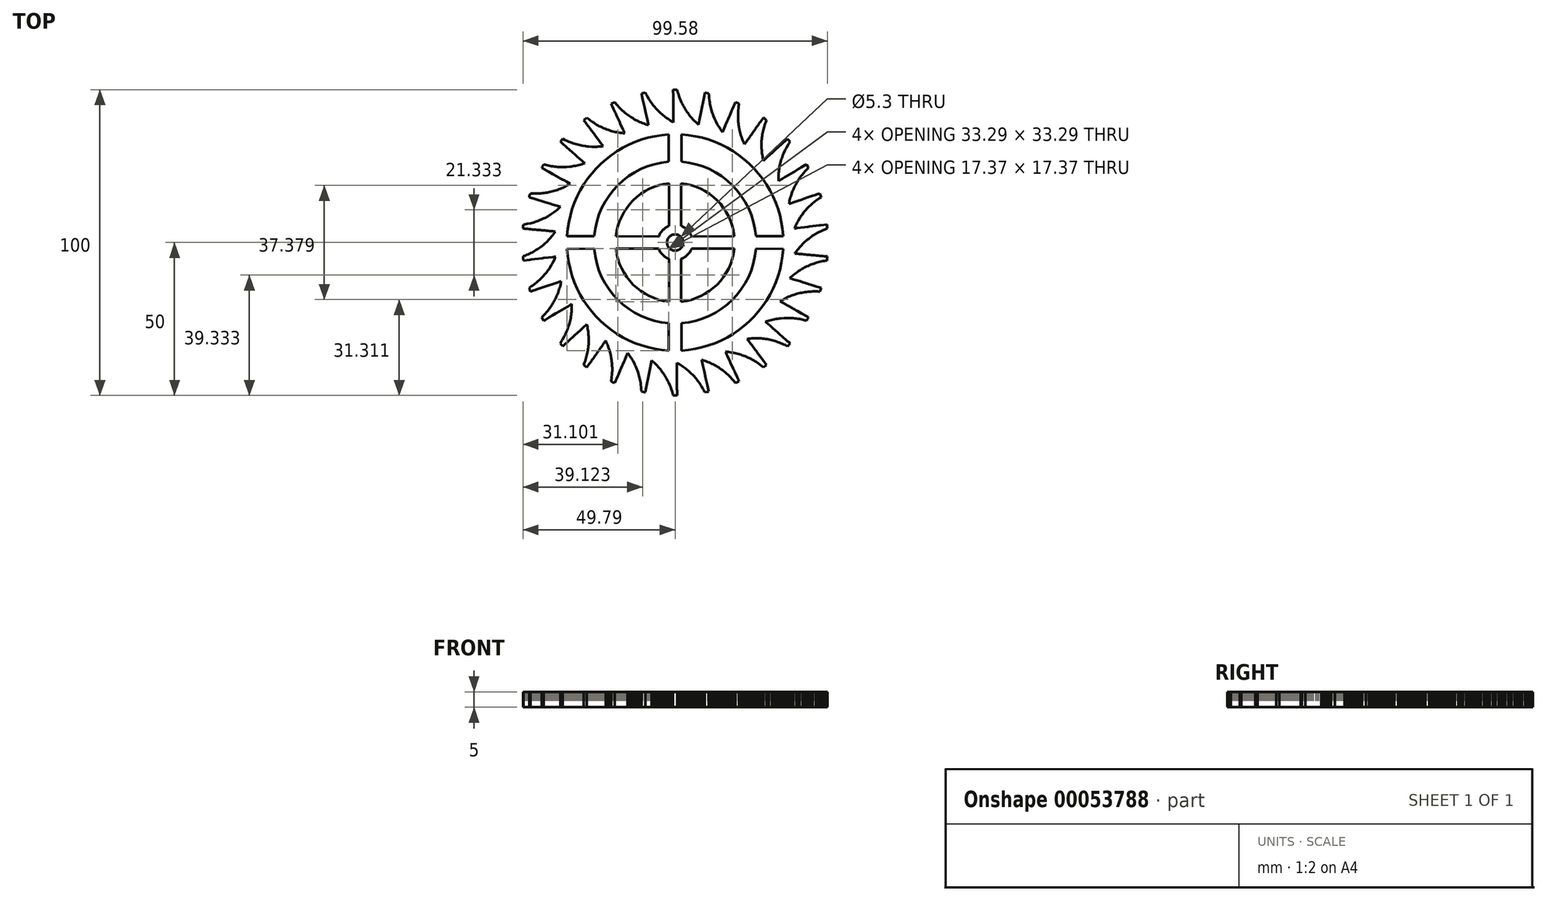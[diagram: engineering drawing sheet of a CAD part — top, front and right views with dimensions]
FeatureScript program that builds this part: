
annotation { "Feature Type Name" : "Feature", "Feature Type Description" : "" }
export const myFeature = defineFeature(function(context is Context, id is Id, definition is map)
    precondition{}
    {
        {
            var Q0;
            Q0=qCreatedBy(makeId("Top.planeOp"),FACE);
            var sketch = newSketch(context, id + "F0", { "sketchPlane" : qUnion([Q0])});
            skLineSegment(sketch, "E0", {"start": v(-36.72, 33.94) * mm, "end": v(-37.06, 33.56) * mm});
            skLineSegment(sketch, "E1", {"start": v(-37.06, 33.56) * mm, "end": v(-37.4, 33.18) * mm});
            skLineSegment(sketch, "E2", {"start": v(-37.4, 33.18) * mm, "end": v(-37.6, 32.97) * mm});
            skLineSegment(sketch, "E3", {"start": v(-37.6, 32.97) * mm, "end": v(-37.2, 32.63) * mm});
            skLineSegment(sketch, "E4", {"start": v(-37.2, 32.63) * mm, "end": v(-36.82, 32.3) * mm});
            skLineSegment(sketch, "E5", {"start": v(-36.82, 32.3) * mm, "end": v(-36.44, 31.95) * mm});
            skLineSegment(sketch, "E6", {"start": v(-36.44, 31.95) * mm, "end": v(-36.05, 31.62) * mm});
            skLineSegment(sketch, "E7", {"start": v(-36.05, 31.62) * mm, "end": v(-35.67, 31.28) * mm});
            skLineSegment(sketch, "E8", {"start": v(-35.67, 31.28) * mm, "end": v(-35.28, 30.94) * mm});
            skLineSegment(sketch, "E9", {"start": v(-35.28, 30.94) * mm, "end": v(-34.9, 30.6) * mm});
            skLineSegment(sketch, "E10", {"start": v(-34.9, 30.6) * mm, "end": v(-34.51, 30.27) * mm});
            skLineSegment(sketch, "E11", {"start": v(-34.51, 30.27) * mm, "end": v(-34.13, 29.93) * mm});
            skLineSegment(sketch, "E12", {"start": v(-34.13, 29.93) * mm, "end": v(-33.74, 29.6) * mm});
            skLineSegment(sketch, "E13", {"start": v(-33.74, 29.6) * mm, "end": v(-33.36, 29.25) * mm});
            skLineSegment(sketch, "E14", {"start": v(-33.36, 29.25) * mm, "end": v(-32.97, 28.92) * mm});
            skLineSegment(sketch, "E15", {"start": v(-32.97, 28.92) * mm, "end": v(-32.59, 28.58) * mm});
            skLineSegment(sketch, "E16", {"start": v(-32.59, 28.58) * mm, "end": v(-32.2, 28.24) * mm});
            skLineSegment(sketch, "E17", {"start": v(-32.2, 28.24) * mm, "end": v(-31.82, 27.9) * mm});
            skLineSegment(sketch, "E18", {"start": v(-31.82, 27.9) * mm, "end": v(-31.43, 27.57) * mm});
            skLineSegment(sketch, "E19", {"start": v(-31.43, 27.57) * mm, "end": v(-31.05, 27.23) * mm});
            skLineSegment(sketch, "E20", {"start": v(-31.05, 27.23) * mm, "end": v(-30.66, 26.9) * mm});
            skLineSegment(sketch, "E21", {"start": v(-30.66, 26.9) * mm, "end": v(-30.28, 26.55) * mm});
            skLineSegment(sketch, "E22", {"start": v(-30.28, 26.55) * mm, "end": v(-29.9, 26.22) * mm});
            skLineSegment(sketch, "E23", {"start": v(-29.9, 26.22) * mm, "end": v(-29.58, 25.94) * mm});
            skLineSegment(sketch, "E24", {"start": v(-29.58, 25.94) * mm, "end": v(-30.06, 25.77) * mm});
            skLineSegment(sketch, "E25", {"start": v(-30.06, 25.77) * mm, "end": v(-30.55, 25.62) * mm});
            skLineSegment(sketch, "E26", {"start": v(-30.55, 25.62) * mm, "end": v(-31.04, 25.47) * mm});
            skLineSegment(sketch, "E27", {"start": v(-31.04, 25.47) * mm, "end": v(-31.53, 25.33) * mm});
            skLineSegment(sketch, "E28", {"start": v(-31.53, 25.33) * mm, "end": v(-32.03, 25.21) * mm});
            skLineSegment(sketch, "E29", {"start": v(-32.03, 25.21) * mm, "end": v(-32.53, 25.1) * mm});
            skLineSegment(sketch, "E30", {"start": v(-32.53, 25.1) * mm, "end": v(-33.03, 25.01) * mm});
            skLineSegment(sketch, "E31", {"start": v(-33.03, 25.01) * mm, "end": v(-33.53, 24.92) * mm});
            skLineSegment(sketch, "E32", {"start": v(-33.53, 24.92) * mm, "end": v(-34.04, 24.85) * mm});
            skLineSegment(sketch, "E33", {"start": v(-34.04, 24.85) * mm, "end": v(-34.55, 24.8) * mm});
            skLineSegment(sketch, "E34", {"start": v(-34.55, 24.8) * mm, "end": v(-35.06, 24.75) * mm});
            skLineSegment(sketch, "E35", {"start": v(-35.06, 24.75) * mm, "end": v(-35.56, 24.7) * mm});
            skLineSegment(sketch, "E36", {"start": v(-35.56, 24.7) * mm, "end": v(-36.07, 24.68) * mm});
            skLineSegment(sketch, "E37", {"start": v(-36.07, 24.68) * mm, "end": v(-36.59, 24.67) * mm});
            skLineSegment(sketch, "E38", {"start": v(-36.59, 24.67) * mm, "end": v(-36.92, 24.66) * mm});
            skLineSegment(sketch, "E39", {"start": v(-36.92, 24.66) * mm, "end": v(-37.44, 24.67) * mm});
            skLineSegment(sketch, "E40", {"start": v(-37.44, 24.67) * mm, "end": v(-37.95, 24.7) * mm});
            skLineSegment(sketch, "E41", {"start": v(-37.95, 24.7) * mm, "end": v(-38.46, 24.73) * mm});
            skLineSegment(sketch, "E42", {"start": v(-38.46, 24.73) * mm, "end": v(-38.97, 24.77) * mm});
            skLineSegment(sketch, "E43", {"start": v(-38.97, 24.77) * mm, "end": v(-39.47, 24.83) * mm});
            skLineSegment(sketch, "E44", {"start": v(-39.47, 24.83) * mm, "end": v(-39.98, 24.9) * mm});
            skLineSegment(sketch, "E45", {"start": v(-39.98, 24.9) * mm, "end": v(-40.49, 24.99) * mm});
            skLineSegment(sketch, "E46", {"start": v(-40.49, 24.99) * mm, "end": v(-40.99, 25.07) * mm});
            skLineSegment(sketch, "E47", {"start": v(-40.99, 25.07) * mm, "end": v(-41.49, 25.18) * mm});
            skLineSegment(sketch, "E48", {"start": v(-41.49, 25.18) * mm, "end": v(-41.99, 25.3) * mm});
            skLineSegment(sketch, "E49", {"start": v(-41.99, 25.3) * mm, "end": v(-42.48, 25.43) * mm});
            skLineSegment(sketch, "E50", {"start": v(-42.48, 25.43) * mm, "end": v(-42.97, 25.56) * mm});
            skLineSegment(sketch, "E51", {"start": v(-42.97, 25.56) * mm, "end": v(-43.23, 25.12) * mm});
            skLineSegment(sketch, "E52", {"start": v(-43.23, 25.12) * mm, "end": v(-43.48, 24.68) * mm});
            skLineSegment(sketch, "E53", {"start": v(-43.48, 24.68) * mm, "end": v(-43.62, 24.43) * mm});
            skLineSegment(sketch, "E54", {"start": v(-43.62, 24.43) * mm, "end": v(-43.18, 24.18) * mm});
            skLineSegment(sketch, "E55", {"start": v(-43.18, 24.18) * mm, "end": v(-42.73, 23.93) * mm});
            skLineSegment(sketch, "E56", {"start": v(-42.73, 23.93) * mm, "end": v(-42.28, 23.68) * mm});
            skLineSegment(sketch, "E57", {"start": v(-42.28, 23.68) * mm, "end": v(-41.84, 23.43) * mm});
            skLineSegment(sketch, "E58", {"start": v(-41.84, 23.43) * mm, "end": v(-41.4, 23.18) * mm});
            skLineSegment(sketch, "E59", {"start": v(-41.4, 23.18) * mm, "end": v(-40.94, 22.93) * mm});
            skLineSegment(sketch, "E60", {"start": v(-40.94, 22.93) * mm, "end": v(-40.5, 22.68) * mm});
            skLineSegment(sketch, "E61", {"start": v(-40.5, 22.68) * mm, "end": v(-40.05, 22.43) * mm});
            skLineSegment(sketch, "E62", {"start": v(-40.05, 22.43) * mm, "end": v(-39.6, 22.18) * mm});
            skLineSegment(sketch, "E63", {"start": v(-39.6, 22.18) * mm, "end": v(-39.16, 21.93) * mm});
            skLineSegment(sketch, "E64", {"start": v(-39.16, 21.93) * mm, "end": v(-38.71, 21.68) * mm});
            skLineSegment(sketch, "E65", {"start": v(-38.71, 21.68) * mm, "end": v(-38.26, 21.43) * mm});
            skLineSegment(sketch, "E66", {"start": v(-38.26, 21.43) * mm, "end": v(-37.82, 21.18) * mm});
            skLineSegment(sketch, "E67", {"start": v(-37.82, 21.18) * mm, "end": v(-37.37, 20.93) * mm});
            skLineSegment(sketch, "E68", {"start": v(-37.37, 20.93) * mm, "end": v(-36.92, 20.68) * mm});
            skLineSegment(sketch, "E69", {"start": v(-36.92, 20.68) * mm, "end": v(-36.48, 20.43) * mm});
            skLineSegment(sketch, "E70", {"start": v(-36.48, 20.43) * mm, "end": v(-36.03, 20.18) * mm});
            skLineSegment(sketch, "E71", {"start": v(-36.03, 20.18) * mm, "end": v(-35.58, 19.93) * mm});
            skLineSegment(sketch, "E72", {"start": v(-35.58, 19.93) * mm, "end": v(-35.14, 19.68) * mm});
            skLineSegment(sketch, "E73", {"start": v(-35.14, 19.68) * mm, "end": v(-34.69, 19.43) * mm});
            skLineSegment(sketch, "E74", {"start": v(-34.69, 19.43) * mm, "end": v(-34.32, 19.22) * mm});
            skLineSegment(sketch, "E75", {"start": v(-34.32, 19.22) * mm, "end": v(-34.76, 18.96) * mm});
            skLineSegment(sketch, "E76", {"start": v(-34.76, 18.96) * mm, "end": v(-35.2, 18.7) * mm});
            skLineSegment(sketch, "E77", {"start": v(-35.2, 18.7) * mm, "end": v(-35.66, 18.46) * mm});
            skLineSegment(sketch, "E78", {"start": v(-35.66, 18.46) * mm, "end": v(-36.1, 18.23) * mm});
            skLineSegment(sketch, "E79", {"start": v(-36.1, 18.23) * mm, "end": v(-36.57, 18) * mm});
            skLineSegment(sketch, "E80", {"start": v(-36.57, 18) * mm, "end": v(-37.04, 17.8) * mm});
            skLineSegment(sketch, "E81", {"start": v(-37.04, 17.8) * mm, "end": v(-37.5, 17.6) * mm});
            skLineSegment(sketch, "E82", {"start": v(-37.5, 17.6) * mm, "end": v(-37.98, 17.4) * mm});
            skLineSegment(sketch, "E83", {"start": v(-37.98, 17.4) * mm, "end": v(-38.46, 17.23) * mm});
            skLineSegment(sketch, "E84", {"start": v(-38.46, 17.23) * mm, "end": v(-38.95, 17.07) * mm});
            skLineSegment(sketch, "E85", {"start": v(-38.95, 17.07) * mm, "end": v(-39.43, 16.92) * mm});
            skLineSegment(sketch, "E86", {"start": v(-39.43, 16.92) * mm, "end": v(-39.92, 16.77) * mm});
            skLineSegment(sketch, "E87", {"start": v(-39.92, 16.77) * mm, "end": v(-40.42, 16.64) * mm});
            skLineSegment(sketch, "E88", {"start": v(-40.42, 16.64) * mm, "end": v(-40.92, 16.52) * mm});
            skLineSegment(sketch, "E89", {"start": v(-40.92, 16.52) * mm, "end": v(-41.42, 16.42) * mm});
            skLineSegment(sketch, "E90", {"start": v(-41.42, 16.42) * mm, "end": v(-41.91, 16.32) * mm});
            skLineSegment(sketch, "E91", {"start": v(-41.91, 16.32) * mm, "end": v(-42.42, 16.24) * mm});
            skLineSegment(sketch, "E92", {"start": v(-42.42, 16.24) * mm, "end": v(-42.93, 16.17) * mm});
            skLineSegment(sketch, "E93", {"start": v(-42.93, 16.17) * mm, "end": v(-43.44, 16.12) * mm});
            skLineSegment(sketch, "E94", {"start": v(-43.44, 16.12) * mm, "end": v(-43.94, 16.06) * mm});
            skLineSegment(sketch, "E95", {"start": v(-43.94, 16.06) * mm, "end": v(-44.45, 16.03) * mm});
            skLineSegment(sketch, "E96", {"start": v(-44.45, 16.03) * mm, "end": v(-44.97, 16.01) * mm});
            skLineSegment(sketch, "E97", {"start": v(-44.97, 16.01) * mm, "end": v(-45.3, 16) * mm});
            skLineSegment(sketch, "E98", {"start": v(-45.3, 16) * mm, "end": v(-45.82, 16) * mm});
            skLineSegment(sketch, "E99", {"start": v(-45.82, 16) * mm, "end": v(-46.33, 16.02) * mm});
            skLineSegment(sketch, "E100", {"start": v(-46.33, 16.02) * mm, "end": v(-46.84, 16.04) * mm});
            skLineSegment(sketch, "E101", {"start": v(-46.84, 16.04) * mm, "end": v(-47.35, 16.07) * mm});
            skLineSegment(sketch, "E102", {"start": v(-47.35, 16.07) * mm, "end": v(-47.5, 15.58) * mm});
            skLineSegment(sketch, "E103", {"start": v(-47.5, 15.58) * mm, "end": v(-47.66, 15.1) * mm});
            skLineSegment(sketch, "E104", {"start": v(-47.66, 15.1) * mm, "end": v(-47.75, 14.83) * mm});
            skLineSegment(sketch, "E105", {"start": v(-47.75, 14.83) * mm, "end": v(-47.26, 14.68) * mm});
            skLineSegment(sketch, "E106", {"start": v(-47.26, 14.68) * mm, "end": v(-46.77, 14.52) * mm});
            skLineSegment(sketch, "E107", {"start": v(-46.77, 14.52) * mm, "end": v(-46.28, 14.37) * mm});
            skLineSegment(sketch, "E108", {"start": v(-46.28, 14.37) * mm, "end": v(-45.8, 14.22) * mm});
            skLineSegment(sketch, "E109", {"start": v(-45.8, 14.22) * mm, "end": v(-45.3, 14.07) * mm});
            skLineSegment(sketch, "E110", {"start": v(-45.3, 14.07) * mm, "end": v(-44.82, 13.92) * mm});
            skLineSegment(sketch, "E111", {"start": v(-44.82, 13.92) * mm, "end": v(-44.33, 13.76) * mm});
            skLineSegment(sketch, "E112", {"start": v(-44.33, 13.76) * mm, "end": v(-43.84, 13.61) * mm});
            skLineSegment(sketch, "E113", {"start": v(-43.84, 13.61) * mm, "end": v(-43.35, 13.46) * mm});
            skLineSegment(sketch, "E114", {"start": v(-43.35, 13.46) * mm, "end": v(-42.86, 13.3) * mm});
            skLineSegment(sketch, "E115", {"start": v(-42.86, 13.3) * mm, "end": v(-42.37, 13.16) * mm});
            skLineSegment(sketch, "E116", {"start": v(-42.37, 13.16) * mm, "end": v(-41.88, 13) * mm});
            skLineSegment(sketch, "E117", {"start": v(-41.88, 13) * mm, "end": v(-41.4, 12.85) * mm});
            skLineSegment(sketch, "E118", {"start": v(-41.4, 12.85) * mm, "end": v(-40.9, 12.7) * mm});
            skLineSegment(sketch, "E119", {"start": v(-40.9, 12.7) * mm, "end": v(-40.42, 12.55) * mm});
            skLineSegment(sketch, "E120", {"start": v(-40.42, 12.55) * mm, "end": v(-39.93, 12.4) * mm});
            skLineSegment(sketch, "E121", {"start": v(-39.93, 12.4) * mm, "end": v(-39.44, 12.25) * mm});
            skLineSegment(sketch, "E122", {"start": v(-39.44, 12.25) * mm, "end": v(-38.95, 12.1) * mm});
            skLineSegment(sketch, "E123", {"start": v(-38.95, 12.1) * mm, "end": v(-38.46, 11.94) * mm});
            skLineSegment(sketch, "E124", {"start": v(-38.46, 11.94) * mm, "end": v(-37.97, 11.8) * mm});
            skLineSegment(sketch, "E125", {"start": v(-37.97, 11.8) * mm, "end": v(-37.57, 11.67) * mm});
            skLineSegment(sketch, "E126", {"start": v(-37.57, 11.67) * mm, "end": v(-37.94, 11.32) * mm});
            skLineSegment(sketch, "E127", {"start": v(-37.94, 11.32) * mm, "end": v(-38.33, 10.98) * mm});
            skLineSegment(sketch, "E128", {"start": v(-38.33, 10.98) * mm, "end": v(-38.72, 10.65) * mm});
            skLineSegment(sketch, "E129", {"start": v(-38.72, 10.65) * mm, "end": v(-39.1, 10.32) * mm});
            skLineSegment(sketch, "E130", {"start": v(-39.1, 10.32) * mm, "end": v(-39.51, 10) * mm});
            skLineSegment(sketch, "E131", {"start": v(-39.51, 10) * mm, "end": v(-39.93, 9.7) * mm});
            skLineSegment(sketch, "E132", {"start": v(-39.93, 9.7) * mm, "end": v(-40.35, 9.42) * mm});
            skLineSegment(sketch, "E133", {"start": v(-40.35, 9.42) * mm, "end": v(-40.77, 9.13) * mm});
            skLineSegment(sketch, "E134", {"start": v(-40.77, 9.13) * mm, "end": v(-41.2, 8.86) * mm});
            skLineSegment(sketch, "E135", {"start": v(-41.2, 8.86) * mm, "end": v(-41.64, 8.6) * mm});
            skLineSegment(sketch, "E136", {"start": v(-41.64, 8.6) * mm, "end": v(-42.1, 8.35) * mm});
            skLineSegment(sketch, "E137", {"start": v(-42.1, 8.35) * mm, "end": v(-42.53, 8.1) * mm});
            skLineSegment(sketch, "E138", {"start": v(-42.53, 8.1) * mm, "end": v(-43, 7.87) * mm});
            skLineSegment(sketch, "E139", {"start": v(-43, 7.87) * mm, "end": v(-43.46, 7.66) * mm});
            skLineSegment(sketch, "E140", {"start": v(-43.46, 7.66) * mm, "end": v(-43.93, 7.45) * mm});
            skLineSegment(sketch, "E141", {"start": v(-43.93, 7.45) * mm, "end": v(-44.4, 7.25) * mm});
            skLineSegment(sketch, "E142", {"start": v(-44.4, 7.25) * mm, "end": v(-44.87, 7.06) * mm});
            skLineSegment(sketch, "E143", {"start": v(-44.87, 7.06) * mm, "end": v(-45.35, 6.9) * mm});
            skLineSegment(sketch, "E144", {"start": v(-45.35, 6.9) * mm, "end": v(-45.84, 6.73) * mm});
            skLineSegment(sketch, "E145", {"start": v(-45.84, 6.73) * mm, "end": v(-46.32, 6.58) * mm});
            skLineSegment(sketch, "E146", {"start": v(-46.32, 6.58) * mm, "end": v(-46.82, 6.44) * mm});
            skLineSegment(sketch, "E147", {"start": v(-46.82, 6.44) * mm, "end": v(-47.31, 6.32) * mm});
            skLineSegment(sketch, "E148", {"start": v(-47.31, 6.32) * mm, "end": v(-47.81, 6.2) * mm});
            skLineSegment(sketch, "E149", {"start": v(-47.81, 6.2) * mm, "end": v(-48.3, 6.1) * mm});
            skLineSegment(sketch, "E150", {"start": v(-48.3, 6.1) * mm, "end": v(-48.81, 6) * mm});
            skLineSegment(sketch, "E151", {"start": v(-48.81, 6) * mm, "end": v(-49.32, 5.93) * mm});
            skLineSegment(sketch, "E152", {"start": v(-49.32, 5.93) * mm, "end": v(-49.65, 5.88) * mm});
            skLineSegment(sketch, "E153", {"start": v(-49.65, 5.88) * mm, "end": v(-49.7, 5.37) * mm});
            skLineSegment(sketch, "E154", {"start": v(-49.7, 5.37) * mm, "end": v(-49.76, 4.86) * mm});
            skLineSegment(sketch, "E155", {"start": v(-49.76, 4.86) * mm, "end": v(-49.8, 4.58) * mm});
            skLineSegment(sketch, "E156", {"start": v(-49.8, 4.58) * mm, "end": v(-49.28, 4.53) * mm});
            skLineSegment(sketch, "E157", {"start": v(-49.28, 4.53) * mm, "end": v(-48.77, 4.48) * mm});
            skLineSegment(sketch, "E158", {"start": v(-48.77, 4.48) * mm, "end": v(-48.26, 4.43) * mm});
            skLineSegment(sketch, "E159", {"start": v(-48.26, 4.43) * mm, "end": v(-47.75, 4.39) * mm});
            skLineSegment(sketch, "E160", {"start": v(-47.75, 4.39) * mm, "end": v(-47.24, 4.34) * mm});
            skLineSegment(sketch, "E161", {"start": v(-47.24, 4.34) * mm, "end": v(-46.73, 4.3) * mm});
            skLineSegment(sketch, "E162", {"start": v(-46.73, 4.3) * mm, "end": v(-46.22, 4.25) * mm});
            skLineSegment(sketch, "E163", {"start": v(-46.22, 4.25) * mm, "end": v(-45.71, 4.2) * mm});
            skLineSegment(sketch, "E164", {"start": v(-45.71, 4.2) * mm, "end": v(-45.2, 4.15) * mm});
            skLineSegment(sketch, "E165", {"start": v(-45.2, 4.15) * mm, "end": v(-44.7, 4.1) * mm});
            skLineSegment(sketch, "E166", {"start": v(-44.7, 4.1) * mm, "end": v(-44.18, 4.06) * mm});
            skLineSegment(sketch, "E167", {"start": v(-44.18, 4.06) * mm, "end": v(-43.67, 4.01) * mm});
            skLineSegment(sketch, "E168", {"start": v(-43.67, 4.01) * mm, "end": v(-43.16, 3.97) * mm});
            skLineSegment(sketch, "E169", {"start": v(-43.16, 3.97) * mm, "end": v(-42.65, 3.92) * mm});
            skLineSegment(sketch, "E170", {"start": v(-42.65, 3.92) * mm, "end": v(-42.14, 3.87) * mm});
            skLineSegment(sketch, "E171", {"start": v(-42.14, 3.87) * mm, "end": v(-41.63, 3.83) * mm});
            skLineSegment(sketch, "E172", {"start": v(-41.63, 3.83) * mm, "end": v(-41.12, 3.78) * mm});
            skLineSegment(sketch, "E173", {"start": v(-41.12, 3.78) * mm, "end": v(-40.61, 3.73) * mm});
            skLineSegment(sketch, "E174", {"start": v(-40.61, 3.73) * mm, "end": v(-40.1, 3.68) * mm});
            skLineSegment(sketch, "E175", {"start": v(-40.1, 3.68) * mm, "end": v(-39.6, 3.64) * mm});
            skLineSegment(sketch, "E176", {"start": v(-39.6, 3.64) * mm, "end": v(-39.17, 3.6) * mm});
            skLineSegment(sketch, "E177", {"start": v(-39.17, 3.6) * mm, "end": v(-39.47, 3.18) * mm});
            skLineSegment(sketch, "E178", {"start": v(-39.47, 3.18) * mm, "end": v(-39.77, 2.77) * mm});
            skLineSegment(sketch, "E179", {"start": v(-39.77, 2.77) * mm, "end": v(-40.09, 2.36) * mm});
            skLineSegment(sketch, "E180", {"start": v(-40.09, 2.36) * mm, "end": v(-40.4, 1.96) * mm});
            skLineSegment(sketch, "E181", {"start": v(-40.4, 1.96) * mm, "end": v(-40.73, 1.57) * mm});
            skLineSegment(sketch, "E182", {"start": v(-40.73, 1.57) * mm, "end": v(-41.07, 1.2) * mm});
            skLineSegment(sketch, "E183", {"start": v(-41.07, 1.2) * mm, "end": v(-41.42, 0.82) * mm});
            skLineSegment(sketch, "E184", {"start": v(-41.42, 0.82) * mm, "end": v(-41.77, 0.45) * mm});
            skLineSegment(sketch, "E185", {"start": v(-41.77, 0.45) * mm, "end": v(-42.14, 0.1) * mm});
            skLineSegment(sketch, "E186", {"start": v(-42.14, 0.1) * mm, "end": v(-42.52, -0.25) * mm});
            skLineSegment(sketch, "E187", {"start": v(-42.52, -0.25) * mm, "end": v(-42.9, -0.59) * mm});
            skLineSegment(sketch, "E188", {"start": v(-42.9, -0.59) * mm, "end": v(-43.29, -0.92) * mm});
            skLineSegment(sketch, "E189", {"start": v(-43.29, -0.92) * mm, "end": v(-43.69, -1.24) * mm});
            skLineSegment(sketch, "E190", {"start": v(-43.69, -1.24) * mm, "end": v(-44.1, -1.55) * mm});
            skLineSegment(sketch, "E191", {"start": v(-44.1, -1.55) * mm, "end": v(-44.52, -1.84) * mm});
            skLineSegment(sketch, "E192", {"start": v(-44.52, -1.84) * mm, "end": v(-44.93, -2.14) * mm});
            skLineSegment(sketch, "E193", {"start": v(-44.93, -2.14) * mm, "end": v(-45.36, -2.42) * mm});
            skLineSegment(sketch, "E194", {"start": v(-45.36, -2.42) * mm, "end": v(-45.8, -2.69) * mm});
            skLineSegment(sketch, "E195", {"start": v(-45.8, -2.69) * mm, "end": v(-46.24, -2.94) * mm});
            skLineSegment(sketch, "E196", {"start": v(-46.24, -2.94) * mm, "end": v(-46.68, -3.2) * mm});
            skLineSegment(sketch, "E197", {"start": v(-46.68, -3.2) * mm, "end": v(-47.13, -3.43) * mm});
            skLineSegment(sketch, "E198", {"start": v(-47.13, -3.43) * mm, "end": v(-47.6, -3.66) * mm});
            skLineSegment(sketch, "E199", {"start": v(-47.6, -3.66) * mm, "end": v(-48.06, -3.87) * mm});
            skLineSegment(sketch, "E200", {"start": v(-48.06, -3.87) * mm, "end": v(-48.52, -4.08) * mm});
            skLineSegment(sketch, "E201", {"start": v(-48.52, -4.08) * mm, "end": v(-49, -4.28) * mm});
            skLineSegment(sketch, "E202", {"start": v(-49, -4.28) * mm, "end": v(-49.47, -4.46) * mm});
            skLineSegment(sketch, "E203", {"start": v(-49.47, -4.46) * mm, "end": v(-49.8, -4.58) * mm});
            skLineSegment(sketch, "E204", {"start": v(-49.8, -4.58) * mm, "end": v(-49.74, -5.08) * mm});
            skLineSegment(sketch, "E205", {"start": v(-49.74, -5.08) * mm, "end": v(-49.68, -5.6) * mm});
            skLineSegment(sketch, "E206", {"start": v(-49.68, -5.6) * mm, "end": v(-49.65, -5.88) * mm});
            skLineSegment(sketch, "E207", {"start": v(-49.65, -5.88) * mm, "end": v(-49.14, -5.82) * mm});
            skLineSegment(sketch, "E208", {"start": v(-49.14, -5.82) * mm, "end": v(-48.64, -5.76) * mm});
            skLineSegment(sketch, "E209", {"start": v(-48.64, -5.76) * mm, "end": v(-48.13, -5.7) * mm});
            skLineSegment(sketch, "E210", {"start": v(-48.13, -5.7) * mm, "end": v(-47.62, -5.64) * mm});
            skLineSegment(sketch, "E211", {"start": v(-47.62, -5.64) * mm, "end": v(-47.11, -5.58) * mm});
            skLineSegment(sketch, "E212", {"start": v(-47.11, -5.58) * mm, "end": v(-46.6, -5.52) * mm});
            skLineSegment(sketch, "E213", {"start": v(-46.6, -5.52) * mm, "end": v(-46.1, -5.46) * mm});
            skLineSegment(sketch, "E214", {"start": v(-46.1, -5.46) * mm, "end": v(-45.59, -5.4) * mm});
            skLineSegment(sketch, "E215", {"start": v(-45.59, -5.4) * mm, "end": v(-45.08, -5.34) * mm});
            skLineSegment(sketch, "E216", {"start": v(-45.08, -5.34) * mm, "end": v(-44.57, -5.28) * mm});
            skLineSegment(sketch, "E217", {"start": v(-44.57, -5.28) * mm, "end": v(-44.06, -5.21) * mm});
            skLineSegment(sketch, "E218", {"start": v(-44.06, -5.21) * mm, "end": v(-43.55, -5.15) * mm});
            skLineSegment(sketch, "E219", {"start": v(-43.55, -5.15) * mm, "end": v(-43.04, -5.1) * mm});
            skLineSegment(sketch, "E220", {"start": v(-43.04, -5.1) * mm, "end": v(-42.53, -5.03) * mm});
            skLineSegment(sketch, "E221", {"start": v(-42.53, -5.03) * mm, "end": v(-42.03, -4.97) * mm});
            skLineSegment(sketch, "E222", {"start": v(-42.03, -4.97) * mm, "end": v(-41.52, -4.91) * mm});
            skLineSegment(sketch, "E223", {"start": v(-41.52, -4.91) * mm, "end": v(-41, -4.85) * mm});
            skLineSegment(sketch, "E224", {"start": v(-41, -4.85) * mm, "end": v(-40.5, -4.8) * mm});
            skLineSegment(sketch, "E225", {"start": v(-40.5, -4.8) * mm, "end": v(-40, -4.73) * mm});
            skLineSegment(sketch, "E226", {"start": v(-40, -4.73) * mm, "end": v(-39.48, -4.67) * mm});
            skLineSegment(sketch, "E227", {"start": v(-39.48, -4.67) * mm, "end": v(-39.06, -4.62) * mm});
            skLineSegment(sketch, "E228", {"start": v(-39.06, -4.62) * mm, "end": v(-39.26, -5.1) * mm});
            skLineSegment(sketch, "E229", {"start": v(-39.26, -5.1) * mm, "end": v(-39.48, -5.56) * mm});
            skLineSegment(sketch, "E230", {"start": v(-39.48, -5.56) * mm, "end": v(-39.7, -6.02) * mm});
            skLineSegment(sketch, "E231", {"start": v(-39.7, -6.02) * mm, "end": v(-39.92, -6.48) * mm});
            skLineSegment(sketch, "E232", {"start": v(-39.92, -6.48) * mm, "end": v(-40.17, -6.93) * mm});
            skLineSegment(sketch, "E233", {"start": v(-40.17, -6.93) * mm, "end": v(-40.42, -7.37) * mm});
            skLineSegment(sketch, "E234", {"start": v(-40.42, -7.37) * mm, "end": v(-40.7, -7.8) * mm});
            skLineSegment(sketch, "E235", {"start": v(-40.7, -7.8) * mm, "end": v(-40.96, -8.24) * mm});
            skLineSegment(sketch, "E236", {"start": v(-40.96, -8.24) * mm, "end": v(-41.24, -8.67) * mm});
            skLineSegment(sketch, "E237", {"start": v(-41.24, -8.67) * mm, "end": v(-41.54, -9.08) * mm});
            skLineSegment(sketch, "E238", {"start": v(-41.54, -9.08) * mm, "end": v(-41.85, -9.5) * mm});
            skLineSegment(sketch, "E239", {"start": v(-41.85, -9.5) * mm, "end": v(-42.15, -9.9) * mm});
            skLineSegment(sketch, "E240", {"start": v(-42.15, -9.9) * mm, "end": v(-42.48, -10.3) * mm});
            skLineSegment(sketch, "E241", {"start": v(-42.48, -10.3) * mm, "end": v(-42.81, -10.68) * mm});
            skLineSegment(sketch, "E242", {"start": v(-42.81, -10.68) * mm, "end": v(-43.16, -11.06) * mm});
            skLineSegment(sketch, "E243", {"start": v(-43.16, -11.06) * mm, "end": v(-43.5, -11.43) * mm});
            skLineSegment(sketch, "E244", {"start": v(-43.5, -11.43) * mm, "end": v(-43.86, -11.8) * mm});
            skLineSegment(sketch, "E245", {"start": v(-43.86, -11.8) * mm, "end": v(-44.23, -12.15) * mm});
            skLineSegment(sketch, "E246", {"start": v(-44.23, -12.15) * mm, "end": v(-44.61, -12.5) * mm});
            skLineSegment(sketch, "E247", {"start": v(-44.61, -12.5) * mm, "end": v(-45, -12.83) * mm});
            skLineSegment(sketch, "E248", {"start": v(-45, -12.83) * mm, "end": v(-45.39, -13.16) * mm});
            skLineSegment(sketch, "E249", {"start": v(-45.39, -13.16) * mm, "end": v(-45.8, -13.47) * mm});
            skLineSegment(sketch, "E250", {"start": v(-45.8, -13.47) * mm, "end": v(-46.2, -13.78) * mm});
            skLineSegment(sketch, "E251", {"start": v(-46.2, -13.78) * mm, "end": v(-46.6, -14.08) * mm});
            skLineSegment(sketch, "E252", {"start": v(-46.6, -14.08) * mm, "end": v(-47.03, -14.37) * mm});
            skLineSegment(sketch, "E253", {"start": v(-47.03, -14.37) * mm, "end": v(-47.47, -14.64) * mm});
            skLineSegment(sketch, "E254", {"start": v(-47.47, -14.64) * mm, "end": v(-47.75, -14.83) * mm});
            skLineSegment(sketch, "E255", {"start": v(-47.75, -14.83) * mm, "end": v(-47.6, -15.31) * mm});
            skLineSegment(sketch, "E256", {"start": v(-47.6, -15.31) * mm, "end": v(-47.43, -15.8) * mm});
            skLineSegment(sketch, "E257", {"start": v(-47.43, -15.8) * mm, "end": v(-47.35, -16.07) * mm});
            skLineSegment(sketch, "E258", {"start": v(-47.35, -16.07) * mm, "end": v(-46.86, -15.9) * mm});
            skLineSegment(sketch, "E259", {"start": v(-46.86, -15.9) * mm, "end": v(-46.38, -15.74) * mm});
            skLineSegment(sketch, "E260", {"start": v(-46.38, -15.74) * mm, "end": v(-45.9, -15.58) * mm});
            skLineSegment(sketch, "E261", {"start": v(-45.9, -15.58) * mm, "end": v(-45.4, -15.41) * mm});
            skLineSegment(sketch, "E262", {"start": v(-45.4, -15.41) * mm, "end": v(-44.92, -15.25) * mm});
            skLineSegment(sketch, "E263", {"start": v(-44.92, -15.25) * mm, "end": v(-44.44, -15.08) * mm});
            skLineSegment(sketch, "E264", {"start": v(-44.44, -15.08) * mm, "end": v(-43.95, -14.92) * mm});
            skLineSegment(sketch, "E265", {"start": v(-43.95, -14.92) * mm, "end": v(-43.47, -14.76) * mm});
            skLineSegment(sketch, "E266", {"start": v(-43.47, -14.76) * mm, "end": v(-42.98, -14.6) * mm});
            skLineSegment(sketch, "E267", {"start": v(-42.98, -14.6) * mm, "end": v(-42.5, -14.43) * mm});
            skLineSegment(sketch, "E268", {"start": v(-42.5, -14.43) * mm, "end": v(-42.01, -14.26) * mm});
            skLineSegment(sketch, "E269", {"start": v(-42.01, -14.26) * mm, "end": v(-41.53, -14.1) * mm});
            skLineSegment(sketch, "E270", {"start": v(-41.53, -14.1) * mm, "end": v(-41.04, -13.93) * mm});
            skLineSegment(sketch, "E271", {"start": v(-41.04, -13.93) * mm, "end": v(-40.56, -13.77) * mm});
            skLineSegment(sketch, "E272", {"start": v(-40.56, -13.77) * mm, "end": v(-40.07, -13.6) * mm});
            skLineSegment(sketch, "E273", {"start": v(-40.07, -13.6) * mm, "end": v(-39.59, -13.44) * mm});
            skLineSegment(sketch, "E274", {"start": v(-39.59, -13.44) * mm, "end": v(-39.1, -13.27) * mm});
            skLineSegment(sketch, "E275", {"start": v(-39.1, -13.27) * mm, "end": v(-38.62, -13.1) * mm});
            skLineSegment(sketch, "E276", {"start": v(-38.62, -13.1) * mm, "end": v(-38.13, -12.94) * mm});
            skLineSegment(sketch, "E277", {"start": v(-38.13, -12.94) * mm, "end": v(-37.65, -12.78) * mm});
            skLineSegment(sketch, "E278", {"start": v(-37.65, -12.78) * mm, "end": v(-37.25, -12.64) * mm});
            skLineSegment(sketch, "E279", {"start": v(-37.25, -12.64) * mm, "end": v(-37.35, -13.15) * mm});
            skLineSegment(sketch, "E280", {"start": v(-37.35, -13.15) * mm, "end": v(-37.46, -13.65) * mm});
            skLineSegment(sketch, "E281", {"start": v(-37.46, -13.65) * mm, "end": v(-37.58, -14.14) * mm});
            skLineSegment(sketch, "E282", {"start": v(-37.58, -14.14) * mm, "end": v(-37.7, -14.64) * mm});
            skLineSegment(sketch, "E283", {"start": v(-37.7, -14.64) * mm, "end": v(-37.85, -15.13) * mm});
            skLineSegment(sketch, "E284", {"start": v(-37.85, -15.13) * mm, "end": v(-38, -15.62) * mm});
            skLineSegment(sketch, "E285", {"start": v(-38, -15.62) * mm, "end": v(-38.18, -16.1) * mm});
            skLineSegment(sketch, "E286", {"start": v(-38.18, -16.1) * mm, "end": v(-38.35, -16.58) * mm});
            skLineSegment(sketch, "E287", {"start": v(-38.35, -16.58) * mm, "end": v(-38.54, -17.05) * mm});
            skLineSegment(sketch, "E288", {"start": v(-38.54, -17.05) * mm, "end": v(-38.74, -17.52) * mm});
            skLineSegment(sketch, "E289", {"start": v(-38.74, -17.52) * mm, "end": v(-38.96, -17.99) * mm});
            skLineSegment(sketch, "E290", {"start": v(-38.96, -17.99) * mm, "end": v(-39.17, -18.45) * mm});
            skLineSegment(sketch, "E291", {"start": v(-39.17, -18.45) * mm, "end": v(-39.4, -18.9) * mm});
            skLineSegment(sketch, "E292", {"start": v(-39.4, -18.9) * mm, "end": v(-39.66, -19.35) * mm});
            skLineSegment(sketch, "E293", {"start": v(-39.66, -19.35) * mm, "end": v(-39.92, -19.8) * mm});
            skLineSegment(sketch, "E294", {"start": v(-39.92, -19.8) * mm, "end": v(-40.17, -20.23) * mm});
            skLineSegment(sketch, "E295", {"start": v(-40.17, -20.23) * mm, "end": v(-40.45, -20.66) * mm});
            skLineSegment(sketch, "E296", {"start": v(-40.45, -20.66) * mm, "end": v(-40.74, -21.08) * mm});
            skLineSegment(sketch, "E297", {"start": v(-40.74, -21.08) * mm, "end": v(-41.04, -21.5) * mm});
            skLineSegment(sketch, "E298", {"start": v(-41.04, -21.5) * mm, "end": v(-41.34, -21.9) * mm});
            skLineSegment(sketch, "E299", {"start": v(-41.34, -21.9) * mm, "end": v(-41.66, -22.3) * mm});
            skLineSegment(sketch, "E300", {"start": v(-41.66, -22.3) * mm, "end": v(-41.99, -22.7) * mm});
            skLineSegment(sketch, "E301", {"start": v(-41.99, -22.7) * mm, "end": v(-42.33, -23.08) * mm});
            skLineSegment(sketch, "E302", {"start": v(-42.33, -23.08) * mm, "end": v(-42.66, -23.47) * mm});
            skLineSegment(sketch, "E303", {"start": v(-42.66, -23.47) * mm, "end": v(-43.02, -23.83) * mm});
            skLineSegment(sketch, "E304", {"start": v(-43.02, -23.83) * mm, "end": v(-43.38, -24.2) * mm});
            skLineSegment(sketch, "E305", {"start": v(-43.38, -24.2) * mm, "end": v(-43.62, -24.43) * mm});
            skLineSegment(sketch, "E306", {"start": v(-43.62, -24.43) * mm, "end": v(-43.37, -24.87) * mm});
            skLineSegment(sketch, "E307", {"start": v(-43.37, -24.87) * mm, "end": v(-43.11, -25.32) * mm});
            skLineSegment(sketch, "E308", {"start": v(-43.11, -25.32) * mm, "end": v(-42.97, -25.56) * mm});
            skLineSegment(sketch, "E309", {"start": v(-42.97, -25.56) * mm, "end": v(-42.53, -25.3) * mm});
            skLineSegment(sketch, "E310", {"start": v(-42.53, -25.3) * mm, "end": v(-42.1, -25.04) * mm});
            skLineSegment(sketch, "E311", {"start": v(-42.1, -25.04) * mm, "end": v(-41.65, -24.78) * mm});
            skLineSegment(sketch, "E312", {"start": v(-41.65, -24.78) * mm, "end": v(-41.21, -24.52) * mm});
            skLineSegment(sketch, "E313", {"start": v(-41.21, -24.52) * mm, "end": v(-40.77, -24.26) * mm});
            skLineSegment(sketch, "E314", {"start": v(-40.77, -24.26) * mm, "end": v(-40.33, -24) * mm});
            skLineSegment(sketch, "E315", {"start": v(-40.33, -24) * mm, "end": v(-39.89, -23.73) * mm});
            skLineSegment(sketch, "E316", {"start": v(-39.89, -23.73) * mm, "end": v(-39.45, -23.47) * mm});
            skLineSegment(sketch, "E317", {"start": v(-39.45, -23.47) * mm, "end": v(-39, -23.2) * mm});
            skLineSegment(sketch, "E318", {"start": v(-39, -23.2) * mm, "end": v(-38.57, -22.95) * mm});
            skLineSegment(sketch, "E319", {"start": v(-38.57, -22.95) * mm, "end": v(-38.13, -22.68) * mm});
            skLineSegment(sketch, "E320", {"start": v(-38.13, -22.68) * mm, "end": v(-37.69, -22.42) * mm});
            skLineSegment(sketch, "E321", {"start": v(-37.69, -22.42) * mm, "end": v(-37.25, -22.16) * mm});
            skLineSegment(sketch, "E322", {"start": v(-37.25, -22.16) * mm, "end": v(-36.8, -21.9) * mm});
            skLineSegment(sketch, "E323", {"start": v(-36.8, -21.9) * mm, "end": v(-36.37, -21.64) * mm});
            skLineSegment(sketch, "E324", {"start": v(-36.37, -21.64) * mm, "end": v(-35.93, -21.38) * mm});
            skLineSegment(sketch, "E325", {"start": v(-35.93, -21.38) * mm, "end": v(-35.49, -21.11) * mm});
            skLineSegment(sketch, "E326", {"start": v(-35.49, -21.11) * mm, "end": v(-35.05, -20.85) * mm});
            skLineSegment(sketch, "E327", {"start": v(-35.05, -20.85) * mm, "end": v(-34.6, -20.6) * mm});
            skLineSegment(sketch, "E328", {"start": v(-34.6, -20.6) * mm, "end": v(-34.17, -20.33) * mm});
            skLineSegment(sketch, "E329", {"start": v(-34.17, -20.33) * mm, "end": v(-33.8, -20.11) * mm});
            skLineSegment(sketch, "E330", {"start": v(-33.8, -20.11) * mm, "end": v(-33.8, -20.62) * mm});
            skLineSegment(sketch, "E331", {"start": v(-33.8, -20.62) * mm, "end": v(-33.8, -21.14) * mm});
            skLineSegment(sketch, "E332", {"start": v(-33.8, -21.14) * mm, "end": v(-33.82, -21.65) * mm});
            skLineSegment(sketch, "E333", {"start": v(-33.82, -21.65) * mm, "end": v(-33.84, -22.16) * mm});
            skLineSegment(sketch, "E334", {"start": v(-33.84, -22.16) * mm, "end": v(-33.88, -22.67) * mm});
            skLineSegment(sketch, "E335", {"start": v(-33.88, -22.67) * mm, "end": v(-33.93, -23.18) * mm});
            skLineSegment(sketch, "E336", {"start": v(-33.93, -23.18) * mm, "end": v(-34, -23.68) * mm});
            skLineSegment(sketch, "E337", {"start": v(-34, -23.68) * mm, "end": v(-34.06, -24.19) * mm});
            skLineSegment(sketch, "E338", {"start": v(-34.06, -24.19) * mm, "end": v(-34.15, -24.7) * mm});
            skLineSegment(sketch, "E339", {"start": v(-34.15, -24.7) * mm, "end": v(-34.25, -25.2) * mm});
            skLineSegment(sketch, "E340", {"start": v(-34.25, -25.2) * mm, "end": v(-34.37, -25.7) * mm});
            skLineSegment(sketch, "E341", {"start": v(-34.37, -25.7) * mm, "end": v(-34.48, -26.19) * mm});
            skLineSegment(sketch, "E342", {"start": v(-34.48, -26.19) * mm, "end": v(-34.62, -26.68) * mm});
            skLineSegment(sketch, "E343", {"start": v(-34.62, -26.68) * mm, "end": v(-34.77, -27.17) * mm});
            skLineSegment(sketch, "E344", {"start": v(-34.77, -27.17) * mm, "end": v(-34.93, -27.66) * mm});
            skLineSegment(sketch, "E345", {"start": v(-34.93, -27.66) * mm, "end": v(-35.1, -28.14) * mm});
            skLineSegment(sketch, "E346", {"start": v(-35.1, -28.14) * mm, "end": v(-35.27, -28.62) * mm});
            skLineSegment(sketch, "E347", {"start": v(-35.27, -28.62) * mm, "end": v(-35.47, -29.1) * mm});
            skLineSegment(sketch, "E348", {"start": v(-35.47, -29.1) * mm, "end": v(-35.68, -29.56) * mm});
            skLineSegment(sketch, "E349", {"start": v(-35.68, -29.56) * mm, "end": v(-35.88, -30.02) * mm});
            skLineSegment(sketch, "E350", {"start": v(-35.88, -30.02) * mm, "end": v(-36.11, -30.48) * mm});
            skLineSegment(sketch, "E351", {"start": v(-36.11, -30.48) * mm, "end": v(-36.35, -30.93) * mm});
            skLineSegment(sketch, "E352", {"start": v(-36.35, -30.93) * mm, "end": v(-36.6, -31.38) * mm});
            skLineSegment(sketch, "E353", {"start": v(-36.6, -31.38) * mm, "end": v(-36.85, -31.82) * mm});
            skLineSegment(sketch, "E354", {"start": v(-36.85, -31.82) * mm, "end": v(-37.12, -32.26) * mm});
            skLineSegment(sketch, "E355", {"start": v(-37.12, -32.26) * mm, "end": v(-37.4, -32.68) * mm});
            skLineSegment(sketch, "E356", {"start": v(-37.4, -32.68) * mm, "end": v(-37.6, -32.97) * mm});
            skLineSegment(sketch, "E357", {"start": v(-37.6, -32.97) * mm, "end": v(-37.25, -33.35) * mm});
            skLineSegment(sketch, "E358", {"start": v(-37.25, -33.35) * mm, "end": v(-36.9, -33.73) * mm});
            skLineSegment(sketch, "E359", {"start": v(-36.9, -33.73) * mm, "end": v(-36.72, -33.94) * mm});
            skLineSegment(sketch, "E360", {"start": v(-36.72, -33.94) * mm, "end": v(-36.34, -33.6) * mm});
            skLineSegment(sketch, "E361", {"start": v(-36.34, -33.6) * mm, "end": v(-35.96, -33.24) * mm});
            skLineSegment(sketch, "E362", {"start": v(-35.96, -33.24) * mm, "end": v(-35.59, -32.9) * mm});
            skLineSegment(sketch, "E363", {"start": v(-35.59, -32.9) * mm, "end": v(-35.21, -32.55) * mm});
            skLineSegment(sketch, "E364", {"start": v(-35.21, -32.55) * mm, "end": v(-34.84, -32.2) * mm});
            skLineSegment(sketch, "E365", {"start": v(-34.84, -32.2) * mm, "end": v(-34.46, -31.85) * mm});
            skLineSegment(sketch, "E366", {"start": v(-34.46, -31.85) * mm, "end": v(-34.08, -31.5) * mm});
            skLineSegment(sketch, "E367", {"start": v(-34.08, -31.5) * mm, "end": v(-33.7, -31.16) * mm});
            skLineSegment(sketch, "E368", {"start": v(-33.7, -31.16) * mm, "end": v(-33.33, -30.81) * mm});
            skLineSegment(sketch, "E369", {"start": v(-33.33, -30.81) * mm, "end": v(-32.96, -30.46) * mm});
            skLineSegment(sketch, "E370", {"start": v(-32.96, -30.46) * mm, "end": v(-32.58, -30.12) * mm});
            skLineSegment(sketch, "E371", {"start": v(-32.58, -30.12) * mm, "end": v(-32.2, -29.77) * mm});
            skLineSegment(sketch, "E372", {"start": v(-32.2, -29.77) * mm, "end": v(-31.83, -29.42) * mm});
            skLineSegment(sketch, "E373", {"start": v(-31.83, -29.42) * mm, "end": v(-31.45, -29.07) * mm});
            skLineSegment(sketch, "E374", {"start": v(-31.45, -29.07) * mm, "end": v(-31.08, -28.73) * mm});
            skLineSegment(sketch, "E375", {"start": v(-31.08, -28.73) * mm, "end": v(-30.7, -28.38) * mm});
            skLineSegment(sketch, "E376", {"start": v(-30.7, -28.38) * mm, "end": v(-30.32, -28.03) * mm});
            skLineSegment(sketch, "E377", {"start": v(-30.32, -28.03) * mm, "end": v(-29.95, -27.68) * mm});
            skLineSegment(sketch, "E378", {"start": v(-29.95, -27.68) * mm, "end": v(-29.57, -27.34) * mm});
            skLineSegment(sketch, "E379", {"start": v(-29.57, -27.34) * mm, "end": v(-29.2, -26.99) * mm});
            skLineSegment(sketch, "E380", {"start": v(-29.2, -26.99) * mm, "end": v(-28.89, -26.7) * mm});
            skLineSegment(sketch, "E381", {"start": v(-28.89, -26.7) * mm, "end": v(-28.77, -27.2) * mm});
            skLineSegment(sketch, "E382", {"start": v(-28.77, -27.2) * mm, "end": v(-28.67, -27.7) * mm});
            skLineSegment(sketch, "E383", {"start": v(-28.67, -27.7) * mm, "end": v(-28.58, -28.2) * mm});
            skLineSegment(sketch, "E384", {"start": v(-28.58, -28.2) * mm, "end": v(-28.5, -28.7) * mm});
            skLineSegment(sketch, "E385", {"start": v(-28.5, -28.7) * mm, "end": v(-28.42, -29.22) * mm});
            skLineSegment(sketch, "E386", {"start": v(-28.42, -29.22) * mm, "end": v(-28.37, -29.72) * mm});
            skLineSegment(sketch, "E387", {"start": v(-28.37, -29.72) * mm, "end": v(-28.33, -30.23) * mm});
            skLineSegment(sketch, "E388", {"start": v(-28.33, -30.23) * mm, "end": v(-28.29, -30.74) * mm});
            skLineSegment(sketch, "E389", {"start": v(-28.29, -30.74) * mm, "end": v(-28.27, -31.25) * mm});
            skLineSegment(sketch, "E390", {"start": v(-28.27, -31.25) * mm, "end": v(-28.27, -31.77) * mm});
            skLineSegment(sketch, "E391", {"start": v(-28.27, -31.77) * mm, "end": v(-28.27, -32.28) * mm});
            skLineSegment(sketch, "E392", {"start": v(-28.27, -32.28) * mm, "end": v(-28.28, -32.79) * mm});
            skLineSegment(sketch, "E393", {"start": v(-28.28, -32.79) * mm, "end": v(-28.31, -33.3) * mm});
            skLineSegment(sketch, "E394", {"start": v(-28.31, -33.3) * mm, "end": v(-28.36, -33.8) * mm});
            skLineSegment(sketch, "E395", {"start": v(-28.36, -33.8) * mm, "end": v(-28.42, -34.32) * mm});
            skLineSegment(sketch, "E396", {"start": v(-28.42, -34.32) * mm, "end": v(-28.47, -34.82) * mm});
            skLineSegment(sketch, "E397", {"start": v(-28.47, -34.82) * mm, "end": v(-28.55, -35.33) * mm});
            skLineSegment(sketch, "E398", {"start": v(-28.55, -35.33) * mm, "end": v(-28.65, -35.83) * mm});
            skLineSegment(sketch, "E399", {"start": v(-28.65, -35.83) * mm, "end": v(-28.75, -36.33) * mm});
            skLineSegment(sketch, "E400", {"start": v(-28.75, -36.33) * mm, "end": v(-28.86, -36.83) * mm});
            skLineSegment(sketch, "E401", {"start": v(-28.86, -36.83) * mm, "end": v(-28.98, -37.32) * mm});
            skLineSegment(sketch, "E402", {"start": v(-28.98, -37.32) * mm, "end": v(-29.12, -37.82) * mm});
            skLineSegment(sketch, "E403", {"start": v(-29.12, -37.82) * mm, "end": v(-29.28, -38.3) * mm});
            skLineSegment(sketch, "E404", {"start": v(-29.28, -38.3) * mm, "end": v(-29.43, -38.79) * mm});
            skLineSegment(sketch, "E405", {"start": v(-29.43, -38.79) * mm, "end": v(-29.6, -39.27) * mm});
            skLineSegment(sketch, "E406", {"start": v(-29.6, -39.27) * mm, "end": v(-29.8, -39.75) * mm});
            skLineSegment(sketch, "E407", {"start": v(-29.8, -39.75) * mm, "end": v(-29.92, -40.06) * mm});
            skLineSegment(sketch, "E408", {"start": v(-29.92, -40.06) * mm, "end": v(-29.5, -40.36) * mm});
            skLineSegment(sketch, "E409", {"start": v(-29.5, -40.36) * mm, "end": v(-29.09, -40.66) * mm});
            skLineSegment(sketch, "E410", {"start": v(-29.09, -40.66) * mm, "end": v(-28.86, -40.83) * mm});
            skLineSegment(sketch, "E411", {"start": v(-28.86, -40.83) * mm, "end": v(-28.56, -40.41) * mm});
            skLineSegment(sketch, "E412", {"start": v(-28.56, -40.41) * mm, "end": v(-28.27, -40) * mm});
            skLineSegment(sketch, "E413", {"start": v(-28.27, -40) * mm, "end": v(-27.97, -39.58) * mm});
            skLineSegment(sketch, "E414", {"start": v(-27.97, -39.58) * mm, "end": v(-27.68, -39.16) * mm});
            skLineSegment(sketch, "E415", {"start": v(-27.68, -39.16) * mm, "end": v(-27.38, -38.74) * mm});
            skLineSegment(sketch, "E416", {"start": v(-27.38, -38.74) * mm, "end": v(-27.08, -38.32) * mm});
            skLineSegment(sketch, "E417", {"start": v(-27.08, -38.32) * mm, "end": v(-26.79, -37.9) * mm});
            skLineSegment(sketch, "E418", {"start": v(-26.79, -37.9) * mm, "end": v(-26.5, -37.49) * mm});
            skLineSegment(sketch, "E419", {"start": v(-26.5, -37.49) * mm, "end": v(-26.2, -37.07) * mm});
            skLineSegment(sketch, "E420", {"start": v(-26.2, -37.07) * mm, "end": v(-25.9, -36.65) * mm});
            skLineSegment(sketch, "E421", {"start": v(-25.9, -36.65) * mm, "end": v(-25.6, -36.23) * mm});
            skLineSegment(sketch, "E422", {"start": v(-25.6, -36.23) * mm, "end": v(-25.31, -35.81) * mm});
            skLineSegment(sketch, "E423", {"start": v(-25.31, -35.81) * mm, "end": v(-25.02, -35.4) * mm});
            skLineSegment(sketch, "E424", {"start": v(-25.02, -35.4) * mm, "end": v(-24.72, -34.98) * mm});
            skLineSegment(sketch, "E425", {"start": v(-24.72, -34.98) * mm, "end": v(-24.42, -34.56) * mm});
            skLineSegment(sketch, "E426", {"start": v(-24.42, -34.56) * mm, "end": v(-24.13, -34.14) * mm});
            skLineSegment(sketch, "E427", {"start": v(-24.13, -34.14) * mm, "end": v(-23.83, -33.72) * mm});
            skLineSegment(sketch, "E428", {"start": v(-23.83, -33.72) * mm, "end": v(-23.54, -33.3) * mm});
            skLineSegment(sketch, "E429", {"start": v(-23.54, -33.3) * mm, "end": v(-23.24, -32.89) * mm});
            skLineSegment(sketch, "E430", {"start": v(-23.24, -32.89) * mm, "end": v(-22.95, -32.47) * mm});
            skLineSegment(sketch, "E431", {"start": v(-22.95, -32.47) * mm, "end": v(-22.7, -32.12) * mm});
            skLineSegment(sketch, "E432", {"start": v(-22.7, -32.12) * mm, "end": v(-22.49, -32.59) * mm});
            skLineSegment(sketch, "E433", {"start": v(-22.49, -32.59) * mm, "end": v(-22.28, -33.06) * mm});
            skLineSegment(sketch, "E434", {"start": v(-22.28, -33.06) * mm, "end": v(-22.1, -33.53) * mm});
            skLineSegment(sketch, "E435", {"start": v(-22.1, -33.53) * mm, "end": v(-21.9, -34) * mm});
            skLineSegment(sketch, "E436", {"start": v(-21.9, -34) * mm, "end": v(-21.73, -34.49) * mm});
            skLineSegment(sketch, "E437", {"start": v(-21.73, -34.49) * mm, "end": v(-21.57, -34.97) * mm});
            skLineSegment(sketch, "E438", {"start": v(-21.57, -34.97) * mm, "end": v(-21.42, -35.46) * mm});
            skLineSegment(sketch, "E439", {"start": v(-21.42, -35.46) * mm, "end": v(-21.28, -35.95) * mm});
            skLineSegment(sketch, "E440", {"start": v(-21.28, -35.95) * mm, "end": v(-21.16, -36.45) * mm});
            skLineSegment(sketch, "E441", {"start": v(-21.16, -36.45) * mm, "end": v(-21.04, -36.95) * mm});
            skLineSegment(sketch, "E442", {"start": v(-21.04, -36.95) * mm, "end": v(-20.95, -37.45) * mm});
            skLineSegment(sketch, "E443", {"start": v(-20.95, -37.45) * mm, "end": v(-20.85, -37.95) * mm});
            skLineSegment(sketch, "E444", {"start": v(-20.85, -37.95) * mm, "end": v(-20.77, -38.46) * mm});
            skLineSegment(sketch, "E445", {"start": v(-20.77, -38.46) * mm, "end": v(-20.71, -38.96) * mm});
            skLineSegment(sketch, "E446", {"start": v(-20.71, -38.96) * mm, "end": v(-20.66, -39.47) * mm});
            skLineSegment(sketch, "E447", {"start": v(-20.66, -39.47) * mm, "end": v(-20.61, -39.98) * mm});
            skLineSegment(sketch, "E448", {"start": v(-20.61, -39.98) * mm, "end": v(-20.58, -40.5) * mm});
            skLineSegment(sketch, "E449", {"start": v(-20.58, -40.5) * mm, "end": v(-20.57, -41) * mm});
            skLineSegment(sketch, "E450", {"start": v(-20.57, -41) * mm, "end": v(-20.57, -41.51) * mm});
            skLineSegment(sketch, "E451", {"start": v(-20.57, -41.51) * mm, "end": v(-20.57, -42.02) * mm});
            skLineSegment(sketch, "E452", {"start": v(-20.57, -42.02) * mm, "end": v(-20.6, -42.53) * mm});
            skLineSegment(sketch, "E453", {"start": v(-20.6, -42.53) * mm, "end": v(-20.63, -43.04) * mm});
            skLineSegment(sketch, "E454", {"start": v(-20.63, -43.04) * mm, "end": v(-20.67, -43.55) * mm});
            skLineSegment(sketch, "E455", {"start": v(-20.67, -43.55) * mm, "end": v(-20.72, -44.06) * mm});
            skLineSegment(sketch, "E456", {"start": v(-20.72, -44.06) * mm, "end": v(-20.8, -44.57) * mm});
            skLineSegment(sketch, "E457", {"start": v(-20.8, -44.57) * mm, "end": v(-20.88, -45.07) * mm});
            skLineSegment(sketch, "E458", {"start": v(-20.88, -45.07) * mm, "end": v(-20.93, -45.4) * mm});
            skLineSegment(sketch, "E459", {"start": v(-20.93, -45.4) * mm, "end": v(-20.47, -45.62) * mm});
            skLineSegment(sketch, "E460", {"start": v(-20.47, -45.62) * mm, "end": v(-20, -45.82) * mm});
            skLineSegment(sketch, "E461", {"start": v(-20, -45.82) * mm, "end": v(-19.74, -45.94) * mm});
            skLineSegment(sketch, "E462", {"start": v(-19.74, -45.94) * mm, "end": v(-19.54, -45.47) * mm});
            skLineSegment(sketch, "E463", {"start": v(-19.54, -45.47) * mm, "end": v(-19.33, -45) * mm});
            skLineSegment(sketch, "E464", {"start": v(-19.33, -45) * mm, "end": v(-19.13, -44.53) * mm});
            skLineSegment(sketch, "E465", {"start": v(-19.13, -44.53) * mm, "end": v(-18.93, -44.06) * mm});
            skLineSegment(sketch, "E466", {"start": v(-18.93, -44.06) * mm, "end": v(-18.73, -43.59) * mm});
            skLineSegment(sketch, "E467", {"start": v(-18.73, -43.59) * mm, "end": v(-18.52, -43.12) * mm});
            skLineSegment(sketch, "E468", {"start": v(-18.52, -43.12) * mm, "end": v(-18.32, -42.65) * mm});
            skLineSegment(sketch, "E469", {"start": v(-18.32, -42.65) * mm, "end": v(-18.12, -42.18) * mm});
            skLineSegment(sketch, "E470", {"start": v(-18.12, -42.18) * mm, "end": v(-17.92, -41.7) * mm});
            skLineSegment(sketch, "E471", {"start": v(-17.92, -41.7) * mm, "end": v(-17.72, -41.23) * mm});
            skLineSegment(sketch, "E472", {"start": v(-17.72, -41.23) * mm, "end": v(-17.51, -40.76) * mm});
            skLineSegment(sketch, "E473", {"start": v(-17.51, -40.76) * mm, "end": v(-17.31, -40.3) * mm});
            skLineSegment(sketch, "E474", {"start": v(-17.31, -40.3) * mm, "end": v(-17.1, -39.82) * mm});
            skLineSegment(sketch, "E475", {"start": v(-17.1, -39.82) * mm, "end": v(-16.9, -39.35) * mm});
            skLineSegment(sketch, "E476", {"start": v(-16.9, -39.35) * mm, "end": v(-16.7, -38.88) * mm});
            skLineSegment(sketch, "E477", {"start": v(-16.7, -38.88) * mm, "end": v(-16.5, -38.41) * mm});
            skLineSegment(sketch, "E478", {"start": v(-16.5, -38.41) * mm, "end": v(-16.3, -37.94) * mm});
            skLineSegment(sketch, "E479", {"start": v(-16.3, -37.94) * mm, "end": v(-16.1, -37.47) * mm});
            skLineSegment(sketch, "E480", {"start": v(-16.1, -37.47) * mm, "end": v(-15.9, -37) * mm});
            skLineSegment(sketch, "E481", {"start": v(-15.9, -37) * mm, "end": v(-15.7, -36.53) * mm});
            skLineSegment(sketch, "E482", {"start": v(-15.7, -36.53) * mm, "end": v(-15.53, -36.14) * mm});
            skLineSegment(sketch, "E483", {"start": v(-15.53, -36.14) * mm, "end": v(-15.22, -36.55) * mm});
            skLineSegment(sketch, "E484", {"start": v(-15.22, -36.55) * mm, "end": v(-14.92, -36.97) * mm});
            skLineSegment(sketch, "E485", {"start": v(-14.92, -36.97) * mm, "end": v(-14.64, -37.4) * mm});
            skLineSegment(sketch, "E486", {"start": v(-14.64, -37.4) * mm, "end": v(-14.35, -37.81) * mm});
            skLineSegment(sketch, "E487", {"start": v(-14.35, -37.81) * mm, "end": v(-14.08, -38.25) * mm});
            skLineSegment(sketch, "E488", {"start": v(-14.08, -38.25) * mm, "end": v(-13.83, -38.7) * mm});
            skLineSegment(sketch, "E489", {"start": v(-13.83, -38.7) * mm, "end": v(-13.58, -39.14) * mm});
            skLineSegment(sketch, "E490", {"start": v(-13.58, -39.14) * mm, "end": v(-13.34, -39.59) * mm});
            skLineSegment(sketch, "E491", {"start": v(-13.34, -39.59) * mm, "end": v(-13.12, -40.05) * mm});
            skLineSegment(sketch, "E492", {"start": v(-13.12, -40.05) * mm, "end": v(-12.9, -40.52) * mm});
            skLineSegment(sketch, "E493", {"start": v(-12.9, -40.52) * mm, "end": v(-12.7, -40.99) * mm});
            skLineSegment(sketch, "E494", {"start": v(-12.7, -40.99) * mm, "end": v(-12.5, -41.45) * mm});
            skLineSegment(sketch, "E495", {"start": v(-12.5, -41.45) * mm, "end": v(-12.32, -41.93) * mm});
            skLineSegment(sketch, "E496", {"start": v(-12.32, -41.93) * mm, "end": v(-12.16, -42.42) * mm});
            skLineSegment(sketch, "E497", {"start": v(-12.16, -42.42) * mm, "end": v(-12, -42.9) * mm});
            skLineSegment(sketch, "E498", {"start": v(-12, -42.9) * mm, "end": v(-11.85, -43.4) * mm});
            skLineSegment(sketch, "E499", {"start": v(-11.85, -43.4) * mm, "end": v(-11.72, -43.89) * mm});
            skLineSegment(sketch, "E500", {"start": v(-11.72, -43.89) * mm, "end": v(-11.6, -44.38) * mm});
            skLineSegment(sketch, "E501", {"start": v(-11.6, -44.38) * mm, "end": v(-11.49, -44.88) * mm});
            skLineSegment(sketch, "E502", {"start": v(-11.49, -44.88) * mm, "end": v(-11.38, -45.38) * mm});
            skLineSegment(sketch, "E503", {"start": v(-11.38, -45.38) * mm, "end": v(-11.3, -45.89) * mm});
            skLineSegment(sketch, "E504", {"start": v(-11.3, -45.89) * mm, "end": v(-11.23, -46.4) * mm});
            skLineSegment(sketch, "E505", {"start": v(-11.23, -46.4) * mm, "end": v(-11.17, -46.9) * mm});
            skLineSegment(sketch, "E506", {"start": v(-11.17, -46.9) * mm, "end": v(-11.1, -47.4) * mm});
            skLineSegment(sketch, "E507", {"start": v(-11.1, -47.4) * mm, "end": v(-11.07, -47.92) * mm});
            skLineSegment(sketch, "E508", {"start": v(-11.07, -47.92) * mm, "end": v(-11.05, -48.43) * mm});
            skLineSegment(sketch, "E509", {"start": v(-11.05, -48.43) * mm, "end": v(-11.03, -48.77) * mm});
            skLineSegment(sketch, "E510", {"start": v(-11.03, -48.77) * mm, "end": v(-10.53, -48.87) * mm});
            skLineSegment(sketch, "E511", {"start": v(-10.53, -48.87) * mm, "end": v(-10.03, -48.98) * mm});
            skLineSegment(sketch, "E512", {"start": v(-10.03, -48.98) * mm, "end": v(-9.75, -49.04) * mm});
            skLineSegment(sketch, "E513", {"start": v(-9.75, -49.04) * mm, "end": v(-9.65, -48.54) * mm});
            skLineSegment(sketch, "E514", {"start": v(-9.65, -48.54) * mm, "end": v(-9.55, -48.03) * mm});
            skLineSegment(sketch, "E515", {"start": v(-9.55, -48.03) * mm, "end": v(-9.45, -47.53) * mm});
            skLineSegment(sketch, "E516", {"start": v(-9.45, -47.53) * mm, "end": v(-9.35, -47.03) * mm});
            skLineSegment(sketch, "E517", {"start": v(-9.35, -47.03) * mm, "end": v(-9.26, -46.53) * mm});
            skLineSegment(sketch, "E518", {"start": v(-9.26, -46.53) * mm, "end": v(-9.16, -46.03) * mm});
            skLineSegment(sketch, "E519", {"start": v(-9.16, -46.03) * mm, "end": v(-9.06, -45.52) * mm});
            skLineSegment(sketch, "E520", {"start": v(-9.06, -45.52) * mm, "end": v(-8.96, -45.02) * mm});
            skLineSegment(sketch, "E521", {"start": v(-8.96, -45.02) * mm, "end": v(-8.86, -44.52) * mm});
            skLineSegment(sketch, "E522", {"start": v(-8.86, -44.52) * mm, "end": v(-8.76, -44.02) * mm});
            skLineSegment(sketch, "E523", {"start": v(-8.76, -44.02) * mm, "end": v(-8.66, -43.52) * mm});
            skLineSegment(sketch, "E524", {"start": v(-8.66, -43.52) * mm, "end": v(-8.56, -43.01) * mm});
            skLineSegment(sketch, "E525", {"start": v(-8.56, -43.01) * mm, "end": v(-8.46, -42.51) * mm});
            skLineSegment(sketch, "E526", {"start": v(-8.46, -42.51) * mm, "end": v(-8.36, -42) * mm});
            skLineSegment(sketch, "E527", {"start": v(-8.36, -42) * mm, "end": v(-8.26, -41.5) * mm});
            skLineSegment(sketch, "E528", {"start": v(-8.26, -41.5) * mm, "end": v(-8.16, -41) * mm});
            skLineSegment(sketch, "E529", {"start": v(-8.16, -41) * mm, "end": v(-8.06, -40.5) * mm});
            skLineSegment(sketch, "E530", {"start": v(-8.06, -40.5) * mm, "end": v(-7.96, -40) * mm});
            skLineSegment(sketch, "E531", {"start": v(-7.96, -40) * mm, "end": v(-7.86, -39.5) * mm});
            skLineSegment(sketch, "E532", {"start": v(-7.86, -39.5) * mm, "end": v(-7.76, -39) * mm});
            skLineSegment(sketch, "E533", {"start": v(-7.76, -39) * mm, "end": v(-7.67, -38.58) * mm});
            skLineSegment(sketch, "E534", {"start": v(-7.67, -38.58) * mm, "end": v(-7.29, -38.92) * mm});
            skLineSegment(sketch, "E535", {"start": v(-7.29, -38.92) * mm, "end": v(-6.91, -39.26) * mm});
            skLineSegment(sketch, "E536", {"start": v(-6.91, -39.26) * mm, "end": v(-6.54, -39.62) * mm});
            skLineSegment(sketch, "E537", {"start": v(-6.54, -39.62) * mm, "end": v(-6.18, -39.97) * mm});
            skLineSegment(sketch, "E538", {"start": v(-6.18, -39.97) * mm, "end": v(-5.82, -40.34) * mm});
            skLineSegment(sketch, "E539", {"start": v(-5.82, -40.34) * mm, "end": v(-5.48, -40.72) * mm});
            skLineSegment(sketch, "E540", {"start": v(-5.48, -40.72) * mm, "end": v(-5.15, -41.11) * mm});
            skLineSegment(sketch, "E541", {"start": v(-5.15, -41.11) * mm, "end": v(-4.82, -41.5) * mm});
            skLineSegment(sketch, "E542", {"start": v(-4.82, -41.5) * mm, "end": v(-4.5, -41.9) * mm});
            skLineSegment(sketch, "E543", {"start": v(-4.5, -41.9) * mm, "end": v(-4.2, -42.31) * mm});
            skLineSegment(sketch, "E544", {"start": v(-4.2, -42.31) * mm, "end": v(-3.9, -42.73) * mm});
            skLineSegment(sketch, "E545", {"start": v(-3.9, -42.73) * mm, "end": v(-3.61, -43.15) * mm});
            skLineSegment(sketch, "E546", {"start": v(-3.61, -43.15) * mm, "end": v(-3.34, -43.58) * mm});
            skLineSegment(sketch, "E547", {"start": v(-3.34, -43.58) * mm, "end": v(-3.07, -44.02) * mm});
            skLineSegment(sketch, "E548", {"start": v(-3.07, -44.02) * mm, "end": v(-2.82, -44.46) * mm});
            skLineSegment(sketch, "E549", {"start": v(-2.82, -44.46) * mm, "end": v(-2.57, -44.9) * mm});
            skLineSegment(sketch, "E550", {"start": v(-2.57, -44.9) * mm, "end": v(-2.34, -45.36) * mm});
            skLineSegment(sketch, "E551", {"start": v(-2.34, -45.36) * mm, "end": v(-2.11, -45.82) * mm});
            skLineSegment(sketch, "E552", {"start": v(-2.11, -45.82) * mm, "end": v(-1.9, -46.3) * mm});
            skLineSegment(sketch, "E553", {"start": v(-1.9, -46.3) * mm, "end": v(-1.7, -46.76) * mm});
            skLineSegment(sketch, "E554", {"start": v(-1.7, -46.76) * mm, "end": v(-1.51, -47.23) * mm});
            skLineSegment(sketch, "E555", {"start": v(-1.51, -47.23) * mm, "end": v(-1.33, -47.71) * mm});
            skLineSegment(sketch, "E556", {"start": v(-1.33, -47.71) * mm, "end": v(-1.17, -48.2) * mm});
            skLineSegment(sketch, "E557", {"start": v(-1.17, -48.2) * mm, "end": v(-1, -48.68) * mm});
            skLineSegment(sketch, "E558", {"start": v(-1, -48.68) * mm, "end": v(-0.87, -49.17) * mm});
            skLineSegment(sketch, "E559", {"start": v(-0.87, -49.17) * mm, "end": v(-0.74, -49.67) * mm});
            skLineSegment(sketch, "E560", {"start": v(-0.74, -49.67) * mm, "end": v(-0.65, -50) * mm});
            skLineSegment(sketch, "E561", {"start": v(-0.65, -50) * mm, "end": v(-0.14, -50) * mm});
            skLineSegment(sketch, "E562", {"start": v(-0.14, -50) * mm, "end": v(0.37, -50) * mm});
            skLineSegment(sketch, "E563", {"start": v(0.37, -50) * mm, "end": v(0.65, -50) * mm});
            skLineSegment(sketch, "E564", {"start": v(0.65, -50) * mm, "end": v(0.65, -49.48) * mm});
            skLineSegment(sketch, "E565", {"start": v(0.65, -49.48) * mm, "end": v(0.64, -48.97) * mm});
            skLineSegment(sketch, "E566", {"start": v(0.64, -48.97) * mm, "end": v(0.63, -48.46) * mm});
            skLineSegment(sketch, "E567", {"start": v(0.63, -48.46) * mm, "end": v(0.63, -47.95) * mm});
            skLineSegment(sketch, "E568", {"start": v(0.63, -47.95) * mm, "end": v(0.62, -47.44) * mm});
            skLineSegment(sketch, "E569", {"start": v(0.62, -47.44) * mm, "end": v(0.61, -46.92) * mm});
            skLineSegment(sketch, "E570", {"start": v(0.61, -46.92) * mm, "end": v(0.6, -46.41) * mm});
            skLineSegment(sketch, "E571", {"start": v(0.6, -46.41) * mm, "end": v(0.6, -45.9) * mm});
            skLineSegment(sketch, "E572", {"start": v(0.6, -45.9) * mm, "end": v(0.6, -45.39) * mm});
            skLineSegment(sketch, "E573", {"start": v(0.6, -45.39) * mm, "end": v(0.59, -44.88) * mm});
            skLineSegment(sketch, "E574", {"start": v(0.59, -44.88) * mm, "end": v(0.58, -44.36) * mm});
            skLineSegment(sketch, "E575", {"start": v(0.58, -44.36) * mm, "end": v(0.57, -43.85) * mm});
            skLineSegment(sketch, "E576", {"start": v(0.57, -43.85) * mm, "end": v(0.57, -43.34) * mm});
            skLineSegment(sketch, "E577", {"start": v(0.57, -43.34) * mm, "end": v(0.56, -42.83) * mm});
            skLineSegment(sketch, "E578", {"start": v(0.56, -42.83) * mm, "end": v(0.55, -42.32) * mm});
            skLineSegment(sketch, "E579", {"start": v(0.55, -42.32) * mm, "end": v(0.55, -41.8) * mm});
            skLineSegment(sketch, "E580", {"start": v(0.55, -41.8) * mm, "end": v(0.54, -41.3) * mm});
            skLineSegment(sketch, "E581", {"start": v(0.54, -41.3) * mm, "end": v(0.53, -40.78) * mm});
            skLineSegment(sketch, "E582", {"start": v(0.53, -40.78) * mm, "end": v(0.53, -40.27) * mm});
            skLineSegment(sketch, "E583", {"start": v(0.53, -40.27) * mm, "end": v(0.52, -39.76) * mm});
            skLineSegment(sketch, "E584", {"start": v(0.52, -39.76) * mm, "end": v(0.51, -39.33) * mm});
            skLineSegment(sketch, "E585", {"start": v(0.51, -39.33) * mm, "end": v(0.96, -39.58) * mm});
            skLineSegment(sketch, "E586", {"start": v(0.96, -39.58) * mm, "end": v(1.4, -39.84) * mm});
            skLineSegment(sketch, "E587", {"start": v(1.4, -39.84) * mm, "end": v(1.84, -40.11) * mm});
            skLineSegment(sketch, "E588", {"start": v(1.84, -40.11) * mm, "end": v(2.27, -40.38) * mm});
            skLineSegment(sketch, "E589", {"start": v(2.27, -40.38) * mm, "end": v(2.7, -40.67) * mm});
            skLineSegment(sketch, "E590", {"start": v(2.7, -40.67) * mm, "end": v(3.1, -40.97) * mm});
            skLineSegment(sketch, "E591", {"start": v(3.1, -40.97) * mm, "end": v(3.51, -41.28) * mm});
            skLineSegment(sketch, "E592", {"start": v(3.51, -41.28) * mm, "end": v(3.92, -41.6) * mm});
            skLineSegment(sketch, "E593", {"start": v(3.92, -41.6) * mm, "end": v(4.3, -41.92) * mm});
            skLineSegment(sketch, "E594", {"start": v(4.3, -41.92) * mm, "end": v(4.7, -42.26) * mm});
            skLineSegment(sketch, "E595", {"start": v(4.7, -42.26) * mm, "end": v(5.07, -42.6) * mm});
            skLineSegment(sketch, "E596", {"start": v(5.07, -42.6) * mm, "end": v(5.44, -42.96) * mm});
            skLineSegment(sketch, "E597", {"start": v(5.44, -42.96) * mm, "end": v(5.8, -43.32) * mm});
            skLineSegment(sketch, "E598", {"start": v(5.8, -43.32) * mm, "end": v(6.15, -43.7) * mm});
            skLineSegment(sketch, "E599", {"start": v(6.15, -43.7) * mm, "end": v(6.49, -44.08) * mm});
            skLineSegment(sketch, "E600", {"start": v(6.49, -44.08) * mm, "end": v(6.82, -44.46) * mm});
            skLineSegment(sketch, "E601", {"start": v(6.82, -44.46) * mm, "end": v(7.15, -44.86) * mm});
            skLineSegment(sketch, "E602", {"start": v(7.15, -44.86) * mm, "end": v(7.46, -45.26) * mm});
            skLineSegment(sketch, "E603", {"start": v(7.46, -45.26) * mm, "end": v(7.76, -45.68) * mm});
            skLineSegment(sketch, "E604", {"start": v(7.76, -45.68) * mm, "end": v(8.06, -46.09) * mm});
            skLineSegment(sketch, "E605", {"start": v(8.06, -46.09) * mm, "end": v(8.34, -46.51) * mm});
            skLineSegment(sketch, "E606", {"start": v(8.34, -46.51) * mm, "end": v(8.61, -46.95) * mm});
            skLineSegment(sketch, "E607", {"start": v(8.61, -46.95) * mm, "end": v(8.87, -47.39) * mm});
            skLineSegment(sketch, "E608", {"start": v(8.87, -47.39) * mm, "end": v(9.13, -47.83) * mm});
            skLineSegment(sketch, "E609", {"start": v(9.13, -47.83) * mm, "end": v(9.37, -48.28) * mm});
            skLineSegment(sketch, "E610", {"start": v(9.37, -48.28) * mm, "end": v(9.6, -48.74) * mm});
            skLineSegment(sketch, "E611", {"start": v(9.6, -48.74) * mm, "end": v(9.75, -49.04) * mm});
            skLineSegment(sketch, "E612", {"start": v(9.75, -49.04) * mm, "end": v(10.26, -48.93) * mm});
            skLineSegment(sketch, "E613", {"start": v(10.26, -48.93) * mm, "end": v(10.76, -48.83) * mm});
            skLineSegment(sketch, "E614", {"start": v(10.76, -48.83) * mm, "end": v(11.03, -48.77) * mm});
            skLineSegment(sketch, "E615", {"start": v(11.03, -48.77) * mm, "end": v(10.92, -48.27) * mm});
            skLineSegment(sketch, "E616", {"start": v(10.92, -48.27) * mm, "end": v(10.8, -47.77) * mm});
            skLineSegment(sketch, "E617", {"start": v(10.8, -47.77) * mm, "end": v(10.7, -47.27) * mm});
            skLineSegment(sketch, "E618", {"start": v(10.7, -47.27) * mm, "end": v(10.58, -46.77) * mm});
            skLineSegment(sketch, "E619", {"start": v(10.58, -46.77) * mm, "end": v(10.47, -46.27) * mm});
            skLineSegment(sketch, "E620", {"start": v(10.47, -46.27) * mm, "end": v(10.36, -45.77) * mm});
            skLineSegment(sketch, "E621", {"start": v(10.36, -45.77) * mm, "end": v(10.24, -45.27) * mm});
            skLineSegment(sketch, "E622", {"start": v(10.24, -45.27) * mm, "end": v(10.13, -44.77) * mm});
            skLineSegment(sketch, "E623", {"start": v(10.13, -44.77) * mm, "end": v(10.02, -44.27) * mm});
            skLineSegment(sketch, "E624", {"start": v(10.02, -44.27) * mm, "end": v(9.9, -43.77) * mm});
            skLineSegment(sketch, "E625", {"start": v(9.9, -43.77) * mm, "end": v(9.8, -43.27) * mm});
            skLineSegment(sketch, "E626", {"start": v(9.8, -43.27) * mm, "end": v(9.68, -42.77) * mm});
            skLineSegment(sketch, "E627", {"start": v(9.68, -42.77) * mm, "end": v(9.57, -42.27) * mm});
            skLineSegment(sketch, "E628", {"start": v(9.57, -42.27) * mm, "end": v(9.45, -41.78) * mm});
            skLineSegment(sketch, "E629", {"start": v(9.45, -41.78) * mm, "end": v(9.34, -41.28) * mm});
            skLineSegment(sketch, "E630", {"start": v(9.34, -41.28) * mm, "end": v(9.23, -40.78) * mm});
            skLineSegment(sketch, "E631", {"start": v(9.23, -40.78) * mm, "end": v(9.11, -40.28) * mm});
            skLineSegment(sketch, "E632", {"start": v(9.11, -40.28) * mm, "end": v(9, -39.78) * mm});
            skLineSegment(sketch, "E633", {"start": v(9, -39.78) * mm, "end": v(8.89, -39.28) * mm});
            skLineSegment(sketch, "E634", {"start": v(8.89, -39.28) * mm, "end": v(8.77, -38.78) * mm});
            skLineSegment(sketch, "E635", {"start": v(8.77, -38.78) * mm, "end": v(8.68, -38.37) * mm});
            skLineSegment(sketch, "E636", {"start": v(8.68, -38.37) * mm, "end": v(9.17, -38.52) * mm});
            skLineSegment(sketch, "E637", {"start": v(9.17, -38.52) * mm, "end": v(9.66, -38.68) * mm});
            skLineSegment(sketch, "E638", {"start": v(9.66, -38.68) * mm, "end": v(10.14, -38.85) * mm});
            skLineSegment(sketch, "E639", {"start": v(10.14, -38.85) * mm, "end": v(10.62, -39.03) * mm});
            skLineSegment(sketch, "E640", {"start": v(10.62, -39.03) * mm, "end": v(11.09, -39.22) * mm});
            skLineSegment(sketch, "E641", {"start": v(11.09, -39.22) * mm, "end": v(11.56, -39.43) * mm});
            skLineSegment(sketch, "E642", {"start": v(11.56, -39.43) * mm, "end": v(12.02, -39.65) * mm});
            skLineSegment(sketch, "E643", {"start": v(12.02, -39.65) * mm, "end": v(12.48, -39.87) * mm});
            skLineSegment(sketch, "E644", {"start": v(12.48, -39.87) * mm, "end": v(12.93, -40.11) * mm});
            skLineSegment(sketch, "E645", {"start": v(12.93, -40.11) * mm, "end": v(13.38, -40.36) * mm});
            skLineSegment(sketch, "E646", {"start": v(13.38, -40.36) * mm, "end": v(13.82, -40.63) * mm});
            skLineSegment(sketch, "E647", {"start": v(13.82, -40.63) * mm, "end": v(14.25, -40.89) * mm});
            skLineSegment(sketch, "E648", {"start": v(14.25, -40.89) * mm, "end": v(14.68, -41.17) * mm});
            skLineSegment(sketch, "E649", {"start": v(14.68, -41.17) * mm, "end": v(15.1, -41.46) * mm});
            skLineSegment(sketch, "E650", {"start": v(15.1, -41.46) * mm, "end": v(15.5, -41.77) * mm});
            skLineSegment(sketch, "E651", {"start": v(15.5, -41.77) * mm, "end": v(15.92, -42.07) * mm});
            skLineSegment(sketch, "E652", {"start": v(15.92, -42.07) * mm, "end": v(16.32, -42.4) * mm});
            skLineSegment(sketch, "E653", {"start": v(16.32, -42.4) * mm, "end": v(16.7, -42.72) * mm});
            skLineSegment(sketch, "E654", {"start": v(16.7, -42.72) * mm, "end": v(17.09, -43.06) * mm});
            skLineSegment(sketch, "E655", {"start": v(17.09, -43.06) * mm, "end": v(17.47, -43.4) * mm});
            skLineSegment(sketch, "E656", {"start": v(17.47, -43.4) * mm, "end": v(17.83, -43.76) * mm});
            skLineSegment(sketch, "E657", {"start": v(17.83, -43.76) * mm, "end": v(18.19, -44.13) * mm});
            skLineSegment(sketch, "E658", {"start": v(18.19, -44.13) * mm, "end": v(18.53, -44.5) * mm});
            skLineSegment(sketch, "E659", {"start": v(18.53, -44.5) * mm, "end": v(18.88, -44.88) * mm});
            skLineSegment(sketch, "E660", {"start": v(18.88, -44.88) * mm, "end": v(19.2, -45.27) * mm});
            skLineSegment(sketch, "E661", {"start": v(19.2, -45.27) * mm, "end": v(19.53, -45.67) * mm});
            skLineSegment(sketch, "E662", {"start": v(19.53, -45.67) * mm, "end": v(19.74, -45.94) * mm});
            skLineSegment(sketch, "E663", {"start": v(19.74, -45.94) * mm, "end": v(20.2, -45.73) * mm});
            skLineSegment(sketch, "E664", {"start": v(20.2, -45.73) * mm, "end": v(20.67, -45.52) * mm});
            skLineSegment(sketch, "E665", {"start": v(20.67, -45.52) * mm, "end": v(20.93, -45.4) * mm});
            skLineSegment(sketch, "E666", {"start": v(20.93, -45.4) * mm, "end": v(20.72, -44.94) * mm});
            skLineSegment(sketch, "E667", {"start": v(20.72, -44.94) * mm, "end": v(20.5, -44.48) * mm});
            skLineSegment(sketch, "E668", {"start": v(20.5, -44.48) * mm, "end": v(20.29, -44.01) * mm});
            skLineSegment(sketch, "E669", {"start": v(20.29, -44.01) * mm, "end": v(20.08, -43.55) * mm});
            skLineSegment(sketch, "E670", {"start": v(20.08, -43.55) * mm, "end": v(19.86, -43.08) * mm});
            skLineSegment(sketch, "E671", {"start": v(19.86, -43.08) * mm, "end": v(19.65, -42.62) * mm});
            skLineSegment(sketch, "E672", {"start": v(19.65, -42.62) * mm, "end": v(19.43, -42.15) * mm});
            skLineSegment(sketch, "E673", {"start": v(19.43, -42.15) * mm, "end": v(19.22, -41.69) * mm});
            skLineSegment(sketch, "E674", {"start": v(19.22, -41.69) * mm, "end": v(19, -41.22) * mm});
            skLineSegment(sketch, "E675", {"start": v(19, -41.22) * mm, "end": v(18.79, -40.76) * mm});
            skLineSegment(sketch, "E676", {"start": v(18.79, -40.76) * mm, "end": v(18.57, -40.3) * mm});
            skLineSegment(sketch, "E677", {"start": v(18.57, -40.3) * mm, "end": v(18.36, -39.83) * mm});
            skLineSegment(sketch, "E678", {"start": v(18.36, -39.83) * mm, "end": v(18.15, -39.36) * mm});
            skLineSegment(sketch, "E679", {"start": v(18.15, -39.36) * mm, "end": v(17.93, -38.9) * mm});
            skLineSegment(sketch, "E680", {"start": v(17.93, -38.9) * mm, "end": v(17.72, -38.43) * mm});
            skLineSegment(sketch, "E681", {"start": v(17.72, -38.43) * mm, "end": v(17.5, -37.97) * mm});
            skLineSegment(sketch, "E682", {"start": v(17.5, -37.97) * mm, "end": v(17.29, -37.5) * mm});
            skLineSegment(sketch, "E683", {"start": v(17.29, -37.5) * mm, "end": v(17.07, -37.04) * mm});
            skLineSegment(sketch, "E684", {"start": v(17.07, -37.04) * mm, "end": v(16.86, -36.57) * mm});
            skLineSegment(sketch, "E685", {"start": v(16.86, -36.57) * mm, "end": v(16.65, -36.1) * mm});
            skLineSegment(sketch, "E686", {"start": v(16.65, -36.1) * mm, "end": v(16.47, -35.72) * mm});
            skLineSegment(sketch, "E687", {"start": v(16.47, -35.72) * mm, "end": v(16.98, -35.77) * mm});
            skLineSegment(sketch, "E688", {"start": v(16.98, -35.77) * mm, "end": v(17.49, -35.83) * mm});
            skLineSegment(sketch, "E689", {"start": v(17.49, -35.83) * mm, "end": v(18, -35.9) * mm});
            skLineSegment(sketch, "E690", {"start": v(18, -35.9) * mm, "end": v(18.5, -35.97) * mm});
            skLineSegment(sketch, "E691", {"start": v(18.5, -35.97) * mm, "end": v(19, -36.06) * mm});
            skLineSegment(sketch, "E692", {"start": v(19, -36.06) * mm, "end": v(19.5, -36.17) * mm});
            skLineSegment(sketch, "E693", {"start": v(19.5, -36.17) * mm, "end": v(20, -36.29) * mm});
            skLineSegment(sketch, "E694", {"start": v(20, -36.29) * mm, "end": v(20.5, -36.4) * mm});
            skLineSegment(sketch, "E695", {"start": v(20.5, -36.4) * mm, "end": v(20.99, -36.55) * mm});
            skLineSegment(sketch, "E696", {"start": v(20.99, -36.55) * mm, "end": v(21.48, -36.7) * mm});
            skLineSegment(sketch, "E697", {"start": v(21.48, -36.7) * mm, "end": v(21.96, -36.87) * mm});
            skLineSegment(sketch, "E698", {"start": v(21.96, -36.87) * mm, "end": v(22.44, -37.03) * mm});
            skLineSegment(sketch, "E699", {"start": v(22.44, -37.03) * mm, "end": v(22.92, -37.22) * mm});
            skLineSegment(sketch, "E700", {"start": v(22.92, -37.22) * mm, "end": v(23.39, -37.42) * mm});
            skLineSegment(sketch, "E701", {"start": v(23.39, -37.42) * mm, "end": v(23.85, -37.63) * mm});
            skLineSegment(sketch, "E702", {"start": v(23.85, -37.63) * mm, "end": v(24.32, -37.84) * mm});
            skLineSegment(sketch, "E703", {"start": v(24.32, -37.84) * mm, "end": v(24.77, -38.07) * mm});
            skLineSegment(sketch, "E704", {"start": v(24.77, -38.07) * mm, "end": v(25.22, -38.32) * mm});
            skLineSegment(sketch, "E705", {"start": v(25.22, -38.32) * mm, "end": v(25.67, -38.57) * mm});
            skLineSegment(sketch, "E706", {"start": v(25.67, -38.57) * mm, "end": v(26.1, -38.82) * mm});
            skLineSegment(sketch, "E707", {"start": v(26.1, -38.82) * mm, "end": v(26.54, -39.1) * mm});
            skLineSegment(sketch, "E708", {"start": v(26.54, -39.1) * mm, "end": v(26.96, -39.39) * mm});
            skLineSegment(sketch, "E709", {"start": v(26.96, -39.39) * mm, "end": v(27.38, -39.68) * mm});
            skLineSegment(sketch, "E710", {"start": v(27.38, -39.68) * mm, "end": v(27.8, -39.98) * mm});
            skLineSegment(sketch, "E711", {"start": v(27.8, -39.98) * mm, "end": v(28.2, -40.3) * mm});
            skLineSegment(sketch, "E712", {"start": v(28.2, -40.3) * mm, "end": v(28.6, -40.62) * mm});
            skLineSegment(sketch, "E713", {"start": v(28.6, -40.62) * mm, "end": v(28.86, -40.83) * mm});
            skLineSegment(sketch, "E714", {"start": v(28.86, -40.83) * mm, "end": v(29.27, -40.53) * mm});
            skLineSegment(sketch, "E715", {"start": v(29.27, -40.53) * mm, "end": v(29.69, -40.23) * mm});
            skLineSegment(sketch, "E716", {"start": v(29.69, -40.23) * mm, "end": v(29.92, -40.06) * mm});
            skLineSegment(sketch, "E717", {"start": v(29.92, -40.06) * mm, "end": v(29.6, -39.65) * mm});
            skLineSegment(sketch, "E718", {"start": v(29.6, -39.65) * mm, "end": v(29.3, -39.24) * mm});
            skLineSegment(sketch, "E719", {"start": v(29.3, -39.24) * mm, "end": v(29, -38.83) * mm});
            skLineSegment(sketch, "E720", {"start": v(29, -38.83) * mm, "end": v(28.7, -38.42) * mm});
            skLineSegment(sketch, "E721", {"start": v(28.7, -38.42) * mm, "end": v(28.38, -38.01) * mm});
            skLineSegment(sketch, "E722", {"start": v(28.38, -38.01) * mm, "end": v(28.08, -37.6) * mm});
            skLineSegment(sketch, "E723", {"start": v(28.08, -37.6) * mm, "end": v(27.77, -37.2) * mm});
            skLineSegment(sketch, "E724", {"start": v(27.77, -37.2) * mm, "end": v(27.47, -36.78) * mm});
            skLineSegment(sketch, "E725", {"start": v(27.47, -36.78) * mm, "end": v(27.16, -36.37) * mm});
            skLineSegment(sketch, "E726", {"start": v(27.16, -36.37) * mm, "end": v(26.85, -35.96) * mm});
            skLineSegment(sketch, "E727", {"start": v(26.85, -35.96) * mm, "end": v(26.55, -35.55) * mm});
            skLineSegment(sketch, "E728", {"start": v(26.55, -35.55) * mm, "end": v(26.24, -35.14) * mm});
            skLineSegment(sketch, "E729", {"start": v(26.24, -35.14) * mm, "end": v(25.93, -34.73) * mm});
            skLineSegment(sketch, "E730", {"start": v(25.93, -34.73) * mm, "end": v(25.63, -34.32) * mm});
            skLineSegment(sketch, "E731", {"start": v(25.63, -34.32) * mm, "end": v(25.32, -33.9) * mm});
            skLineSegment(sketch, "E732", {"start": v(25.32, -33.9) * mm, "end": v(25.01, -33.5) * mm});
            skLineSegment(sketch, "E733", {"start": v(25.01, -33.5) * mm, "end": v(24.7, -33.09) * mm});
            skLineSegment(sketch, "E734", {"start": v(24.7, -33.09) * mm, "end": v(24.4, -32.68) * mm});
            skLineSegment(sketch, "E735", {"start": v(24.4, -32.68) * mm, "end": v(24.1, -32.27) * mm});
            skLineSegment(sketch, "E736", {"start": v(24.1, -32.27) * mm, "end": v(23.79, -31.86) * mm});
            skLineSegment(sketch, "E737", {"start": v(23.79, -31.86) * mm, "end": v(23.54, -31.52) * mm});
            skLineSegment(sketch, "E738", {"start": v(23.54, -31.52) * mm, "end": v(24.04, -31.46) * mm});
            skLineSegment(sketch, "E739", {"start": v(24.04, -31.46) * mm, "end": v(24.55, -31.4) * mm});
            skLineSegment(sketch, "E740", {"start": v(24.55, -31.4) * mm, "end": v(25.07, -31.37) * mm});
            skLineSegment(sketch, "E741", {"start": v(25.07, -31.37) * mm, "end": v(25.57, -31.34) * mm});
            skLineSegment(sketch, "E742", {"start": v(25.57, -31.34) * mm, "end": v(26.08, -31.32) * mm});
            skLineSegment(sketch, "E743", {"start": v(26.08, -31.32) * mm, "end": v(26.6, -31.32) * mm});
            skLineSegment(sketch, "E744", {"start": v(26.6, -31.32) * mm, "end": v(27.1, -31.33) * mm});
            skLineSegment(sketch, "E745", {"start": v(27.1, -31.33) * mm, "end": v(27.62, -31.35) * mm});
            skLineSegment(sketch, "E746", {"start": v(27.62, -31.35) * mm, "end": v(28.13, -31.38) * mm});
            skLineSegment(sketch, "E747", {"start": v(28.13, -31.38) * mm, "end": v(28.64, -31.43) * mm});
            skLineSegment(sketch, "E748", {"start": v(28.64, -31.43) * mm, "end": v(29.14, -31.5) * mm});
            skLineSegment(sketch, "E749", {"start": v(29.14, -31.5) * mm, "end": v(29.65, -31.56) * mm});
            skLineSegment(sketch, "E750", {"start": v(29.65, -31.56) * mm, "end": v(30.15, -31.64) * mm});
            skLineSegment(sketch, "E751", {"start": v(30.15, -31.64) * mm, "end": v(30.66, -31.74) * mm});
            skLineSegment(sketch, "E752", {"start": v(30.66, -31.74) * mm, "end": v(31.16, -31.85) * mm});
            skLineSegment(sketch, "E753", {"start": v(31.16, -31.85) * mm, "end": v(31.65, -31.96) * mm});
            skLineSegment(sketch, "E754", {"start": v(31.65, -31.96) * mm, "end": v(32.15, -32.09) * mm});
            skLineSegment(sketch, "E755", {"start": v(32.15, -32.09) * mm, "end": v(32.64, -32.23) * mm});
            skLineSegment(sketch, "E756", {"start": v(32.64, -32.23) * mm, "end": v(33.13, -32.4) * mm});
            skLineSegment(sketch, "E757", {"start": v(33.13, -32.4) * mm, "end": v(33.6, -32.55) * mm});
            skLineSegment(sketch, "E758", {"start": v(33.6, -32.55) * mm, "end": v(34.09, -32.73) * mm});
            skLineSegment(sketch, "E759", {"start": v(34.09, -32.73) * mm, "end": v(34.56, -32.92) * mm});
            skLineSegment(sketch, "E760", {"start": v(34.56, -32.92) * mm, "end": v(35.03, -33.12) * mm});
            skLineSegment(sketch, "E761", {"start": v(35.03, -33.12) * mm, "end": v(35.5, -33.32) * mm});
            skLineSegment(sketch, "E762", {"start": v(35.5, -33.32) * mm, "end": v(35.96, -33.55) * mm});
            skLineSegment(sketch, "E763", {"start": v(35.96, -33.55) * mm, "end": v(36.42, -33.78) * mm});
            skLineSegment(sketch, "E764", {"start": v(36.42, -33.78) * mm, "end": v(36.72, -33.94) * mm});
            skLineSegment(sketch, "E765", {"start": v(36.72, -33.94) * mm, "end": v(37.06, -33.56) * mm});
            skLineSegment(sketch, "E766", {"start": v(37.06, -33.56) * mm, "end": v(37.4, -33.18) * mm});
            skLineSegment(sketch, "E767", {"start": v(37.4, -33.18) * mm, "end": v(37.6, -32.97) * mm});
            skLineSegment(sketch, "E768", {"start": v(37.6, -32.97) * mm, "end": v(37.2, -32.63) * mm});
            skLineSegment(sketch, "E769", {"start": v(37.2, -32.63) * mm, "end": v(36.82, -32.3) * mm});
            skLineSegment(sketch, "E770", {"start": v(36.82, -32.3) * mm, "end": v(36.44, -31.95) * mm});
            skLineSegment(sketch, "E771", {"start": v(36.44, -31.95) * mm, "end": v(36.05, -31.62) * mm});
            skLineSegment(sketch, "E772", {"start": v(36.05, -31.62) * mm, "end": v(35.67, -31.28) * mm});
            skLineSegment(sketch, "E773", {"start": v(35.67, -31.28) * mm, "end": v(35.28, -30.94) * mm});
            skLineSegment(sketch, "E774", {"start": v(35.28, -30.94) * mm, "end": v(34.9, -30.6) * mm});
            skLineSegment(sketch, "E775", {"start": v(34.9, -30.6) * mm, "end": v(34.51, -30.27) * mm});
            skLineSegment(sketch, "E776", {"start": v(34.51, -30.27) * mm, "end": v(34.13, -29.93) * mm});
            skLineSegment(sketch, "E777", {"start": v(34.13, -29.93) * mm, "end": v(33.74, -29.6) * mm});
            skLineSegment(sketch, "E778", {"start": v(33.74, -29.6) * mm, "end": v(33.36, -29.25) * mm});
            skLineSegment(sketch, "E779", {"start": v(33.36, -29.25) * mm, "end": v(32.97, -28.92) * mm});
            skLineSegment(sketch, "E780", {"start": v(32.97, -28.92) * mm, "end": v(32.59, -28.58) * mm});
            skLineSegment(sketch, "E781", {"start": v(32.59, -28.58) * mm, "end": v(32.2, -28.24) * mm});
            skLineSegment(sketch, "E782", {"start": v(32.2, -28.24) * mm, "end": v(31.82, -27.9) * mm});
            skLineSegment(sketch, "E783", {"start": v(31.82, -27.9) * mm, "end": v(31.43, -27.57) * mm});
            skLineSegment(sketch, "E784", {"start": v(31.43, -27.57) * mm, "end": v(31.05, -27.23) * mm});
            skLineSegment(sketch, "E785", {"start": v(31.05, -27.23) * mm, "end": v(30.66, -26.9) * mm});
            skLineSegment(sketch, "E786", {"start": v(30.66, -26.9) * mm, "end": v(30.28, -26.55) * mm});
            skLineSegment(sketch, "E787", {"start": v(30.28, -26.55) * mm, "end": v(29.9, -26.22) * mm});
            skLineSegment(sketch, "E788", {"start": v(29.9, -26.22) * mm, "end": v(29.58, -25.94) * mm});
            skLineSegment(sketch, "E789", {"start": v(29.58, -25.94) * mm, "end": v(30.06, -25.77) * mm});
            skLineSegment(sketch, "E790", {"start": v(30.06, -25.77) * mm, "end": v(30.55, -25.62) * mm});
            skLineSegment(sketch, "E791", {"start": v(30.55, -25.62) * mm, "end": v(31.04, -25.47) * mm});
            skLineSegment(sketch, "E792", {"start": v(31.04, -25.47) * mm, "end": v(31.53, -25.33) * mm});
            skLineSegment(sketch, "E793", {"start": v(31.53, -25.33) * mm, "end": v(32.03, -25.21) * mm});
            skLineSegment(sketch, "E794", {"start": v(32.03, -25.21) * mm, "end": v(32.53, -25.1) * mm});
            skLineSegment(sketch, "E795", {"start": v(32.53, -25.1) * mm, "end": v(33.03, -25.01) * mm});
            skLineSegment(sketch, "E796", {"start": v(33.03, -25.01) * mm, "end": v(33.53, -24.92) * mm});
            skLineSegment(sketch, "E797", {"start": v(33.53, -24.92) * mm, "end": v(34.04, -24.85) * mm});
            skLineSegment(sketch, "E798", {"start": v(34.04, -24.85) * mm, "end": v(34.55, -24.8) * mm});
            skLineSegment(sketch, "E799", {"start": v(34.55, -24.8) * mm, "end": v(35.06, -24.75) * mm});
            skLineSegment(sketch, "E800", {"start": v(35.06, -24.75) * mm, "end": v(35.56, -24.7) * mm});
            skLineSegment(sketch, "E801", {"start": v(35.56, -24.7) * mm, "end": v(36.07, -24.68) * mm});
            skLineSegment(sketch, "E802", {"start": v(36.07, -24.68) * mm, "end": v(36.59, -24.67) * mm});
            skLineSegment(sketch, "E803", {"start": v(36.59, -24.67) * mm, "end": v(37.1, -24.67) * mm});
            skLineSegment(sketch, "E804", {"start": v(37.1, -24.67) * mm, "end": v(37.6, -24.68) * mm});
            skLineSegment(sketch, "E805", {"start": v(37.6, -24.68) * mm, "end": v(38.12, -24.7) * mm});
            skLineSegment(sketch, "E806", {"start": v(38.12, -24.7) * mm, "end": v(38.63, -24.74) * mm});
            skLineSegment(sketch, "E807", {"start": v(38.63, -24.74) * mm, "end": v(39.14, -24.8) * mm});
            skLineSegment(sketch, "E808", {"start": v(39.14, -24.8) * mm, "end": v(39.64, -24.85) * mm});
            skLineSegment(sketch, "E809", {"start": v(39.64, -24.85) * mm, "end": v(40.15, -24.92) * mm});
            skLineSegment(sketch, "E810", {"start": v(40.15, -24.92) * mm, "end": v(40.65, -25.01) * mm});
            skLineSegment(sketch, "E811", {"start": v(40.65, -25.01) * mm, "end": v(41.16, -25.11) * mm});
            skLineSegment(sketch, "E812", {"start": v(41.16, -25.11) * mm, "end": v(41.65, -25.21) * mm});
            skLineSegment(sketch, "E813", {"start": v(41.65, -25.21) * mm, "end": v(42.15, -25.34) * mm});
            skLineSegment(sketch, "E814", {"start": v(42.15, -25.34) * mm, "end": v(42.64, -25.47) * mm});
            skLineSegment(sketch, "E815", {"start": v(42.64, -25.47) * mm, "end": v(42.97, -25.56) * mm});
            skLineSegment(sketch, "E816", {"start": v(42.97, -25.56) * mm, "end": v(43.23, -25.12) * mm});
            skLineSegment(sketch, "E817", {"start": v(43.23, -25.12) * mm, "end": v(43.48, -24.68) * mm});
            skLineSegment(sketch, "E818", {"start": v(43.48, -24.68) * mm, "end": v(43.62, -24.43) * mm});
            skLineSegment(sketch, "E819", {"start": v(43.62, -24.43) * mm, "end": v(43.18, -24.18) * mm});
            skLineSegment(sketch, "E820", {"start": v(43.18, -24.18) * mm, "end": v(42.73, -23.93) * mm});
            skLineSegment(sketch, "E821", {"start": v(42.73, -23.93) * mm, "end": v(42.28, -23.68) * mm});
            skLineSegment(sketch, "E822", {"start": v(42.28, -23.68) * mm, "end": v(41.84, -23.43) * mm});
            skLineSegment(sketch, "E823", {"start": v(41.84, -23.43) * mm, "end": v(41.4, -23.18) * mm});
            skLineSegment(sketch, "E824", {"start": v(41.4, -23.18) * mm, "end": v(40.94, -22.93) * mm});
            skLineSegment(sketch, "E825", {"start": v(40.94, -22.93) * mm, "end": v(40.5, -22.68) * mm});
            skLineSegment(sketch, "E826", {"start": v(40.5, -22.68) * mm, "end": v(40.05, -22.43) * mm});
            skLineSegment(sketch, "E827", {"start": v(40.05, -22.43) * mm, "end": v(39.6, -22.18) * mm});
            skLineSegment(sketch, "E828", {"start": v(39.6, -22.18) * mm, "end": v(39.16, -21.93) * mm});
            skLineSegment(sketch, "E829", {"start": v(39.16, -21.93) * mm, "end": v(38.71, -21.68) * mm});
            skLineSegment(sketch, "E830", {"start": v(38.71, -21.68) * mm, "end": v(38.26, -21.43) * mm});
            skLineSegment(sketch, "E831", {"start": v(38.26, -21.43) * mm, "end": v(37.82, -21.18) * mm});
            skLineSegment(sketch, "E832", {"start": v(37.82, -21.18) * mm, "end": v(37.37, -20.93) * mm});
            skLineSegment(sketch, "E833", {"start": v(37.37, -20.93) * mm, "end": v(36.92, -20.68) * mm});
            skLineSegment(sketch, "E834", {"start": v(36.92, -20.68) * mm, "end": v(36.48, -20.43) * mm});
            skLineSegment(sketch, "E835", {"start": v(36.48, -20.43) * mm, "end": v(36.03, -20.18) * mm});
            skLineSegment(sketch, "E836", {"start": v(36.03, -20.18) * mm, "end": v(35.58, -19.93) * mm});
            skLineSegment(sketch, "E837", {"start": v(35.58, -19.93) * mm, "end": v(35.14, -19.68) * mm});
            skLineSegment(sketch, "E838", {"start": v(35.14, -19.68) * mm, "end": v(34.69, -19.43) * mm});
            skLineSegment(sketch, "E839", {"start": v(34.69, -19.43) * mm, "end": v(34.32, -19.22) * mm});
            skLineSegment(sketch, "E840", {"start": v(34.32, -19.22) * mm, "end": v(34.76, -18.96) * mm});
            skLineSegment(sketch, "E841", {"start": v(34.76, -18.96) * mm, "end": v(35.2, -18.7) * mm});
            skLineSegment(sketch, "E842", {"start": v(35.2, -18.7) * mm, "end": v(35.66, -18.46) * mm});
            skLineSegment(sketch, "E843", {"start": v(35.66, -18.46) * mm, "end": v(36.1, -18.23) * mm});
            skLineSegment(sketch, "E844", {"start": v(36.1, -18.23) * mm, "end": v(36.57, -18) * mm});
            skLineSegment(sketch, "E845", {"start": v(36.57, -18) * mm, "end": v(37.04, -17.8) * mm});
            skLineSegment(sketch, "E846", {"start": v(37.04, -17.8) * mm, "end": v(37.5, -17.6) * mm});
            skLineSegment(sketch, "E847", {"start": v(37.5, -17.6) * mm, "end": v(37.98, -17.4) * mm});
            skLineSegment(sketch, "E848", {"start": v(37.98, -17.4) * mm, "end": v(38.46, -17.23) * mm});
            skLineSegment(sketch, "E849", {"start": v(38.46, -17.23) * mm, "end": v(38.95, -17.07) * mm});
            skLineSegment(sketch, "E850", {"start": v(38.95, -17.07) * mm, "end": v(39.43, -16.92) * mm});
            skLineSegment(sketch, "E851", {"start": v(39.43, -16.92) * mm, "end": v(39.92, -16.77) * mm});
            skLineSegment(sketch, "E852", {"start": v(39.92, -16.77) * mm, "end": v(40.42, -16.64) * mm});
            skLineSegment(sketch, "E853", {"start": v(40.42, -16.64) * mm, "end": v(40.92, -16.52) * mm});
            skLineSegment(sketch, "E854", {"start": v(40.92, -16.52) * mm, "end": v(41.42, -16.42) * mm});
            skLineSegment(sketch, "E855", {"start": v(41.42, -16.42) * mm, "end": v(41.91, -16.32) * mm});
            skLineSegment(sketch, "E856", {"start": v(41.91, -16.32) * mm, "end": v(42.42, -16.24) * mm});
            skLineSegment(sketch, "E857", {"start": v(42.42, -16.24) * mm, "end": v(42.93, -16.17) * mm});
            skLineSegment(sketch, "E858", {"start": v(42.93, -16.17) * mm, "end": v(43.44, -16.12) * mm});
            skLineSegment(sketch, "E859", {"start": v(43.44, -16.12) * mm, "end": v(43.94, -16.06) * mm});
            skLineSegment(sketch, "E860", {"start": v(43.94, -16.06) * mm, "end": v(44.45, -16.03) * mm});
            skLineSegment(sketch, "E861", {"start": v(44.45, -16.03) * mm, "end": v(44.97, -16.01) * mm});
            skLineSegment(sketch, "E862", {"start": v(44.97, -16.01) * mm, "end": v(45.48, -16) * mm});
            skLineSegment(sketch, "E863", {"start": v(45.48, -16) * mm, "end": v(45.99, -16) * mm});
            skLineSegment(sketch, "E864", {"start": v(45.99, -16) * mm, "end": v(46.5, -16.02) * mm});
            skLineSegment(sketch, "E865", {"start": v(46.5, -16.02) * mm, "end": v(47, -16.05) * mm});
            skLineSegment(sketch, "E866", {"start": v(47, -16.05) * mm, "end": v(47.35, -16.07) * mm});
            skLineSegment(sketch, "E867", {"start": v(47.35, -16.07) * mm, "end": v(47.5, -15.58) * mm});
            skLineSegment(sketch, "E868", {"start": v(47.5, -15.58) * mm, "end": v(47.66, -15.1) * mm});
            skLineSegment(sketch, "E869", {"start": v(47.66, -15.1) * mm, "end": v(47.75, -14.83) * mm});
            skLineSegment(sketch, "E870", {"start": v(47.75, -14.83) * mm, "end": v(47.26, -14.68) * mm});
            skLineSegment(sketch, "E871", {"start": v(47.26, -14.68) * mm, "end": v(46.77, -14.52) * mm});
            skLineSegment(sketch, "E872", {"start": v(46.77, -14.52) * mm, "end": v(46.28, -14.37) * mm});
            skLineSegment(sketch, "E873", {"start": v(46.28, -14.37) * mm, "end": v(45.8, -14.22) * mm});
            skLineSegment(sketch, "E874", {"start": v(45.8, -14.22) * mm, "end": v(45.3, -14.07) * mm});
            skLineSegment(sketch, "E875", {"start": v(45.3, -14.07) * mm, "end": v(44.82, -13.92) * mm});
            skLineSegment(sketch, "E876", {"start": v(44.82, -13.92) * mm, "end": v(44.33, -13.76) * mm});
            skLineSegment(sketch, "E877", {"start": v(44.33, -13.76) * mm, "end": v(43.84, -13.61) * mm});
            skLineSegment(sketch, "E878", {"start": v(43.84, -13.61) * mm, "end": v(43.35, -13.46) * mm});
            skLineSegment(sketch, "E879", {"start": v(43.35, -13.46) * mm, "end": v(42.86, -13.3) * mm});
            skLineSegment(sketch, "E880", {"start": v(42.86, -13.3) * mm, "end": v(42.37, -13.16) * mm});
            skLineSegment(sketch, "E881", {"start": v(42.37, -13.16) * mm, "end": v(41.88, -13) * mm});
            skLineSegment(sketch, "E882", {"start": v(41.88, -13) * mm, "end": v(41.4, -12.85) * mm});
            skLineSegment(sketch, "E883", {"start": v(41.4, -12.85) * mm, "end": v(40.9, -12.7) * mm});
            skLineSegment(sketch, "E884", {"start": v(40.9, -12.7) * mm, "end": v(40.42, -12.55) * mm});
            skLineSegment(sketch, "E885", {"start": v(40.42, -12.55) * mm, "end": v(39.93, -12.4) * mm});
            skLineSegment(sketch, "E886", {"start": v(39.93, -12.4) * mm, "end": v(39.44, -12.25) * mm});
            skLineSegment(sketch, "E887", {"start": v(39.44, -12.25) * mm, "end": v(38.95, -12.1) * mm});
            skLineSegment(sketch, "E888", {"start": v(38.95, -12.1) * mm, "end": v(38.46, -11.94) * mm});
            skLineSegment(sketch, "E889", {"start": v(38.46, -11.94) * mm, "end": v(37.97, -11.8) * mm});
            skLineSegment(sketch, "E890", {"start": v(37.97, -11.8) * mm, "end": v(37.57, -11.67) * mm});
            skLineSegment(sketch, "E891", {"start": v(37.57, -11.67) * mm, "end": v(37.94, -11.32) * mm});
            skLineSegment(sketch, "E892", {"start": v(37.94, -11.32) * mm, "end": v(38.33, -10.98) * mm});
            skLineSegment(sketch, "E893", {"start": v(38.33, -10.98) * mm, "end": v(38.72, -10.65) * mm});
            skLineSegment(sketch, "E894", {"start": v(38.72, -10.65) * mm, "end": v(39.1, -10.32) * mm});
            skLineSegment(sketch, "E895", {"start": v(39.1, -10.32) * mm, "end": v(39.51, -10) * mm});
            skLineSegment(sketch, "E896", {"start": v(39.51, -10) * mm, "end": v(39.93, -9.7) * mm});
            skLineSegment(sketch, "E897", {"start": v(39.93, -9.7) * mm, "end": v(40.35, -9.42) * mm});
            skLineSegment(sketch, "E898", {"start": v(40.35, -9.42) * mm, "end": v(40.77, -9.13) * mm});
            skLineSegment(sketch, "E899", {"start": v(40.77, -9.13) * mm, "end": v(41.2, -8.86) * mm});
            skLineSegment(sketch, "E900", {"start": v(41.2, -8.86) * mm, "end": v(41.64, -8.6) * mm});
            skLineSegment(sketch, "E901", {"start": v(41.64, -8.6) * mm, "end": v(42.1, -8.35) * mm});
            skLineSegment(sketch, "E902", {"start": v(42.1, -8.35) * mm, "end": v(42.53, -8.1) * mm});
            skLineSegment(sketch, "E903", {"start": v(42.53, -8.1) * mm, "end": v(43, -7.87) * mm});
            skLineSegment(sketch, "E904", {"start": v(43, -7.87) * mm, "end": v(43.46, -7.66) * mm});
            skLineSegment(sketch, "E905", {"start": v(43.46, -7.66) * mm, "end": v(43.93, -7.45) * mm});
            skLineSegment(sketch, "E906", {"start": v(43.93, -7.45) * mm, "end": v(44.4, -7.25) * mm});
            skLineSegment(sketch, "E907", {"start": v(44.4, -7.25) * mm, "end": v(44.87, -7.06) * mm});
            skLineSegment(sketch, "E908", {"start": v(44.87, -7.06) * mm, "end": v(45.35, -6.9) * mm});
            skLineSegment(sketch, "E909", {"start": v(45.35, -6.9) * mm, "end": v(45.84, -6.73) * mm});
            skLineSegment(sketch, "E910", {"start": v(45.84, -6.73) * mm, "end": v(46.32, -6.58) * mm});
            skLineSegment(sketch, "E911", {"start": v(46.32, -6.58) * mm, "end": v(46.82, -6.44) * mm});
            skLineSegment(sketch, "E912", {"start": v(46.82, -6.44) * mm, "end": v(47.31, -6.32) * mm});
            skLineSegment(sketch, "E913", {"start": v(47.31, -6.32) * mm, "end": v(47.81, -6.2) * mm});
            skLineSegment(sketch, "E914", {"start": v(47.81, -6.2) * mm, "end": v(48.3, -6.1) * mm});
            skLineSegment(sketch, "E915", {"start": v(48.3, -6.1) * mm, "end": v(48.81, -6) * mm});
            skLineSegment(sketch, "E916", {"start": v(48.81, -6) * mm, "end": v(49.32, -5.93) * mm});
            skLineSegment(sketch, "E917", {"start": v(49.32, -5.93) * mm, "end": v(49.65, -5.88) * mm});
            skLineSegment(sketch, "E918", {"start": v(49.65, -5.88) * mm, "end": v(49.7, -5.37) * mm});
            skLineSegment(sketch, "E919", {"start": v(49.7, -5.37) * mm, "end": v(49.76, -4.86) * mm});
            skLineSegment(sketch, "E920", {"start": v(49.76, -4.86) * mm, "end": v(49.8, -4.58) * mm});
            skLineSegment(sketch, "E921", {"start": v(49.8, -4.58) * mm, "end": v(49.28, -4.53) * mm});
            skLineSegment(sketch, "E922", {"start": v(49.28, -4.53) * mm, "end": v(48.77, -4.48) * mm});
            skLineSegment(sketch, "E923", {"start": v(48.77, -4.48) * mm, "end": v(48.26, -4.43) * mm});
            skLineSegment(sketch, "E924", {"start": v(48.26, -4.43) * mm, "end": v(47.75, -4.39) * mm});
            skLineSegment(sketch, "E925", {"start": v(47.75, -4.39) * mm, "end": v(47.24, -4.34) * mm});
            skLineSegment(sketch, "E926", {"start": v(47.24, -4.34) * mm, "end": v(46.73, -4.3) * mm});
            skLineSegment(sketch, "E927", {"start": v(46.73, -4.3) * mm, "end": v(46.22, -4.25) * mm});
            skLineSegment(sketch, "E928", {"start": v(46.22, -4.25) * mm, "end": v(45.71, -4.2) * mm});
            skLineSegment(sketch, "E929", {"start": v(45.71, -4.2) * mm, "end": v(45.2, -4.15) * mm});
            skLineSegment(sketch, "E930", {"start": v(45.2, -4.15) * mm, "end": v(44.7, -4.1) * mm});
            skLineSegment(sketch, "E931", {"start": v(44.7, -4.1) * mm, "end": v(44.18, -4.06) * mm});
            skLineSegment(sketch, "E932", {"start": v(44.18, -4.06) * mm, "end": v(43.67, -4.01) * mm});
            skLineSegment(sketch, "E933", {"start": v(43.67, -4.01) * mm, "end": v(43.16, -3.97) * mm});
            skLineSegment(sketch, "E934", {"start": v(43.16, -3.97) * mm, "end": v(42.65, -3.92) * mm});
            skLineSegment(sketch, "E935", {"start": v(42.65, -3.92) * mm, "end": v(42.14, -3.87) * mm});
            skLineSegment(sketch, "E936", {"start": v(42.14, -3.87) * mm, "end": v(41.63, -3.83) * mm});
            skLineSegment(sketch, "E937", {"start": v(41.63, -3.83) * mm, "end": v(41.12, -3.78) * mm});
            skLineSegment(sketch, "E938", {"start": v(41.12, -3.78) * mm, "end": v(40.61, -3.73) * mm});
            skLineSegment(sketch, "E939", {"start": v(40.61, -3.73) * mm, "end": v(40.1, -3.68) * mm});
            skLineSegment(sketch, "E940", {"start": v(40.1, -3.68) * mm, "end": v(39.6, -3.64) * mm});
            skLineSegment(sketch, "E941", {"start": v(39.6, -3.64) * mm, "end": v(39.17, -3.6) * mm});
            skLineSegment(sketch, "E942", {"start": v(39.17, -3.6) * mm, "end": v(39.47, -3.18) * mm});
            skLineSegment(sketch, "E943", {"start": v(39.47, -3.18) * mm, "end": v(39.77, -2.77) * mm});
            skLineSegment(sketch, "E944", {"start": v(39.77, -2.77) * mm, "end": v(40.09, -2.36) * mm});
            skLineSegment(sketch, "E945", {"start": v(40.09, -2.36) * mm, "end": v(40.4, -1.96) * mm});
            skLineSegment(sketch, "E946", {"start": v(40.4, -1.96) * mm, "end": v(40.73, -1.57) * mm});
            skLineSegment(sketch, "E947", {"start": v(40.73, -1.57) * mm, "end": v(41.07, -1.2) * mm});
            skLineSegment(sketch, "E948", {"start": v(41.07, -1.2) * mm, "end": v(41.42, -0.82) * mm});
            skLineSegment(sketch, "E949", {"start": v(41.42, -0.82) * mm, "end": v(41.77, -0.45) * mm});
            skLineSegment(sketch, "E950", {"start": v(41.77, -0.45) * mm, "end": v(42.14, -0.1) * mm});
            skLineSegment(sketch, "E951", {"start": v(42.14, -0.1) * mm, "end": v(42.52, 0.25) * mm});
            skLineSegment(sketch, "E952", {"start": v(42.52, 0.25) * mm, "end": v(42.9, 0.59) * mm});
            skLineSegment(sketch, "E953", {"start": v(42.9, 0.59) * mm, "end": v(43.29, 0.92) * mm});
            skLineSegment(sketch, "E954", {"start": v(43.29, 0.92) * mm, "end": v(43.69, 1.24) * mm});
            skLineSegment(sketch, "E955", {"start": v(43.69, 1.24) * mm, "end": v(44.1, 1.55) * mm});
            skLineSegment(sketch, "E956", {"start": v(44.1, 1.55) * mm, "end": v(44.52, 1.84) * mm});
            skLineSegment(sketch, "E957", {"start": v(44.52, 1.84) * mm, "end": v(44.93, 2.14) * mm});
            skLineSegment(sketch, "E958", {"start": v(44.93, 2.14) * mm, "end": v(45.36, 2.42) * mm});
            skLineSegment(sketch, "E959", {"start": v(45.36, 2.42) * mm, "end": v(45.8, 2.69) * mm});
            skLineSegment(sketch, "E960", {"start": v(45.8, 2.69) * mm, "end": v(46.24, 2.94) * mm});
            skLineSegment(sketch, "E961", {"start": v(46.24, 2.94) * mm, "end": v(46.68, 3.2) * mm});
            skLineSegment(sketch, "E962", {"start": v(46.68, 3.2) * mm, "end": v(47.13, 3.43) * mm});
            skLineSegment(sketch, "E963", {"start": v(47.13, 3.43) * mm, "end": v(47.6, 3.66) * mm});
            skLineSegment(sketch, "E964", {"start": v(47.6, 3.66) * mm, "end": v(48.06, 3.87) * mm});
            skLineSegment(sketch, "E965", {"start": v(48.06, 3.87) * mm, "end": v(48.52, 4.08) * mm});
            skLineSegment(sketch, "E966", {"start": v(48.52, 4.08) * mm, "end": v(49, 4.28) * mm});
            skLineSegment(sketch, "E967", {"start": v(49, 4.28) * mm, "end": v(49.47, 4.46) * mm});
            skLineSegment(sketch, "E968", {"start": v(49.47, 4.46) * mm, "end": v(49.8, 4.58) * mm});
            skLineSegment(sketch, "E969", {"start": v(49.8, 4.58) * mm, "end": v(49.74, 5.08) * mm});
            skLineSegment(sketch, "E970", {"start": v(49.74, 5.08) * mm, "end": v(49.68, 5.6) * mm});
            skLineSegment(sketch, "E971", {"start": v(49.68, 5.6) * mm, "end": v(49.65, 5.88) * mm});
            skLineSegment(sketch, "E972", {"start": v(49.65, 5.88) * mm, "end": v(49.14, 5.82) * mm});
            skLineSegment(sketch, "E973", {"start": v(49.14, 5.82) * mm, "end": v(48.64, 5.76) * mm});
            skLineSegment(sketch, "E974", {"start": v(48.64, 5.76) * mm, "end": v(48.13, 5.7) * mm});
            skLineSegment(sketch, "E975", {"start": v(48.13, 5.7) * mm, "end": v(47.62, 5.64) * mm});
            skLineSegment(sketch, "E976", {"start": v(47.62, 5.64) * mm, "end": v(47.11, 5.58) * mm});
            skLineSegment(sketch, "E977", {"start": v(47.11, 5.58) * mm, "end": v(46.6, 5.52) * mm});
            skLineSegment(sketch, "E978", {"start": v(46.6, 5.52) * mm, "end": v(46.1, 5.46) * mm});
            skLineSegment(sketch, "E979", {"start": v(46.1, 5.46) * mm, "end": v(45.59, 5.4) * mm});
            skLineSegment(sketch, "E980", {"start": v(45.59, 5.4) * mm, "end": v(45.08, 5.34) * mm});
            skLineSegment(sketch, "E981", {"start": v(45.08, 5.34) * mm, "end": v(44.57, 5.28) * mm});
            skLineSegment(sketch, "E982", {"start": v(44.57, 5.28) * mm, "end": v(44.06, 5.21) * mm});
            skLineSegment(sketch, "E983", {"start": v(44.06, 5.21) * mm, "end": v(43.55, 5.15) * mm});
            skLineSegment(sketch, "E984", {"start": v(43.55, 5.15) * mm, "end": v(43.04, 5.1) * mm});
            skLineSegment(sketch, "E985", {"start": v(43.04, 5.1) * mm, "end": v(42.53, 5.03) * mm});
            skLineSegment(sketch, "E986", {"start": v(42.53, 5.03) * mm, "end": v(42.03, 4.97) * mm});
            skLineSegment(sketch, "E987", {"start": v(42.03, 4.97) * mm, "end": v(41.52, 4.91) * mm});
            skLineSegment(sketch, "E988", {"start": v(41.52, 4.91) * mm, "end": v(41, 4.85) * mm});
            skLineSegment(sketch, "E989", {"start": v(41, 4.85) * mm, "end": v(40.5, 4.8) * mm});
            skLineSegment(sketch, "E990", {"start": v(40.5, 4.8) * mm, "end": v(40, 4.73) * mm});
            skLineSegment(sketch, "E991", {"start": v(40, 4.73) * mm, "end": v(39.48, 4.67) * mm});
            skLineSegment(sketch, "E992", {"start": v(39.48, 4.67) * mm, "end": v(39.06, 4.62) * mm});
            skLineSegment(sketch, "E993", {"start": v(39.06, 4.62) * mm, "end": v(39.26, 5.1) * mm});
            skLineSegment(sketch, "E994", {"start": v(39.26, 5.1) * mm, "end": v(39.48, 5.56) * mm});
            skLineSegment(sketch, "E995", {"start": v(39.48, 5.56) * mm, "end": v(39.7, 6.02) * mm});
            skLineSegment(sketch, "E996", {"start": v(39.7, 6.02) * mm, "end": v(39.92, 6.48) * mm});
            skLineSegment(sketch, "E997", {"start": v(39.92, 6.48) * mm, "end": v(40.17, 6.93) * mm});
            skLineSegment(sketch, "E998", {"start": v(40.17, 6.93) * mm, "end": v(40.42, 7.37) * mm});
            skLineSegment(sketch, "E999", {"start": v(40.42, 7.37) * mm, "end": v(40.7, 7.8) * mm});
            skLineSegment(sketch, "E1000", {"start": v(40.7, 7.8) * mm, "end": v(40.96, 8.24) * mm});
            skLineSegment(sketch, "E1001", {"start": v(40.96, 8.24) * mm, "end": v(41.24, 8.67) * mm});
            skLineSegment(sketch, "E1002", {"start": v(41.24, 8.67) * mm, "end": v(41.54, 9.08) * mm});
            skLineSegment(sketch, "E1003", {"start": v(41.54, 9.08) * mm, "end": v(41.85, 9.5) * mm});
            skLineSegment(sketch, "E1004", {"start": v(41.85, 9.5) * mm, "end": v(42.15, 9.9) * mm});
            skLineSegment(sketch, "E1005", {"start": v(42.15, 9.9) * mm, "end": v(42.48, 10.3) * mm});
            skLineSegment(sketch, "E1006", {"start": v(42.48, 10.3) * mm, "end": v(42.81, 10.68) * mm});
            skLineSegment(sketch, "E1007", {"start": v(42.81, 10.68) * mm, "end": v(43.16, 11.06) * mm});
            skLineSegment(sketch, "E1008", {"start": v(43.16, 11.06) * mm, "end": v(43.5, 11.43) * mm});
            skLineSegment(sketch, "E1009", {"start": v(43.5, 11.43) * mm, "end": v(43.86, 11.8) * mm});
            skLineSegment(sketch, "E1010", {"start": v(43.86, 11.8) * mm, "end": v(44.23, 12.15) * mm});
            skLineSegment(sketch, "E1011", {"start": v(44.23, 12.15) * mm, "end": v(44.61, 12.5) * mm});
            skLineSegment(sketch, "E1012", {"start": v(44.61, 12.5) * mm, "end": v(45, 12.83) * mm});
            skLineSegment(sketch, "E1013", {"start": v(45, 12.83) * mm, "end": v(45.39, 13.16) * mm});
            skLineSegment(sketch, "E1014", {"start": v(45.39, 13.16) * mm, "end": v(45.8, 13.47) * mm});
            skLineSegment(sketch, "E1015", {"start": v(45.8, 13.47) * mm, "end": v(46.2, 13.78) * mm});
            skLineSegment(sketch, "E1016", {"start": v(46.2, 13.78) * mm, "end": v(46.6, 14.08) * mm});
            skLineSegment(sketch, "E1017", {"start": v(46.6, 14.08) * mm, "end": v(47.03, 14.37) * mm});
            skLineSegment(sketch, "E1018", {"start": v(47.03, 14.37) * mm, "end": v(47.47, 14.64) * mm});
            skLineSegment(sketch, "E1019", {"start": v(47.47, 14.64) * mm, "end": v(47.75, 14.83) * mm});
            skLineSegment(sketch, "E1020", {"start": v(47.75, 14.83) * mm, "end": v(47.6, 15.31) * mm});
            skLineSegment(sketch, "E1021", {"start": v(47.6, 15.31) * mm, "end": v(47.43, 15.8) * mm});
            skLineSegment(sketch, "E1022", {"start": v(47.43, 15.8) * mm, "end": v(47.35, 16.07) * mm});
            skLineSegment(sketch, "E1023", {"start": v(47.35, 16.07) * mm, "end": v(46.86, 15.9) * mm});
            skLineSegment(sketch, "E1024", {"start": v(46.86, 15.9) * mm, "end": v(46.38, 15.74) * mm});
            skLineSegment(sketch, "E1025", {"start": v(46.38, 15.74) * mm, "end": v(45.9, 15.58) * mm});
            skLineSegment(sketch, "E1026", {"start": v(45.9, 15.58) * mm, "end": v(45.4, 15.41) * mm});
            skLineSegment(sketch, "E1027", {"start": v(45.4, 15.41) * mm, "end": v(44.92, 15.25) * mm});
            skLineSegment(sketch, "E1028", {"start": v(44.92, 15.25) * mm, "end": v(44.44, 15.08) * mm});
            skLineSegment(sketch, "E1029", {"start": v(44.44, 15.08) * mm, "end": v(43.95, 14.92) * mm});
            skLineSegment(sketch, "E1030", {"start": v(43.95, 14.92) * mm, "end": v(43.47, 14.76) * mm});
            skLineSegment(sketch, "E1031", {"start": v(43.47, 14.76) * mm, "end": v(42.98, 14.6) * mm});
            skLineSegment(sketch, "E1032", {"start": v(42.98, 14.6) * mm, "end": v(42.5, 14.43) * mm});
            skLineSegment(sketch, "E1033", {"start": v(42.5, 14.43) * mm, "end": v(42.01, 14.26) * mm});
            skLineSegment(sketch, "E1034", {"start": v(42.01, 14.26) * mm, "end": v(41.53, 14.1) * mm});
            skLineSegment(sketch, "E1035", {"start": v(41.53, 14.1) * mm, "end": v(41.04, 13.93) * mm});
            skLineSegment(sketch, "E1036", {"start": v(41.04, 13.93) * mm, "end": v(40.56, 13.77) * mm});
            skLineSegment(sketch, "E1037", {"start": v(40.56, 13.77) * mm, "end": v(40.07, 13.6) * mm});
            skLineSegment(sketch, "E1038", {"start": v(40.07, 13.6) * mm, "end": v(39.59, 13.44) * mm});
            skLineSegment(sketch, "E1039", {"start": v(39.59, 13.44) * mm, "end": v(39.1, 13.27) * mm});
            skLineSegment(sketch, "E1040", {"start": v(39.1, 13.27) * mm, "end": v(38.62, 13.1) * mm});
            skLineSegment(sketch, "E1041", {"start": v(38.62, 13.1) * mm, "end": v(38.13, 12.94) * mm});
            skLineSegment(sketch, "E1042", {"start": v(38.13, 12.94) * mm, "end": v(37.65, 12.78) * mm});
            skLineSegment(sketch, "E1043", {"start": v(37.65, 12.78) * mm, "end": v(37.25, 12.64) * mm});
            skLineSegment(sketch, "E1044", {"start": v(37.25, 12.64) * mm, "end": v(37.35, 13.15) * mm});
            skLineSegment(sketch, "E1045", {"start": v(37.35, 13.15) * mm, "end": v(37.46, 13.65) * mm});
            skLineSegment(sketch, "E1046", {"start": v(37.46, 13.65) * mm, "end": v(37.58, 14.14) * mm});
            skLineSegment(sketch, "E1047", {"start": v(37.58, 14.14) * mm, "end": v(37.7, 14.64) * mm});
            skLineSegment(sketch, "E1048", {"start": v(37.7, 14.64) * mm, "end": v(37.85, 15.13) * mm});
            skLineSegment(sketch, "E1049", {"start": v(37.85, 15.13) * mm, "end": v(38, 15.62) * mm});
            skLineSegment(sketch, "E1050", {"start": v(38, 15.62) * mm, "end": v(38.18, 16.1) * mm});
            skLineSegment(sketch, "E1051", {"start": v(38.18, 16.1) * mm, "end": v(38.35, 16.58) * mm});
            skLineSegment(sketch, "E1052", {"start": v(38.35, 16.58) * mm, "end": v(38.54, 17.05) * mm});
            skLineSegment(sketch, "E1053", {"start": v(38.54, 17.05) * mm, "end": v(38.74, 17.52) * mm});
            skLineSegment(sketch, "E1054", {"start": v(38.74, 17.52) * mm, "end": v(38.96, 17.99) * mm});
            skLineSegment(sketch, "E1055", {"start": v(38.96, 17.99) * mm, "end": v(39.17, 18.45) * mm});
            skLineSegment(sketch, "E1056", {"start": v(39.17, 18.45) * mm, "end": v(39.4, 18.9) * mm});
            skLineSegment(sketch, "E1057", {"start": v(39.4, 18.9) * mm, "end": v(39.66, 19.35) * mm});
            skLineSegment(sketch, "E1058", {"start": v(39.66, 19.35) * mm, "end": v(39.92, 19.8) * mm});
            skLineSegment(sketch, "E1059", {"start": v(39.92, 19.8) * mm, "end": v(40.17, 20.23) * mm});
            skLineSegment(sketch, "E1060", {"start": v(40.17, 20.23) * mm, "end": v(40.45, 20.66) * mm});
            skLineSegment(sketch, "E1061", {"start": v(40.45, 20.66) * mm, "end": v(40.74, 21.08) * mm});
            skLineSegment(sketch, "E1062", {"start": v(40.74, 21.08) * mm, "end": v(41.04, 21.5) * mm});
            skLineSegment(sketch, "E1063", {"start": v(41.04, 21.5) * mm, "end": v(41.34, 21.9) * mm});
            skLineSegment(sketch, "E1064", {"start": v(41.34, 21.9) * mm, "end": v(41.66, 22.3) * mm});
            skLineSegment(sketch, "E1065", {"start": v(41.66, 22.3) * mm, "end": v(41.99, 22.7) * mm});
            skLineSegment(sketch, "E1066", {"start": v(41.99, 22.7) * mm, "end": v(42.33, 23.08) * mm});
            skLineSegment(sketch, "E1067", {"start": v(42.33, 23.08) * mm, "end": v(42.66, 23.47) * mm});
            skLineSegment(sketch, "E1068", {"start": v(42.66, 23.47) * mm, "end": v(43.02, 23.83) * mm});
            skLineSegment(sketch, "E1069", {"start": v(43.02, 23.83) * mm, "end": v(43.38, 24.2) * mm});
            skLineSegment(sketch, "E1070", {"start": v(43.38, 24.2) * mm, "end": v(43.62, 24.43) * mm});
            skLineSegment(sketch, "E1071", {"start": v(43.62, 24.43) * mm, "end": v(43.37, 24.87) * mm});
            skLineSegment(sketch, "E1072", {"start": v(43.37, 24.87) * mm, "end": v(43.11, 25.32) * mm});
            skLineSegment(sketch, "E1073", {"start": v(43.11, 25.32) * mm, "end": v(42.97, 25.56) * mm});
            skLineSegment(sketch, "E1074", {"start": v(42.97, 25.56) * mm, "end": v(42.53, 25.3) * mm});
            skLineSegment(sketch, "E1075", {"start": v(42.53, 25.3) * mm, "end": v(42.1, 25.04) * mm});
            skLineSegment(sketch, "E1076", {"start": v(42.1, 25.04) * mm, "end": v(41.65, 24.78) * mm});
            skLineSegment(sketch, "E1077", {"start": v(41.65, 24.78) * mm, "end": v(41.21, 24.52) * mm});
            skLineSegment(sketch, "E1078", {"start": v(41.21, 24.52) * mm, "end": v(40.77, 24.26) * mm});
            skLineSegment(sketch, "E1079", {"start": v(40.77, 24.26) * mm, "end": v(40.33, 24) * mm});
            skLineSegment(sketch, "E1080", {"start": v(40.33, 24) * mm, "end": v(39.89, 23.73) * mm});
            skLineSegment(sketch, "E1081", {"start": v(39.89, 23.73) * mm, "end": v(39.45, 23.47) * mm});
            skLineSegment(sketch, "E1082", {"start": v(39.45, 23.47) * mm, "end": v(39, 23.2) * mm});
            skLineSegment(sketch, "E1083", {"start": v(39, 23.2) * mm, "end": v(38.57, 22.95) * mm});
            skLineSegment(sketch, "E1084", {"start": v(38.57, 22.95) * mm, "end": v(38.13, 22.68) * mm});
            skLineSegment(sketch, "E1085", {"start": v(38.13, 22.68) * mm, "end": v(37.69, 22.42) * mm});
            skLineSegment(sketch, "E1086", {"start": v(37.69, 22.42) * mm, "end": v(37.25, 22.16) * mm});
            skLineSegment(sketch, "E1087", {"start": v(37.25, 22.16) * mm, "end": v(36.8, 21.9) * mm});
            skLineSegment(sketch, "E1088", {"start": v(36.8, 21.9) * mm, "end": v(36.37, 21.64) * mm});
            skLineSegment(sketch, "E1089", {"start": v(36.37, 21.64) * mm, "end": v(35.93, 21.38) * mm});
            skLineSegment(sketch, "E1090", {"start": v(35.93, 21.38) * mm, "end": v(35.49, 21.11) * mm});
            skLineSegment(sketch, "E1091", {"start": v(35.49, 21.11) * mm, "end": v(35.05, 20.85) * mm});
            skLineSegment(sketch, "E1092", {"start": v(35.05, 20.85) * mm, "end": v(34.6, 20.6) * mm});
            skLineSegment(sketch, "E1093", {"start": v(34.6, 20.6) * mm, "end": v(34.17, 20.33) * mm});
            skLineSegment(sketch, "E1094", {"start": v(34.17, 20.33) * mm, "end": v(33.8, 20.11) * mm});
            skLineSegment(sketch, "E1095", {"start": v(33.8, 20.11) * mm, "end": v(33.8, 20.62) * mm});
            skLineSegment(sketch, "E1096", {"start": v(33.8, 20.62) * mm, "end": v(33.8, 21.14) * mm});
            skLineSegment(sketch, "E1097", {"start": v(33.8, 21.14) * mm, "end": v(33.82, 21.65) * mm});
            skLineSegment(sketch, "E1098", {"start": v(33.82, 21.65) * mm, "end": v(33.84, 22.16) * mm});
            skLineSegment(sketch, "E1099", {"start": v(33.84, 22.16) * mm, "end": v(33.88, 22.67) * mm});
            skLineSegment(sketch, "E1100", {"start": v(33.88, 22.67) * mm, "end": v(33.93, 23.18) * mm});
            skLineSegment(sketch, "E1101", {"start": v(33.93, 23.18) * mm, "end": v(34, 23.68) * mm});
            skLineSegment(sketch, "E1102", {"start": v(34, 23.68) * mm, "end": v(34.06, 24.19) * mm});
            skLineSegment(sketch, "E1103", {"start": v(34.06, 24.19) * mm, "end": v(34.15, 24.7) * mm});
            skLineSegment(sketch, "E1104", {"start": v(34.15, 24.7) * mm, "end": v(34.25, 25.2) * mm});
            skLineSegment(sketch, "E1105", {"start": v(34.25, 25.2) * mm, "end": v(34.37, 25.7) * mm});
            skLineSegment(sketch, "E1106", {"start": v(34.37, 25.7) * mm, "end": v(34.48, 26.19) * mm});
            skLineSegment(sketch, "E1107", {"start": v(34.48, 26.19) * mm, "end": v(34.62, 26.68) * mm});
            skLineSegment(sketch, "E1108", {"start": v(34.62, 26.68) * mm, "end": v(34.77, 27.17) * mm});
            skLineSegment(sketch, "E1109", {"start": v(34.77, 27.17) * mm, "end": v(34.93, 27.66) * mm});
            skLineSegment(sketch, "E1110", {"start": v(34.93, 27.66) * mm, "end": v(35.1, 28.14) * mm});
            skLineSegment(sketch, "E1111", {"start": v(35.1, 28.14) * mm, "end": v(35.27, 28.62) * mm});
            skLineSegment(sketch, "E1112", {"start": v(35.27, 28.62) * mm, "end": v(35.47, 29.1) * mm});
            skLineSegment(sketch, "E1113", {"start": v(35.47, 29.1) * mm, "end": v(35.68, 29.56) * mm});
            skLineSegment(sketch, "E1114", {"start": v(35.68, 29.56) * mm, "end": v(35.88, 30.02) * mm});
            skLineSegment(sketch, "E1115", {"start": v(35.88, 30.02) * mm, "end": v(36.11, 30.48) * mm});
            skLineSegment(sketch, "E1116", {"start": v(36.11, 30.48) * mm, "end": v(36.35, 30.93) * mm});
            skLineSegment(sketch, "E1117", {"start": v(36.35, 30.93) * mm, "end": v(36.6, 31.38) * mm});
            skLineSegment(sketch, "E1118", {"start": v(36.6, 31.38) * mm, "end": v(36.85, 31.82) * mm});
            skLineSegment(sketch, "E1119", {"start": v(36.85, 31.82) * mm, "end": v(37.12, 32.26) * mm});
            skLineSegment(sketch, "E1120", {"start": v(37.12, 32.26) * mm, "end": v(37.4, 32.68) * mm});
            skLineSegment(sketch, "E1121", {"start": v(37.4, 32.68) * mm, "end": v(37.6, 32.97) * mm});
            skLineSegment(sketch, "E1122", {"start": v(37.6, 32.97) * mm, "end": v(37.25, 33.35) * mm});
            skLineSegment(sketch, "E1123", {"start": v(37.25, 33.35) * mm, "end": v(36.9, 33.73) * mm});
            skLineSegment(sketch, "E1124", {"start": v(36.9, 33.73) * mm, "end": v(36.72, 33.94) * mm});
            skLineSegment(sketch, "E1125", {"start": v(36.72, 33.94) * mm, "end": v(36.34, 33.6) * mm});
            skLineSegment(sketch, "E1126", {"start": v(36.34, 33.6) * mm, "end": v(35.96, 33.24) * mm});
            skLineSegment(sketch, "E1127", {"start": v(35.96, 33.24) * mm, "end": v(35.59, 32.9) * mm});
            skLineSegment(sketch, "E1128", {"start": v(35.59, 32.9) * mm, "end": v(35.21, 32.55) * mm});
            skLineSegment(sketch, "E1129", {"start": v(35.21, 32.55) * mm, "end": v(34.84, 32.2) * mm});
            skLineSegment(sketch, "E1130", {"start": v(34.84, 32.2) * mm, "end": v(34.46, 31.85) * mm});
            skLineSegment(sketch, "E1131", {"start": v(34.46, 31.85) * mm, "end": v(34.08, 31.5) * mm});
            skLineSegment(sketch, "E1132", {"start": v(34.08, 31.5) * mm, "end": v(33.7, 31.16) * mm});
            skLineSegment(sketch, "E1133", {"start": v(33.7, 31.16) * mm, "end": v(33.33, 30.81) * mm});
            skLineSegment(sketch, "E1134", {"start": v(33.33, 30.81) * mm, "end": v(32.96, 30.46) * mm});
            skLineSegment(sketch, "E1135", {"start": v(32.96, 30.46) * mm, "end": v(32.58, 30.12) * mm});
            skLineSegment(sketch, "E1136", {"start": v(32.58, 30.12) * mm, "end": v(32.2, 29.77) * mm});
            skLineSegment(sketch, "E1137", {"start": v(32.2, 29.77) * mm, "end": v(31.83, 29.42) * mm});
            skLineSegment(sketch, "E1138", {"start": v(31.83, 29.42) * mm, "end": v(31.45, 29.07) * mm});
            skLineSegment(sketch, "E1139", {"start": v(31.45, 29.07) * mm, "end": v(31.08, 28.73) * mm});
            skLineSegment(sketch, "E1140", {"start": v(31.08, 28.73) * mm, "end": v(30.7, 28.38) * mm});
            skLineSegment(sketch, "E1141", {"start": v(30.7, 28.38) * mm, "end": v(30.32, 28.03) * mm});
            skLineSegment(sketch, "E1142", {"start": v(30.32, 28.03) * mm, "end": v(29.95, 27.68) * mm});
            skLineSegment(sketch, "E1143", {"start": v(29.95, 27.68) * mm, "end": v(29.57, 27.34) * mm});
            skLineSegment(sketch, "E1144", {"start": v(29.57, 27.34) * mm, "end": v(29.2, 26.99) * mm});
            skLineSegment(sketch, "E1145", {"start": v(29.2, 26.99) * mm, "end": v(28.89, 26.7) * mm});
            skLineSegment(sketch, "E1146", {"start": v(28.89, 26.7) * mm, "end": v(28.77, 27.2) * mm});
            skLineSegment(sketch, "E1147", {"start": v(28.77, 27.2) * mm, "end": v(28.67, 27.7) * mm});
            skLineSegment(sketch, "E1148", {"start": v(28.67, 27.7) * mm, "end": v(28.58, 28.2) * mm});
            skLineSegment(sketch, "E1149", {"start": v(28.58, 28.2) * mm, "end": v(28.5, 28.7) * mm});
            skLineSegment(sketch, "E1150", {"start": v(28.5, 28.7) * mm, "end": v(28.42, 29.22) * mm});
            skLineSegment(sketch, "E1151", {"start": v(28.42, 29.22) * mm, "end": v(28.37, 29.72) * mm});
            skLineSegment(sketch, "E1152", {"start": v(28.37, 29.72) * mm, "end": v(28.33, 30.23) * mm});
            skLineSegment(sketch, "E1153", {"start": v(28.33, 30.23) * mm, "end": v(28.29, 30.74) * mm});
            skLineSegment(sketch, "E1154", {"start": v(28.29, 30.74) * mm, "end": v(28.27, 31.25) * mm});
            skLineSegment(sketch, "E1155", {"start": v(28.27, 31.25) * mm, "end": v(28.27, 31.77) * mm});
            skLineSegment(sketch, "E1156", {"start": v(28.27, 31.77) * mm, "end": v(28.27, 32.28) * mm});
            skLineSegment(sketch, "E1157", {"start": v(28.27, 32.28) * mm, "end": v(28.28, 32.79) * mm});
            skLineSegment(sketch, "E1158", {"start": v(28.28, 32.79) * mm, "end": v(28.31, 33.3) * mm});
            skLineSegment(sketch, "E1159", {"start": v(28.31, 33.3) * mm, "end": v(28.36, 33.8) * mm});
            skLineSegment(sketch, "E1160", {"start": v(28.36, 33.8) * mm, "end": v(28.42, 34.32) * mm});
            skLineSegment(sketch, "E1161", {"start": v(28.42, 34.32) * mm, "end": v(28.47, 34.82) * mm});
            skLineSegment(sketch, "E1162", {"start": v(28.47, 34.82) * mm, "end": v(28.55, 35.33) * mm});
            skLineSegment(sketch, "E1163", {"start": v(28.55, 35.33) * mm, "end": v(28.65, 35.83) * mm});
            skLineSegment(sketch, "E1164", {"start": v(28.65, 35.83) * mm, "end": v(28.75, 36.33) * mm});
            skLineSegment(sketch, "E1165", {"start": v(28.75, 36.33) * mm, "end": v(28.86, 36.83) * mm});
            skLineSegment(sketch, "E1166", {"start": v(28.86, 36.83) * mm, "end": v(28.98, 37.32) * mm});
            skLineSegment(sketch, "E1167", {"start": v(28.98, 37.32) * mm, "end": v(29.12, 37.82) * mm});
            skLineSegment(sketch, "E1168", {"start": v(29.12, 37.82) * mm, "end": v(29.28, 38.3) * mm});
            skLineSegment(sketch, "E1169", {"start": v(29.28, 38.3) * mm, "end": v(29.43, 38.79) * mm});
            skLineSegment(sketch, "E1170", {"start": v(29.43, 38.79) * mm, "end": v(29.6, 39.27) * mm});
            skLineSegment(sketch, "E1171", {"start": v(29.6, 39.27) * mm, "end": v(29.8, 39.75) * mm});
            skLineSegment(sketch, "E1172", {"start": v(29.8, 39.75) * mm, "end": v(29.92, 40.06) * mm});
            skLineSegment(sketch, "E1173", {"start": v(29.92, 40.06) * mm, "end": v(29.5, 40.36) * mm});
            skLineSegment(sketch, "E1174", {"start": v(29.5, 40.36) * mm, "end": v(29.09, 40.66) * mm});
            skLineSegment(sketch, "E1175", {"start": v(29.09, 40.66) * mm, "end": v(28.86, 40.83) * mm});
            skLineSegment(sketch, "E1176", {"start": v(28.86, 40.83) * mm, "end": v(28.56, 40.41) * mm});
            skLineSegment(sketch, "E1177", {"start": v(28.56, 40.41) * mm, "end": v(28.27, 40) * mm});
            skLineSegment(sketch, "E1178", {"start": v(28.27, 40) * mm, "end": v(27.97, 39.58) * mm});
            skLineSegment(sketch, "E1179", {"start": v(27.97, 39.58) * mm, "end": v(27.68, 39.16) * mm});
            skLineSegment(sketch, "E1180", {"start": v(27.68, 39.16) * mm, "end": v(27.38, 38.74) * mm});
            skLineSegment(sketch, "E1181", {"start": v(27.38, 38.74) * mm, "end": v(27.08, 38.32) * mm});
            skLineSegment(sketch, "E1182", {"start": v(27.08, 38.32) * mm, "end": v(26.79, 37.9) * mm});
            skLineSegment(sketch, "E1183", {"start": v(26.79, 37.9) * mm, "end": v(26.5, 37.49) * mm});
            skLineSegment(sketch, "E1184", {"start": v(26.5, 37.49) * mm, "end": v(26.2, 37.07) * mm});
            skLineSegment(sketch, "E1185", {"start": v(26.2, 37.07) * mm, "end": v(25.9, 36.65) * mm});
            skLineSegment(sketch, "E1186", {"start": v(25.9, 36.65) * mm, "end": v(25.6, 36.23) * mm});
            skLineSegment(sketch, "E1187", {"start": v(25.6, 36.23) * mm, "end": v(25.31, 35.81) * mm});
            skLineSegment(sketch, "E1188", {"start": v(25.31, 35.81) * mm, "end": v(25.02, 35.4) * mm});
            skLineSegment(sketch, "E1189", {"start": v(25.02, 35.4) * mm, "end": v(24.72, 34.98) * mm});
            skLineSegment(sketch, "E1190", {"start": v(24.72, 34.98) * mm, "end": v(24.42, 34.56) * mm});
            skLineSegment(sketch, "E1191", {"start": v(24.42, 34.56) * mm, "end": v(24.13, 34.14) * mm});
            skLineSegment(sketch, "E1192", {"start": v(24.13, 34.14) * mm, "end": v(23.83, 33.72) * mm});
            skLineSegment(sketch, "E1193", {"start": v(23.83, 33.72) * mm, "end": v(23.54, 33.3) * mm});
            skLineSegment(sketch, "E1194", {"start": v(23.54, 33.3) * mm, "end": v(23.24, 32.89) * mm});
            skLineSegment(sketch, "E1195", {"start": v(23.24, 32.89) * mm, "end": v(22.95, 32.47) * mm});
            skLineSegment(sketch, "E1196", {"start": v(22.95, 32.47) * mm, "end": v(22.7, 32.12) * mm});
            skLineSegment(sketch, "E1197", {"start": v(22.7, 32.12) * mm, "end": v(22.49, 32.59) * mm});
            skLineSegment(sketch, "E1198", {"start": v(22.49, 32.59) * mm, "end": v(22.28, 33.06) * mm});
            skLineSegment(sketch, "E1199", {"start": v(22.28, 33.06) * mm, "end": v(22.1, 33.53) * mm});
            skLineSegment(sketch, "E1200", {"start": v(22.1, 33.53) * mm, "end": v(21.9, 34) * mm});
            skLineSegment(sketch, "E1201", {"start": v(21.9, 34) * mm, "end": v(21.73, 34.49) * mm});
            skLineSegment(sketch, "E1202", {"start": v(21.73, 34.49) * mm, "end": v(21.57, 34.97) * mm});
            skLineSegment(sketch, "E1203", {"start": v(21.57, 34.97) * mm, "end": v(21.42, 35.46) * mm});
            skLineSegment(sketch, "E1204", {"start": v(21.42, 35.46) * mm, "end": v(21.28, 35.95) * mm});
            skLineSegment(sketch, "E1205", {"start": v(21.28, 35.95) * mm, "end": v(21.16, 36.45) * mm});
            skLineSegment(sketch, "E1206", {"start": v(21.16, 36.45) * mm, "end": v(21.04, 36.95) * mm});
            skLineSegment(sketch, "E1207", {"start": v(21.04, 36.95) * mm, "end": v(20.95, 37.45) * mm});
            skLineSegment(sketch, "E1208", {"start": v(20.95, 37.45) * mm, "end": v(20.85, 37.95) * mm});
            skLineSegment(sketch, "E1209", {"start": v(20.85, 37.95) * mm, "end": v(20.77, 38.46) * mm});
            skLineSegment(sketch, "E1210", {"start": v(20.77, 38.46) * mm, "end": v(20.71, 38.96) * mm});
            skLineSegment(sketch, "E1211", {"start": v(20.71, 38.96) * mm, "end": v(20.66, 39.47) * mm});
            skLineSegment(sketch, "E1212", {"start": v(20.66, 39.47) * mm, "end": v(20.61, 39.98) * mm});
            skLineSegment(sketch, "E1213", {"start": v(20.61, 39.98) * mm, "end": v(20.58, 40.5) * mm});
            skLineSegment(sketch, "E1214", {"start": v(20.58, 40.5) * mm, "end": v(20.57, 41) * mm});
            skLineSegment(sketch, "E1215", {"start": v(20.57, 41) * mm, "end": v(20.57, 41.51) * mm});
            skLineSegment(sketch, "E1216", {"start": v(20.57, 41.51) * mm, "end": v(20.57, 42.02) * mm});
            skLineSegment(sketch, "E1217", {"start": v(20.57, 42.02) * mm, "end": v(20.6, 42.53) * mm});
            skLineSegment(sketch, "E1218", {"start": v(20.6, 42.53) * mm, "end": v(20.63, 43.04) * mm});
            skLineSegment(sketch, "E1219", {"start": v(20.63, 43.04) * mm, "end": v(20.67, 43.55) * mm});
            skLineSegment(sketch, "E1220", {"start": v(20.67, 43.55) * mm, "end": v(20.72, 44.06) * mm});
            skLineSegment(sketch, "E1221", {"start": v(20.72, 44.06) * mm, "end": v(20.8, 44.57) * mm});
            skLineSegment(sketch, "E1222", {"start": v(20.8, 44.57) * mm, "end": v(20.88, 45.07) * mm});
            skLineSegment(sketch, "E1223", {"start": v(20.88, 45.07) * mm, "end": v(20.93, 45.4) * mm});
            skLineSegment(sketch, "E1224", {"start": v(20.93, 45.4) * mm, "end": v(20.47, 45.62) * mm});
            skLineSegment(sketch, "E1225", {"start": v(20.47, 45.62) * mm, "end": v(20, 45.82) * mm});
            skLineSegment(sketch, "E1226", {"start": v(20, 45.82) * mm, "end": v(19.74, 45.94) * mm});
            skLineSegment(sketch, "E1227", {"start": v(19.74, 45.94) * mm, "end": v(19.54, 45.47) * mm});
            skLineSegment(sketch, "E1228", {"start": v(19.54, 45.47) * mm, "end": v(19.33, 45) * mm});
            skLineSegment(sketch, "E1229", {"start": v(19.33, 45) * mm, "end": v(19.13, 44.53) * mm});
            skLineSegment(sketch, "E1230", {"start": v(19.13, 44.53) * mm, "end": v(18.93, 44.06) * mm});
            skLineSegment(sketch, "E1231", {"start": v(18.93, 44.06) * mm, "end": v(18.73, 43.59) * mm});
            skLineSegment(sketch, "E1232", {"start": v(18.73, 43.59) * mm, "end": v(18.52, 43.12) * mm});
            skLineSegment(sketch, "E1233", {"start": v(18.52, 43.12) * mm, "end": v(18.32, 42.65) * mm});
            skLineSegment(sketch, "E1234", {"start": v(18.32, 42.65) * mm, "end": v(18.12, 42.18) * mm});
            skLineSegment(sketch, "E1235", {"start": v(18.12, 42.18) * mm, "end": v(17.92, 41.7) * mm});
            skLineSegment(sketch, "E1236", {"start": v(17.92, 41.7) * mm, "end": v(17.72, 41.23) * mm});
            skLineSegment(sketch, "E1237", {"start": v(17.72, 41.23) * mm, "end": v(17.51, 40.76) * mm});
            skLineSegment(sketch, "E1238", {"start": v(17.51, 40.76) * mm, "end": v(17.31, 40.3) * mm});
            skLineSegment(sketch, "E1239", {"start": v(17.31, 40.3) * mm, "end": v(17.1, 39.82) * mm});
            skLineSegment(sketch, "E1240", {"start": v(17.1, 39.82) * mm, "end": v(16.9, 39.35) * mm});
            skLineSegment(sketch, "E1241", {"start": v(16.9, 39.35) * mm, "end": v(16.7, 38.88) * mm});
            skLineSegment(sketch, "E1242", {"start": v(16.7, 38.88) * mm, "end": v(16.5, 38.41) * mm});
            skLineSegment(sketch, "E1243", {"start": v(16.5, 38.41) * mm, "end": v(16.3, 37.94) * mm});
            skLineSegment(sketch, "E1244", {"start": v(16.3, 37.94) * mm, "end": v(16.1, 37.47) * mm});
            skLineSegment(sketch, "E1245", {"start": v(16.1, 37.47) * mm, "end": v(15.9, 37) * mm});
            skLineSegment(sketch, "E1246", {"start": v(15.9, 37) * mm, "end": v(15.7, 36.53) * mm});
            skLineSegment(sketch, "E1247", {"start": v(15.7, 36.53) * mm, "end": v(15.53, 36.14) * mm});
            skLineSegment(sketch, "E1248", {"start": v(15.53, 36.14) * mm, "end": v(15.22, 36.55) * mm});
            skLineSegment(sketch, "E1249", {"start": v(15.22, 36.55) * mm, "end": v(14.92, 36.97) * mm});
            skLineSegment(sketch, "E1250", {"start": v(14.92, 36.97) * mm, "end": v(14.64, 37.4) * mm});
            skLineSegment(sketch, "E1251", {"start": v(14.64, 37.4) * mm, "end": v(14.35, 37.81) * mm});
            skLineSegment(sketch, "E1252", {"start": v(14.35, 37.81) * mm, "end": v(14.08, 38.25) * mm});
            skLineSegment(sketch, "E1253", {"start": v(14.08, 38.25) * mm, "end": v(13.83, 38.7) * mm});
            skLineSegment(sketch, "E1254", {"start": v(13.83, 38.7) * mm, "end": v(13.58, 39.14) * mm});
            skLineSegment(sketch, "E1255", {"start": v(13.58, 39.14) * mm, "end": v(13.34, 39.59) * mm});
            skLineSegment(sketch, "E1256", {"start": v(13.34, 39.59) * mm, "end": v(13.12, 40.05) * mm});
            skLineSegment(sketch, "E1257", {"start": v(13.12, 40.05) * mm, "end": v(12.9, 40.52) * mm});
            skLineSegment(sketch, "E1258", {"start": v(12.9, 40.52) * mm, "end": v(12.7, 40.99) * mm});
            skLineSegment(sketch, "E1259", {"start": v(12.7, 40.99) * mm, "end": v(12.5, 41.45) * mm});
            skLineSegment(sketch, "E1260", {"start": v(12.5, 41.45) * mm, "end": v(12.32, 41.93) * mm});
            skLineSegment(sketch, "E1261", {"start": v(12.32, 41.93) * mm, "end": v(12.16, 42.42) * mm});
            skLineSegment(sketch, "E1262", {"start": v(12.16, 42.42) * mm, "end": v(12, 42.9) * mm});
            skLineSegment(sketch, "E1263", {"start": v(12, 42.9) * mm, "end": v(11.85, 43.4) * mm});
            skLineSegment(sketch, "E1264", {"start": v(11.85, 43.4) * mm, "end": v(11.72, 43.89) * mm});
            skLineSegment(sketch, "E1265", {"start": v(11.72, 43.89) * mm, "end": v(11.6, 44.38) * mm});
            skLineSegment(sketch, "E1266", {"start": v(11.6, 44.38) * mm, "end": v(11.49, 44.88) * mm});
            skLineSegment(sketch, "E1267", {"start": v(11.49, 44.88) * mm, "end": v(11.38, 45.38) * mm});
            skLineSegment(sketch, "E1268", {"start": v(11.38, 45.38) * mm, "end": v(11.3, 45.89) * mm});
            skLineSegment(sketch, "E1269", {"start": v(11.3, 45.89) * mm, "end": v(11.23, 46.4) * mm});
            skLineSegment(sketch, "E1270", {"start": v(11.23, 46.4) * mm, "end": v(11.17, 46.9) * mm});
            skLineSegment(sketch, "E1271", {"start": v(11.17, 46.9) * mm, "end": v(11.1, 47.4) * mm});
            skLineSegment(sketch, "E1272", {"start": v(11.1, 47.4) * mm, "end": v(11.07, 47.92) * mm});
            skLineSegment(sketch, "E1273", {"start": v(11.07, 47.92) * mm, "end": v(11.05, 48.43) * mm});
            skLineSegment(sketch, "E1274", {"start": v(11.05, 48.43) * mm, "end": v(11.03, 48.77) * mm});
            skLineSegment(sketch, "E1275", {"start": v(11.03, 48.77) * mm, "end": v(10.53, 48.87) * mm});
            skLineSegment(sketch, "E1276", {"start": v(10.53, 48.87) * mm, "end": v(10.03, 48.98) * mm});
            skLineSegment(sketch, "E1277", {"start": v(10.03, 48.98) * mm, "end": v(9.75, 49.04) * mm});
            skLineSegment(sketch, "E1278", {"start": v(9.75, 49.04) * mm, "end": v(9.65, 48.54) * mm});
            skLineSegment(sketch, "E1279", {"start": v(9.65, 48.54) * mm, "end": v(9.55, 48.03) * mm});
            skLineSegment(sketch, "E1280", {"start": v(9.55, 48.03) * mm, "end": v(9.45, 47.53) * mm});
            skLineSegment(sketch, "E1281", {"start": v(9.45, 47.53) * mm, "end": v(9.35, 47.03) * mm});
            skLineSegment(sketch, "E1282", {"start": v(9.35, 47.03) * mm, "end": v(9.26, 46.53) * mm});
            skLineSegment(sketch, "E1283", {"start": v(9.26, 46.53) * mm, "end": v(9.16, 46.03) * mm});
            skLineSegment(sketch, "E1284", {"start": v(9.16, 46.03) * mm, "end": v(9.06, 45.52) * mm});
            skLineSegment(sketch, "E1285", {"start": v(9.06, 45.52) * mm, "end": v(8.96, 45.02) * mm});
            skLineSegment(sketch, "E1286", {"start": v(8.96, 45.02) * mm, "end": v(8.86, 44.52) * mm});
            skLineSegment(sketch, "E1287", {"start": v(8.86, 44.52) * mm, "end": v(8.76, 44.02) * mm});
            skLineSegment(sketch, "E1288", {"start": v(8.76, 44.02) * mm, "end": v(8.66, 43.52) * mm});
            skLineSegment(sketch, "E1289", {"start": v(8.66, 43.52) * mm, "end": v(8.56, 43.01) * mm});
            skLineSegment(sketch, "E1290", {"start": v(8.56, 43.01) * mm, "end": v(8.46, 42.51) * mm});
            skLineSegment(sketch, "E1291", {"start": v(8.46, 42.51) * mm, "end": v(8.36, 42) * mm});
            skLineSegment(sketch, "E1292", {"start": v(8.36, 42) * mm, "end": v(8.26, 41.5) * mm});
            skLineSegment(sketch, "E1293", {"start": v(8.26, 41.5) * mm, "end": v(8.16, 41) * mm});
            skLineSegment(sketch, "E1294", {"start": v(8.16, 41) * mm, "end": v(8.06, 40.5) * mm});
            skLineSegment(sketch, "E1295", {"start": v(8.06, 40.5) * mm, "end": v(7.96, 40) * mm});
            skLineSegment(sketch, "E1296", {"start": v(7.96, 40) * mm, "end": v(7.86, 39.5) * mm});
            skLineSegment(sketch, "E1297", {"start": v(7.86, 39.5) * mm, "end": v(7.76, 39) * mm});
            skLineSegment(sketch, "E1298", {"start": v(7.76, 39) * mm, "end": v(7.67, 38.58) * mm});
            skLineSegment(sketch, "E1299", {"start": v(7.67, 38.58) * mm, "end": v(7.29, 38.92) * mm});
            skLineSegment(sketch, "E1300", {"start": v(7.29, 38.92) * mm, "end": v(6.91, 39.26) * mm});
            skLineSegment(sketch, "E1301", {"start": v(6.91, 39.26) * mm, "end": v(6.54, 39.62) * mm});
            skLineSegment(sketch, "E1302", {"start": v(6.54, 39.62) * mm, "end": v(6.18, 39.97) * mm});
            skLineSegment(sketch, "E1303", {"start": v(6.18, 39.97) * mm, "end": v(5.82, 40.34) * mm});
            skLineSegment(sketch, "E1304", {"start": v(5.82, 40.34) * mm, "end": v(5.48, 40.72) * mm});
            skLineSegment(sketch, "E1305", {"start": v(5.48, 40.72) * mm, "end": v(5.15, 41.11) * mm});
            skLineSegment(sketch, "E1306", {"start": v(5.15, 41.11) * mm, "end": v(4.82, 41.5) * mm});
            skLineSegment(sketch, "E1307", {"start": v(4.82, 41.5) * mm, "end": v(4.5, 41.9) * mm});
            skLineSegment(sketch, "E1308", {"start": v(4.5, 41.9) * mm, "end": v(4.2, 42.31) * mm});
            skLineSegment(sketch, "E1309", {"start": v(4.2, 42.31) * mm, "end": v(3.9, 42.73) * mm});
            skLineSegment(sketch, "E1310", {"start": v(3.9, 42.73) * mm, "end": v(3.61, 43.15) * mm});
            skLineSegment(sketch, "E1311", {"start": v(3.61, 43.15) * mm, "end": v(3.34, 43.58) * mm});
            skLineSegment(sketch, "E1312", {"start": v(3.34, 43.58) * mm, "end": v(3.07, 44.02) * mm});
            skLineSegment(sketch, "E1313", {"start": v(3.07, 44.02) * mm, "end": v(2.82, 44.46) * mm});
            skLineSegment(sketch, "E1314", {"start": v(2.82, 44.46) * mm, "end": v(2.57, 44.9) * mm});
            skLineSegment(sketch, "E1315", {"start": v(2.57, 44.9) * mm, "end": v(2.34, 45.36) * mm});
            skLineSegment(sketch, "E1316", {"start": v(2.34, 45.36) * mm, "end": v(2.11, 45.82) * mm});
            skLineSegment(sketch, "E1317", {"start": v(2.11, 45.82) * mm, "end": v(1.9, 46.3) * mm});
            skLineSegment(sketch, "E1318", {"start": v(1.9, 46.3) * mm, "end": v(1.7, 46.76) * mm});
            skLineSegment(sketch, "E1319", {"start": v(1.7, 46.76) * mm, "end": v(1.51, 47.23) * mm});
            skLineSegment(sketch, "E1320", {"start": v(1.51, 47.23) * mm, "end": v(1.33, 47.71) * mm});
            skLineSegment(sketch, "E1321", {"start": v(1.33, 47.71) * mm, "end": v(1.17, 48.2) * mm});
            skLineSegment(sketch, "E1322", {"start": v(1.17, 48.2) * mm, "end": v(1, 48.68) * mm});
            skLineSegment(sketch, "E1323", {"start": v(1, 48.68) * mm, "end": v(0.87, 49.17) * mm});
            skLineSegment(sketch, "E1324", {"start": v(0.87, 49.17) * mm, "end": v(0.74, 49.67) * mm});
            skLineSegment(sketch, "E1325", {"start": v(0.74, 49.67) * mm, "end": v(0.65, 50) * mm});
            skLineSegment(sketch, "E1326", {"start": v(0.65, 50) * mm, "end": v(0.14, 50) * mm});
            skLineSegment(sketch, "E1327", {"start": v(0.14, 50) * mm, "end": v(-0.37, 50) * mm});
            skLineSegment(sketch, "E1328", {"start": v(-0.37, 50) * mm, "end": v(-0.65, 50) * mm});
            skLineSegment(sketch, "E1329", {"start": v(-0.65, 50) * mm, "end": v(-0.65, 49.48) * mm});
            skLineSegment(sketch, "E1330", {"start": v(-0.65, 49.48) * mm, "end": v(-0.64, 48.97) * mm});
            skLineSegment(sketch, "E1331", {"start": v(-0.64, 48.97) * mm, "end": v(-0.63, 48.46) * mm});
            skLineSegment(sketch, "E1332", {"start": v(-0.63, 48.46) * mm, "end": v(-0.63, 47.95) * mm});
            skLineSegment(sketch, "E1333", {"start": v(-0.63, 47.95) * mm, "end": v(-0.62, 47.44) * mm});
            skLineSegment(sketch, "E1334", {"start": v(-0.62, 47.44) * mm, "end": v(-0.61, 46.92) * mm});
            skLineSegment(sketch, "E1335", {"start": v(-0.61, 46.92) * mm, "end": v(-0.6, 46.41) * mm});
            skLineSegment(sketch, "E1336", {"start": v(-0.6, 46.41) * mm, "end": v(-0.6, 45.9) * mm});
            skLineSegment(sketch, "E1337", {"start": v(-0.6, 45.9) * mm, "end": v(-0.6, 45.39) * mm});
            skLineSegment(sketch, "E1338", {"start": v(-0.6, 45.39) * mm, "end": v(-0.59, 44.88) * mm});
            skLineSegment(sketch, "E1339", {"start": v(-0.59, 44.88) * mm, "end": v(-0.58, 44.36) * mm});
            skLineSegment(sketch, "E1340", {"start": v(-0.58, 44.36) * mm, "end": v(-0.57, 43.85) * mm});
            skLineSegment(sketch, "E1341", {"start": v(-0.57, 43.85) * mm, "end": v(-0.57, 43.34) * mm});
            skLineSegment(sketch, "E1342", {"start": v(-0.57, 43.34) * mm, "end": v(-0.56, 42.83) * mm});
            skLineSegment(sketch, "E1343", {"start": v(-0.56, 42.83) * mm, "end": v(-0.55, 42.32) * mm});
            skLineSegment(sketch, "E1344", {"start": v(-0.55, 42.32) * mm, "end": v(-0.55, 41.8) * mm});
            skLineSegment(sketch, "E1345", {"start": v(-0.55, 41.8) * mm, "end": v(-0.54, 41.3) * mm});
            skLineSegment(sketch, "E1346", {"start": v(-0.54, 41.3) * mm, "end": v(-0.53, 40.78) * mm});
            skLineSegment(sketch, "E1347", {"start": v(-0.53, 40.78) * mm, "end": v(-0.53, 40.27) * mm});
            skLineSegment(sketch, "E1348", {"start": v(-0.53, 40.27) * mm, "end": v(-0.52, 39.76) * mm});
            skLineSegment(sketch, "E1349", {"start": v(-0.52, 39.76) * mm, "end": v(-0.51, 39.33) * mm});
            skLineSegment(sketch, "E1350", {"start": v(-0.51, 39.33) * mm, "end": v(-0.96, 39.58) * mm});
            skLineSegment(sketch, "E1351", {"start": v(-0.96, 39.58) * mm, "end": v(-1.4, 39.84) * mm});
            skLineSegment(sketch, "E1352", {"start": v(-1.4, 39.84) * mm, "end": v(-1.84, 40.11) * mm});
            skLineSegment(sketch, "E1353", {"start": v(-1.84, 40.11) * mm, "end": v(-2.27, 40.38) * mm});
            skLineSegment(sketch, "E1354", {"start": v(-2.27, 40.38) * mm, "end": v(-2.7, 40.67) * mm});
            skLineSegment(sketch, "E1355", {"start": v(-2.7, 40.67) * mm, "end": v(-3.1, 40.97) * mm});
            skLineSegment(sketch, "E1356", {"start": v(-3.1, 40.97) * mm, "end": v(-3.51, 41.28) * mm});
            skLineSegment(sketch, "E1357", {"start": v(-3.51, 41.28) * mm, "end": v(-3.92, 41.6) * mm});
            skLineSegment(sketch, "E1358", {"start": v(-3.92, 41.6) * mm, "end": v(-4.3, 41.92) * mm});
            skLineSegment(sketch, "E1359", {"start": v(-4.3, 41.92) * mm, "end": v(-4.7, 42.26) * mm});
            skLineSegment(sketch, "E1360", {"start": v(-4.7, 42.26) * mm, "end": v(-5.07, 42.6) * mm});
            skLineSegment(sketch, "E1361", {"start": v(-5.07, 42.6) * mm, "end": v(-5.44, 42.96) * mm});
            skLineSegment(sketch, "E1362", {"start": v(-5.44, 42.96) * mm, "end": v(-5.8, 43.32) * mm});
            skLineSegment(sketch, "E1363", {"start": v(-5.8, 43.32) * mm, "end": v(-6.15, 43.7) * mm});
            skLineSegment(sketch, "E1364", {"start": v(-6.15, 43.7) * mm, "end": v(-6.49, 44.08) * mm});
            skLineSegment(sketch, "E1365", {"start": v(-6.49, 44.08) * mm, "end": v(-6.82, 44.46) * mm});
            skLineSegment(sketch, "E1366", {"start": v(-6.82, 44.46) * mm, "end": v(-7.15, 44.86) * mm});
            skLineSegment(sketch, "E1367", {"start": v(-7.15, 44.86) * mm, "end": v(-7.46, 45.26) * mm});
            skLineSegment(sketch, "E1368", {"start": v(-7.46, 45.26) * mm, "end": v(-7.76, 45.68) * mm});
            skLineSegment(sketch, "E1369", {"start": v(-7.76, 45.68) * mm, "end": v(-8.06, 46.09) * mm});
            skLineSegment(sketch, "E1370", {"start": v(-8.06, 46.09) * mm, "end": v(-8.34, 46.51) * mm});
            skLineSegment(sketch, "E1371", {"start": v(-8.34, 46.51) * mm, "end": v(-8.61, 46.95) * mm});
            skLineSegment(sketch, "E1372", {"start": v(-8.61, 46.95) * mm, "end": v(-8.87, 47.39) * mm});
            skLineSegment(sketch, "E1373", {"start": v(-8.87, 47.39) * mm, "end": v(-9.13, 47.83) * mm});
            skLineSegment(sketch, "E1374", {"start": v(-9.13, 47.83) * mm, "end": v(-9.37, 48.28) * mm});
            skLineSegment(sketch, "E1375", {"start": v(-9.37, 48.28) * mm, "end": v(-9.6, 48.74) * mm});
            skLineSegment(sketch, "E1376", {"start": v(-9.6, 48.74) * mm, "end": v(-9.75, 49.04) * mm});
            skLineSegment(sketch, "E1377", {"start": v(-9.75, 49.04) * mm, "end": v(-10.26, 48.93) * mm});
            skLineSegment(sketch, "E1378", {"start": v(-10.26, 48.93) * mm, "end": v(-10.76, 48.83) * mm});
            skLineSegment(sketch, "E1379", {"start": v(-10.76, 48.83) * mm, "end": v(-11.03, 48.77) * mm});
            skLineSegment(sketch, "E1380", {"start": v(-11.03, 48.77) * mm, "end": v(-10.92, 48.27) * mm});
            skLineSegment(sketch, "E1381", {"start": v(-10.92, 48.27) * mm, "end": v(-10.8, 47.77) * mm});
            skLineSegment(sketch, "E1382", {"start": v(-10.8, 47.77) * mm, "end": v(-10.7, 47.27) * mm});
            skLineSegment(sketch, "E1383", {"start": v(-10.7, 47.27) * mm, "end": v(-10.58, 46.77) * mm});
            skLineSegment(sketch, "E1384", {"start": v(-10.58, 46.77) * mm, "end": v(-10.47, 46.27) * mm});
            skLineSegment(sketch, "E1385", {"start": v(-10.47, 46.27) * mm, "end": v(-10.36, 45.77) * mm});
            skLineSegment(sketch, "E1386", {"start": v(-10.36, 45.77) * mm, "end": v(-10.24, 45.27) * mm});
            skLineSegment(sketch, "E1387", {"start": v(-10.24, 45.27) * mm, "end": v(-10.13, 44.77) * mm});
            skLineSegment(sketch, "E1388", {"start": v(-10.13, 44.77) * mm, "end": v(-10.02, 44.27) * mm});
            skLineSegment(sketch, "E1389", {"start": v(-10.02, 44.27) * mm, "end": v(-9.9, 43.77) * mm});
            skLineSegment(sketch, "E1390", {"start": v(-9.9, 43.77) * mm, "end": v(-9.8, 43.27) * mm});
            skLineSegment(sketch, "E1391", {"start": v(-9.8, 43.27) * mm, "end": v(-9.68, 42.77) * mm});
            skLineSegment(sketch, "E1392", {"start": v(-9.68, 42.77) * mm, "end": v(-9.57, 42.27) * mm});
            skLineSegment(sketch, "E1393", {"start": v(-9.57, 42.27) * mm, "end": v(-9.45, 41.78) * mm});
            skLineSegment(sketch, "E1394", {"start": v(-9.45, 41.78) * mm, "end": v(-9.34, 41.28) * mm});
            skLineSegment(sketch, "E1395", {"start": v(-9.34, 41.28) * mm, "end": v(-9.23, 40.78) * mm});
            skLineSegment(sketch, "E1396", {"start": v(-9.23, 40.78) * mm, "end": v(-9.11, 40.28) * mm});
            skLineSegment(sketch, "E1397", {"start": v(-9.11, 40.28) * mm, "end": v(-9, 39.78) * mm});
            skLineSegment(sketch, "E1398", {"start": v(-9, 39.78) * mm, "end": v(-8.89, 39.28) * mm});
            skLineSegment(sketch, "E1399", {"start": v(-8.89, 39.28) * mm, "end": v(-8.77, 38.78) * mm});
            skLineSegment(sketch, "E1400", {"start": v(-8.77, 38.78) * mm, "end": v(-8.68, 38.37) * mm});
            skLineSegment(sketch, "E1401", {"start": v(-8.68, 38.37) * mm, "end": v(-9.17, 38.52) * mm});
            skLineSegment(sketch, "E1402", {"start": v(-9.17, 38.52) * mm, "end": v(-9.66, 38.68) * mm});
            skLineSegment(sketch, "E1403", {"start": v(-9.66, 38.68) * mm, "end": v(-10.14, 38.85) * mm});
            skLineSegment(sketch, "E1404", {"start": v(-10.14, 38.85) * mm, "end": v(-10.62, 39.03) * mm});
            skLineSegment(sketch, "E1405", {"start": v(-10.62, 39.03) * mm, "end": v(-11.09, 39.22) * mm});
            skLineSegment(sketch, "E1406", {"start": v(-11.09, 39.22) * mm, "end": v(-11.56, 39.43) * mm});
            skLineSegment(sketch, "E1407", {"start": v(-11.56, 39.43) * mm, "end": v(-12.02, 39.65) * mm});
            skLineSegment(sketch, "E1408", {"start": v(-12.02, 39.65) * mm, "end": v(-12.48, 39.87) * mm});
            skLineSegment(sketch, "E1409", {"start": v(-12.48, 39.87) * mm, "end": v(-12.93, 40.11) * mm});
            skLineSegment(sketch, "E1410", {"start": v(-12.93, 40.11) * mm, "end": v(-13.38, 40.36) * mm});
            skLineSegment(sketch, "E1411", {"start": v(-13.38, 40.36) * mm, "end": v(-13.82, 40.63) * mm});
            skLineSegment(sketch, "E1412", {"start": v(-13.82, 40.63) * mm, "end": v(-14.25, 40.89) * mm});
            skLineSegment(sketch, "E1413", {"start": v(-14.25, 40.89) * mm, "end": v(-14.68, 41.17) * mm});
            skLineSegment(sketch, "E1414", {"start": v(-14.68, 41.17) * mm, "end": v(-15.1, 41.46) * mm});
            skLineSegment(sketch, "E1415", {"start": v(-15.1, 41.46) * mm, "end": v(-15.5, 41.77) * mm});
            skLineSegment(sketch, "E1416", {"start": v(-15.5, 41.77) * mm, "end": v(-15.92, 42.07) * mm});
            skLineSegment(sketch, "E1417", {"start": v(-15.92, 42.07) * mm, "end": v(-16.32, 42.4) * mm});
            skLineSegment(sketch, "E1418", {"start": v(-16.32, 42.4) * mm, "end": v(-16.7, 42.72) * mm});
            skLineSegment(sketch, "E1419", {"start": v(-16.7, 42.72) * mm, "end": v(-17.09, 43.06) * mm});
            skLineSegment(sketch, "E1420", {"start": v(-17.09, 43.06) * mm, "end": v(-17.47, 43.4) * mm});
            skLineSegment(sketch, "E1421", {"start": v(-17.47, 43.4) * mm, "end": v(-17.83, 43.76) * mm});
            skLineSegment(sketch, "E1422", {"start": v(-17.83, 43.76) * mm, "end": v(-18.19, 44.13) * mm});
            skLineSegment(sketch, "E1423", {"start": v(-18.19, 44.13) * mm, "end": v(-18.53, 44.5) * mm});
            skLineSegment(sketch, "E1424", {"start": v(-18.53, 44.5) * mm, "end": v(-18.88, 44.88) * mm});
            skLineSegment(sketch, "E1425", {"start": v(-18.88, 44.88) * mm, "end": v(-19.2, 45.27) * mm});
            skLineSegment(sketch, "E1426", {"start": v(-19.2, 45.27) * mm, "end": v(-19.53, 45.67) * mm});
            skLineSegment(sketch, "E1427", {"start": v(-19.53, 45.67) * mm, "end": v(-19.74, 45.94) * mm});
            skLineSegment(sketch, "E1428", {"start": v(-19.74, 45.94) * mm, "end": v(-20.2, 45.73) * mm});
            skLineSegment(sketch, "E1429", {"start": v(-20.2, 45.73) * mm, "end": v(-20.67, 45.52) * mm});
            skLineSegment(sketch, "E1430", {"start": v(-20.67, 45.52) * mm, "end": v(-20.93, 45.4) * mm});
            skLineSegment(sketch, "E1431", {"start": v(-20.93, 45.4) * mm, "end": v(-20.72, 44.94) * mm});
            skLineSegment(sketch, "E1432", {"start": v(-20.72, 44.94) * mm, "end": v(-20.5, 44.48) * mm});
            skLineSegment(sketch, "E1433", {"start": v(-20.5, 44.48) * mm, "end": v(-20.29, 44.01) * mm});
            skLineSegment(sketch, "E1434", {"start": v(-20.29, 44.01) * mm, "end": v(-20.08, 43.55) * mm});
            skLineSegment(sketch, "E1435", {"start": v(-20.08, 43.55) * mm, "end": v(-19.86, 43.08) * mm});
            skLineSegment(sketch, "E1436", {"start": v(-19.86, 43.08) * mm, "end": v(-19.65, 42.62) * mm});
            skLineSegment(sketch, "E1437", {"start": v(-19.65, 42.62) * mm, "end": v(-19.43, 42.15) * mm});
            skLineSegment(sketch, "E1438", {"start": v(-19.43, 42.15) * mm, "end": v(-19.22, 41.69) * mm});
            skLineSegment(sketch, "E1439", {"start": v(-19.22, 41.69) * mm, "end": v(-19, 41.22) * mm});
            skLineSegment(sketch, "E1440", {"start": v(-19, 41.22) * mm, "end": v(-18.79, 40.76) * mm});
            skLineSegment(sketch, "E1441", {"start": v(-18.79, 40.76) * mm, "end": v(-18.57, 40.3) * mm});
            skLineSegment(sketch, "E1442", {"start": v(-18.57, 40.3) * mm, "end": v(-18.36, 39.83) * mm});
            skLineSegment(sketch, "E1443", {"start": v(-18.36, 39.83) * mm, "end": v(-18.15, 39.36) * mm});
            skLineSegment(sketch, "E1444", {"start": v(-18.15, 39.36) * mm, "end": v(-17.93, 38.9) * mm});
            skLineSegment(sketch, "E1445", {"start": v(-17.93, 38.9) * mm, "end": v(-17.72, 38.43) * mm});
            skLineSegment(sketch, "E1446", {"start": v(-17.72, 38.43) * mm, "end": v(-17.5, 37.97) * mm});
            skLineSegment(sketch, "E1447", {"start": v(-17.5, 37.97) * mm, "end": v(-17.29, 37.5) * mm});
            skLineSegment(sketch, "E1448", {"start": v(-17.29, 37.5) * mm, "end": v(-17.07, 37.04) * mm});
            skLineSegment(sketch, "E1449", {"start": v(-17.07, 37.04) * mm, "end": v(-16.86, 36.57) * mm});
            skLineSegment(sketch, "E1450", {"start": v(-16.86, 36.57) * mm, "end": v(-16.65, 36.1) * mm});
            skLineSegment(sketch, "E1451", {"start": v(-16.65, 36.1) * mm, "end": v(-16.47, 35.72) * mm});
            skLineSegment(sketch, "E1452", {"start": v(-16.47, 35.72) * mm, "end": v(-16.98, 35.77) * mm});
            skLineSegment(sketch, "E1453", {"start": v(-16.98, 35.77) * mm, "end": v(-17.49, 35.83) * mm});
            skLineSegment(sketch, "E1454", {"start": v(-17.49, 35.83) * mm, "end": v(-18, 35.9) * mm});
            skLineSegment(sketch, "E1455", {"start": v(-18, 35.9) * mm, "end": v(-18.5, 35.97) * mm});
            skLineSegment(sketch, "E1456", {"start": v(-18.5, 35.97) * mm, "end": v(-19, 36.06) * mm});
            skLineSegment(sketch, "E1457", {"start": v(-19, 36.06) * mm, "end": v(-19.5, 36.17) * mm});
            skLineSegment(sketch, "E1458", {"start": v(-19.5, 36.17) * mm, "end": v(-20, 36.29) * mm});
            skLineSegment(sketch, "E1459", {"start": v(-20, 36.29) * mm, "end": v(-20.5, 36.4) * mm});
            skLineSegment(sketch, "E1460", {"start": v(-20.5, 36.4) * mm, "end": v(-20.99, 36.55) * mm});
            skLineSegment(sketch, "E1461", {"start": v(-20.99, 36.55) * mm, "end": v(-21.48, 36.7) * mm});
            skLineSegment(sketch, "E1462", {"start": v(-21.48, 36.7) * mm, "end": v(-21.96, 36.87) * mm});
            skLineSegment(sketch, "E1463", {"start": v(-21.96, 36.87) * mm, "end": v(-22.44, 37.03) * mm});
            skLineSegment(sketch, "E1464", {"start": v(-22.44, 37.03) * mm, "end": v(-22.92, 37.22) * mm});
            skLineSegment(sketch, "E1465", {"start": v(-22.92, 37.22) * mm, "end": v(-23.39, 37.42) * mm});
            skLineSegment(sketch, "E1466", {"start": v(-23.39, 37.42) * mm, "end": v(-23.85, 37.63) * mm});
            skLineSegment(sketch, "E1467", {"start": v(-23.85, 37.63) * mm, "end": v(-24.32, 37.84) * mm});
            skLineSegment(sketch, "E1468", {"start": v(-24.32, 37.84) * mm, "end": v(-24.77, 38.07) * mm});
            skLineSegment(sketch, "E1469", {"start": v(-24.77, 38.07) * mm, "end": v(-25.22, 38.32) * mm});
            skLineSegment(sketch, "E1470", {"start": v(-25.22, 38.32) * mm, "end": v(-25.67, 38.57) * mm});
            skLineSegment(sketch, "E1471", {"start": v(-25.67, 38.57) * mm, "end": v(-26.1, 38.82) * mm});
            skLineSegment(sketch, "E1472", {"start": v(-26.1, 38.82) * mm, "end": v(-26.54, 39.1) * mm});
            skLineSegment(sketch, "E1473", {"start": v(-26.54, 39.1) * mm, "end": v(-26.96, 39.39) * mm});
            skLineSegment(sketch, "E1474", {"start": v(-26.96, 39.39) * mm, "end": v(-27.38, 39.68) * mm});
            skLineSegment(sketch, "E1475", {"start": v(-27.38, 39.68) * mm, "end": v(-27.8, 39.98) * mm});
            skLineSegment(sketch, "E1476", {"start": v(-27.8, 39.98) * mm, "end": v(-28.2, 40.3) * mm});
            skLineSegment(sketch, "E1477", {"start": v(-28.2, 40.3) * mm, "end": v(-28.6, 40.62) * mm});
            skLineSegment(sketch, "E1478", {"start": v(-28.6, 40.62) * mm, "end": v(-28.86, 40.83) * mm});
            skLineSegment(sketch, "E1479", {"start": v(-28.86, 40.83) * mm, "end": v(-29.27, 40.53) * mm});
            skLineSegment(sketch, "E1480", {"start": v(-29.27, 40.53) * mm, "end": v(-29.69, 40.23) * mm});
            skLineSegment(sketch, "E1481", {"start": v(-29.69, 40.23) * mm, "end": v(-29.92, 40.06) * mm});
            skLineSegment(sketch, "E1482", {"start": v(-29.92, 40.06) * mm, "end": v(-29.6, 39.65) * mm});
            skLineSegment(sketch, "E1483", {"start": v(-29.6, 39.65) * mm, "end": v(-29.3, 39.24) * mm});
            skLineSegment(sketch, "E1484", {"start": v(-29.3, 39.24) * mm, "end": v(-29, 38.83) * mm});
            skLineSegment(sketch, "E1485", {"start": v(-29, 38.83) * mm, "end": v(-28.7, 38.42) * mm});
            skLineSegment(sketch, "E1486", {"start": v(-28.7, 38.42) * mm, "end": v(-28.38, 38.01) * mm});
            skLineSegment(sketch, "E1487", {"start": v(-28.38, 38.01) * mm, "end": v(-28.08, 37.6) * mm});
            skLineSegment(sketch, "E1488", {"start": v(-28.08, 37.6) * mm, "end": v(-27.77, 37.2) * mm});
            skLineSegment(sketch, "E1489", {"start": v(-27.77, 37.2) * mm, "end": v(-27.47, 36.78) * mm});
            skLineSegment(sketch, "E1490", {"start": v(-27.47, 36.78) * mm, "end": v(-27.16, 36.37) * mm});
            skLineSegment(sketch, "E1491", {"start": v(-27.16, 36.37) * mm, "end": v(-26.85, 35.96) * mm});
            skLineSegment(sketch, "E1492", {"start": v(-26.85, 35.96) * mm, "end": v(-26.55, 35.55) * mm});
            skLineSegment(sketch, "E1493", {"start": v(-26.55, 35.55) * mm, "end": v(-26.24, 35.14) * mm});
            skLineSegment(sketch, "E1494", {"start": v(-26.24, 35.14) * mm, "end": v(-25.93, 34.73) * mm});
            skLineSegment(sketch, "E1495", {"start": v(-25.93, 34.73) * mm, "end": v(-25.63, 34.32) * mm});
            skLineSegment(sketch, "E1496", {"start": v(-25.63, 34.32) * mm, "end": v(-25.32, 33.9) * mm});
            skLineSegment(sketch, "E1497", {"start": v(-25.32, 33.9) * mm, "end": v(-25.01, 33.5) * mm});
            skLineSegment(sketch, "E1498", {"start": v(-25.01, 33.5) * mm, "end": v(-24.7, 33.09) * mm});
            skLineSegment(sketch, "E1499", {"start": v(-24.7, 33.09) * mm, "end": v(-24.4, 32.68) * mm});
            skLineSegment(sketch, "E1500", {"start": v(-24.4, 32.68) * mm, "end": v(-24.1, 32.27) * mm});
            skLineSegment(sketch, "E1501", {"start": v(-24.1, 32.27) * mm, "end": v(-23.79, 31.86) * mm});
            skLineSegment(sketch, "E1502", {"start": v(-23.79, 31.86) * mm, "end": v(-23.54, 31.52) * mm});
            skLineSegment(sketch, "E1503", {"start": v(-23.54, 31.52) * mm, "end": v(-24.04, 31.46) * mm});
            skLineSegment(sketch, "E1504", {"start": v(-24.04, 31.46) * mm, "end": v(-24.55, 31.4) * mm});
            skLineSegment(sketch, "E1505", {"start": v(-24.55, 31.4) * mm, "end": v(-25.07, 31.37) * mm});
            skLineSegment(sketch, "E1506", {"start": v(-25.07, 31.37) * mm, "end": v(-25.57, 31.34) * mm});
            skLineSegment(sketch, "E1507", {"start": v(-25.57, 31.34) * mm, "end": v(-26.08, 31.32) * mm});
            skLineSegment(sketch, "E1508", {"start": v(-26.08, 31.32) * mm, "end": v(-26.25, 31.32) * mm});
            skLineSegment(sketch, "E1509", {"start": v(-26.25, 31.32) * mm, "end": v(-26.77, 31.32) * mm});
            skLineSegment(sketch, "E1510", {"start": v(-26.77, 31.32) * mm, "end": v(-27.28, 31.34) * mm});
            skLineSegment(sketch, "E1511", {"start": v(-27.28, 31.34) * mm, "end": v(-27.79, 31.37) * mm});
            skLineSegment(sketch, "E1512", {"start": v(-27.79, 31.37) * mm, "end": v(-28.3, 31.4) * mm});
            skLineSegment(sketch, "E1513", {"start": v(-28.3, 31.4) * mm, "end": v(-28.8, 31.45) * mm});
            skLineSegment(sketch, "E1514", {"start": v(-28.8, 31.45) * mm, "end": v(-29.31, 31.51) * mm});
            skLineSegment(sketch, "E1515", {"start": v(-29.31, 31.51) * mm, "end": v(-29.82, 31.6) * mm});
            skLineSegment(sketch, "E1516", {"start": v(-29.82, 31.6) * mm, "end": v(-30.32, 31.67) * mm});
            skLineSegment(sketch, "E1517", {"start": v(-30.32, 31.67) * mm, "end": v(-30.82, 31.77) * mm});
            skLineSegment(sketch, "E1518", {"start": v(-30.82, 31.77) * mm, "end": v(-31.32, 31.88) * mm});
            skLineSegment(sketch, "E1519", {"start": v(-31.32, 31.88) * mm, "end": v(-31.82, 32) * mm});
            skLineSegment(sketch, "E1520", {"start": v(-31.82, 32) * mm, "end": v(-32.31, 32.13) * mm});
            skLineSegment(sketch, "E1521", {"start": v(-32.31, 32.13) * mm, "end": v(-32.8, 32.28) * mm});
            skLineSegment(sketch, "E1522", {"start": v(-32.8, 32.28) * mm, "end": v(-33.29, 32.44) * mm});
            skLineSegment(sketch, "E1523", {"start": v(-33.29, 32.44) * mm, "end": v(-33.77, 32.61) * mm});
            skLineSegment(sketch, "E1524", {"start": v(-33.77, 32.61) * mm, "end": v(-34.25, 32.79) * mm});
            skLineSegment(sketch, "E1525", {"start": v(-34.25, 32.79) * mm, "end": v(-34.72, 32.98) * mm});
            skLineSegment(sketch, "E1526", {"start": v(-34.72, 32.98) * mm, "end": v(-35.2, 33.19) * mm});
            skLineSegment(sketch, "E1527", {"start": v(-35.2, 33.19) * mm, "end": v(-35.65, 33.4) * mm});
            skLineSegment(sketch, "E1528", {"start": v(-35.65, 33.4) * mm, "end": v(-36.11, 33.62) * mm});
            skLineSegment(sketch, "E1529", {"start": v(-36.11, 33.62) * mm, "end": v(-36.57, 33.86) * mm});
            skLineSegment(sketch, "E1530", {"start": v(-36.57, 33.86) * mm, "end": v(-36.72, 33.94) * mm});
            skLineSegment(sketch, "E1531", {"start": v(-5.33, 2.11) * mm, "end": v(-5.19, 2.44) * mm});
            skLineSegment(sketch, "E1532", {"start": v(-5.19, 2.44) * mm, "end": v(-5.02, 2.76) * mm});
            skLineSegment(sketch, "E1533", {"start": v(-5.02, 2.76) * mm, "end": v(-4.84, 3.07) * mm});
            skLineSegment(sketch, "E1534", {"start": v(-4.84, 3.07) * mm, "end": v(-4.64, 3.37) * mm});
            skLineSegment(sketch, "E1535", {"start": v(-4.64, 3.37) * mm, "end": v(-4.42, 3.65) * mm});
            skLineSegment(sketch, "E1536", {"start": v(-4.42, 3.65) * mm, "end": v(-4.18, 3.92) * mm});
            skLineSegment(sketch, "E1537", {"start": v(-4.18, 3.92) * mm, "end": v(-3.92, 4.18) * mm});
            skLineSegment(sketch, "E1538", {"start": v(-3.92, 4.18) * mm, "end": v(-3.65, 4.42) * mm});
            skLineSegment(sketch, "E1539", {"start": v(-3.65, 4.42) * mm, "end": v(-3.37, 4.64) * mm});
            skLineSegment(sketch, "E1540", {"start": v(-3.37, 4.64) * mm, "end": v(-3.07, 4.84) * mm});
            skLineSegment(sketch, "E1541", {"start": v(-3.07, 4.84) * mm, "end": v(-2.76, 5.02) * mm});
            skLineSegment(sketch, "E1542", {"start": v(-2.76, 5.02) * mm, "end": v(-2.44, 5.19) * mm});
            skLineSegment(sketch, "E1543", {"start": v(-2.44, 5.19) * mm, "end": v(-2.11, 5.33) * mm});
            skLineSegment(sketch, "E1544", {"start": v(-2.11, 5.33) * mm, "end": v(-1.98, 5.38) * mm});
            skLineSegment(sketch, "E1545", {"start": v(-1.98, 5.38) * mm, "end": v(-2.07, 35.34) * mm});
            skLineSegment(sketch, "E1546", {"start": v(-2.07, 35.34) * mm, "end": v(-2.22, 35.33) * mm});
            skLineSegment(sketch, "E1547", {"start": v(-2.22, 35.33) * mm, "end": v(-4.44, 35.12) * mm});
            skLineSegment(sketch, "E1548", {"start": v(-4.44, 35.12) * mm, "end": v(-6.63, 34.77) * mm});
            skLineSegment(sketch, "E1549", {"start": v(-6.63, 34.77) * mm, "end": v(-8.8, 34.29) * mm});
            skLineSegment(sketch, "E1550", {"start": v(-8.8, 34.29) * mm, "end": v(-10.94, 33.67) * mm});
            skLineSegment(sketch, "E1551", {"start": v(-10.94, 33.67) * mm, "end": v(-13.03, 32.92) * mm});
            skLineSegment(sketch, "E1552", {"start": v(-13.03, 32.92) * mm, "end": v(-15.07, 32.03) * mm});
            skLineSegment(sketch, "E1553", {"start": v(-15.07, 32.03) * mm, "end": v(-17.06, 31.02) * mm});
            skLineSegment(sketch, "E1554", {"start": v(-17.06, 31.02) * mm, "end": v(-18.97, 29.9) * mm});
            skLineSegment(sketch, "E1555", {"start": v(-18.97, 29.9) * mm, "end": v(-20.8, 28.64) * mm});
            skLineSegment(sketch, "E1556", {"start": v(-20.8, 28.64) * mm, "end": v(-22.57, 27.28) * mm});
            skLineSegment(sketch, "E1557", {"start": v(-22.57, 27.28) * mm, "end": v(-24.23, 25.8) * mm});
            skLineSegment(sketch, "E1558", {"start": v(-24.23, 25.8) * mm, "end": v(-25.8, 24.23) * mm});
            skLineSegment(sketch, "E1559", {"start": v(-25.8, 24.23) * mm, "end": v(-27.28, 22.57) * mm});
            skLineSegment(sketch, "E1560", {"start": v(-27.28, 22.57) * mm, "end": v(-28.64, 20.8) * mm});
            skLineSegment(sketch, "E1561", {"start": v(-28.64, 20.8) * mm, "end": v(-29.9, 18.97) * mm});
            skLineSegment(sketch, "E1562", {"start": v(-29.9, 18.97) * mm, "end": v(-31.02, 17.06) * mm});
            skLineSegment(sketch, "E1563", {"start": v(-31.02, 17.06) * mm, "end": v(-32.03, 15.07) * mm});
            skLineSegment(sketch, "E1564", {"start": v(-32.03, 15.07) * mm, "end": v(-32.92, 13.03) * mm});
            skLineSegment(sketch, "E1565", {"start": v(-32.92, 13.03) * mm, "end": v(-33.67, 10.94) * mm});
            skLineSegment(sketch, "E1566", {"start": v(-33.67, 10.94) * mm, "end": v(-34.29, 8.8) * mm});
            skLineSegment(sketch, "E1567", {"start": v(-34.29, 8.8) * mm, "end": v(-34.77, 6.63) * mm});
            skLineSegment(sketch, "E1568", {"start": v(-34.77, 6.63) * mm, "end": v(-35.12, 4.44) * mm});
            skLineSegment(sketch, "E1569", {"start": v(-35.12, 4.44) * mm, "end": v(-35.33, 2.22) * mm});
            skLineSegment(sketch, "E1570", {"start": v(-35.33, 2.22) * mm, "end": v(-35.34, 2.07) * mm});
            skLineSegment(sketch, "E1571", {"start": v(-35.34, 2.07) * mm, "end": v(-5.38, 1.98) * mm});
            skLineSegment(sketch, "E1572", {"start": v(-5.38, 1.98) * mm, "end": v(-5.33, 2.11) * mm});
            skLineSegment(sketch, "E1573", {"start": v(35.34, 2.07) * mm, "end": v(35.33, 2.22) * mm});
            skLineSegment(sketch, "E1574", {"start": v(35.33, 2.22) * mm, "end": v(35.12, 4.44) * mm});
            skLineSegment(sketch, "E1575", {"start": v(35.12, 4.44) * mm, "end": v(34.77, 6.63) * mm});
            skLineSegment(sketch, "E1576", {"start": v(34.77, 6.63) * mm, "end": v(34.29, 8.8) * mm});
            skLineSegment(sketch, "E1577", {"start": v(34.29, 8.8) * mm, "end": v(33.67, 10.94) * mm});
            skLineSegment(sketch, "E1578", {"start": v(33.67, 10.94) * mm, "end": v(32.92, 13.03) * mm});
            skLineSegment(sketch, "E1579", {"start": v(32.92, 13.03) * mm, "end": v(32.03, 15.07) * mm});
            skLineSegment(sketch, "E1580", {"start": v(32.03, 15.07) * mm, "end": v(31.02, 17.06) * mm});
            skLineSegment(sketch, "E1581", {"start": v(31.02, 17.06) * mm, "end": v(29.9, 18.97) * mm});
            skLineSegment(sketch, "E1582", {"start": v(29.9, 18.97) * mm, "end": v(28.64, 20.8) * mm});
            skLineSegment(sketch, "E1583", {"start": v(28.64, 20.8) * mm, "end": v(27.28, 22.57) * mm});
            skLineSegment(sketch, "E1584", {"start": v(27.28, 22.57) * mm, "end": v(25.8, 24.23) * mm});
            skLineSegment(sketch, "E1585", {"start": v(25.8, 24.23) * mm, "end": v(24.23, 25.8) * mm});
            skLineSegment(sketch, "E1586", {"start": v(24.23, 25.8) * mm, "end": v(22.57, 27.28) * mm});
            skLineSegment(sketch, "E1587", {"start": v(22.57, 27.28) * mm, "end": v(20.8, 28.64) * mm});
            skLineSegment(sketch, "E1588", {"start": v(20.8, 28.64) * mm, "end": v(18.97, 29.9) * mm});
            skLineSegment(sketch, "E1589", {"start": v(18.97, 29.9) * mm, "end": v(17.06, 31.02) * mm});
            skLineSegment(sketch, "E1590", {"start": v(17.06, 31.02) * mm, "end": v(15.07, 32.03) * mm});
            skLineSegment(sketch, "E1591", {"start": v(15.07, 32.03) * mm, "end": v(13.03, 32.92) * mm});
            skLineSegment(sketch, "E1592", {"start": v(13.03, 32.92) * mm, "end": v(10.94, 33.67) * mm});
            skLineSegment(sketch, "E1593", {"start": v(10.94, 33.67) * mm, "end": v(8.8, 34.29) * mm});
            skLineSegment(sketch, "E1594", {"start": v(8.8, 34.29) * mm, "end": v(6.63, 34.77) * mm});
            skLineSegment(sketch, "E1595", {"start": v(6.63, 34.77) * mm, "end": v(4.44, 35.12) * mm});
            skLineSegment(sketch, "E1596", {"start": v(4.44, 35.12) * mm, "end": v(2.22, 35.33) * mm});
            skLineSegment(sketch, "E1597", {"start": v(2.22, 35.33) * mm, "end": v(2.07, 35.34) * mm});
            skLineSegment(sketch, "E1598", {"start": v(2.07, 35.34) * mm, "end": v(1.98, 5.38) * mm});
            skLineSegment(sketch, "E1599", {"start": v(1.98, 5.38) * mm, "end": v(2.11, 5.33) * mm});
            skLineSegment(sketch, "E1600", {"start": v(2.11, 5.33) * mm, "end": v(2.44, 5.19) * mm});
            skLineSegment(sketch, "E1601", {"start": v(2.44, 5.19) * mm, "end": v(2.76, 5.02) * mm});
            skLineSegment(sketch, "E1602", {"start": v(2.76, 5.02) * mm, "end": v(3.07, 4.84) * mm});
            skLineSegment(sketch, "E1603", {"start": v(3.07, 4.84) * mm, "end": v(3.37, 4.64) * mm});
            skLineSegment(sketch, "E1604", {"start": v(3.37, 4.64) * mm, "end": v(3.65, 4.42) * mm});
            skLineSegment(sketch, "E1605", {"start": v(3.65, 4.42) * mm, "end": v(3.92, 4.18) * mm});
            skLineSegment(sketch, "E1606", {"start": v(3.92, 4.18) * mm, "end": v(4.18, 3.92) * mm});
            skLineSegment(sketch, "E1607", {"start": v(4.18, 3.92) * mm, "end": v(4.42, 3.65) * mm});
            skLineSegment(sketch, "E1608", {"start": v(4.42, 3.65) * mm, "end": v(4.64, 3.37) * mm});
            skLineSegment(sketch, "E1609", {"start": v(4.64, 3.37) * mm, "end": v(4.84, 3.07) * mm});
            skLineSegment(sketch, "E1610", {"start": v(4.84, 3.07) * mm, "end": v(5.02, 2.76) * mm});
            skLineSegment(sketch, "E1611", {"start": v(5.02, 2.76) * mm, "end": v(5.19, 2.44) * mm});
            skLineSegment(sketch, "E1612", {"start": v(5.19, 2.44) * mm, "end": v(5.33, 2.11) * mm});
            skLineSegment(sketch, "E1613", {"start": v(5.33, 2.11) * mm, "end": v(5.38, 1.98) * mm});
            skLineSegment(sketch, "E1614", {"start": v(5.38, 1.98) * mm, "end": v(35.34, 2.07) * mm});
            skLineSegment(sketch, "E1615", {"start": v(2.22, -35.33) * mm, "end": v(4.44, -35.12) * mm});
            skLineSegment(sketch, "E1616", {"start": v(4.44, -35.12) * mm, "end": v(6.63, -34.77) * mm});
            skLineSegment(sketch, "E1617", {"start": v(6.63, -34.77) * mm, "end": v(8.8, -34.29) * mm});
            skLineSegment(sketch, "E1618", {"start": v(8.8, -34.29) * mm, "end": v(10.94, -33.67) * mm});
            skLineSegment(sketch, "E1619", {"start": v(10.94, -33.67) * mm, "end": v(13.03, -32.92) * mm});
            skLineSegment(sketch, "E1620", {"start": v(13.03, -32.92) * mm, "end": v(15.07, -32.03) * mm});
            skLineSegment(sketch, "E1621", {"start": v(15.07, -32.03) * mm, "end": v(17.06, -31.02) * mm});
            skLineSegment(sketch, "E1622", {"start": v(17.06, -31.02) * mm, "end": v(18.97, -29.9) * mm});
            skLineSegment(sketch, "E1623", {"start": v(18.97, -29.9) * mm, "end": v(20.8, -28.64) * mm});
            skLineSegment(sketch, "E1624", {"start": v(20.8, -28.64) * mm, "end": v(22.57, -27.28) * mm});
            skLineSegment(sketch, "E1625", {"start": v(22.57, -27.28) * mm, "end": v(24.23, -25.8) * mm});
            skLineSegment(sketch, "E1626", {"start": v(24.23, -25.8) * mm, "end": v(25.8, -24.23) * mm});
            skLineSegment(sketch, "E1627", {"start": v(25.8, -24.23) * mm, "end": v(27.28, -22.57) * mm});
            skLineSegment(sketch, "E1628", {"start": v(27.28, -22.57) * mm, "end": v(28.64, -20.8) * mm});
            skLineSegment(sketch, "E1629", {"start": v(28.64, -20.8) * mm, "end": v(29.9, -18.97) * mm});
            skLineSegment(sketch, "E1630", {"start": v(29.9, -18.97) * mm, "end": v(31.02, -17.06) * mm});
            skLineSegment(sketch, "E1631", {"start": v(31.02, -17.06) * mm, "end": v(32.03, -15.07) * mm});
            skLineSegment(sketch, "E1632", {"start": v(32.03, -15.07) * mm, "end": v(32.92, -13.03) * mm});
            skLineSegment(sketch, "E1633", {"start": v(32.92, -13.03) * mm, "end": v(33.67, -10.94) * mm});
            skLineSegment(sketch, "E1634", {"start": v(33.67, -10.94) * mm, "end": v(34.29, -8.8) * mm});
            skLineSegment(sketch, "E1635", {"start": v(34.29, -8.8) * mm, "end": v(34.77, -6.63) * mm});
            skLineSegment(sketch, "E1636", {"start": v(34.77, -6.63) * mm, "end": v(35.12, -4.44) * mm});
            skLineSegment(sketch, "E1637", {"start": v(35.12, -4.44) * mm, "end": v(35.33, -2.22) * mm});
            skLineSegment(sketch, "E1638", {"start": v(35.33, -2.22) * mm, "end": v(35.34, -2.07) * mm});
            skLineSegment(sketch, "E1639", {"start": v(35.34, -2.07) * mm, "end": v(5.38, -1.98) * mm});
            skLineSegment(sketch, "E1640", {"start": v(5.38, -1.98) * mm, "end": v(5.33, -2.11) * mm});
            skLineSegment(sketch, "E1641", {"start": v(5.33, -2.11) * mm, "end": v(5.19, -2.44) * mm});
            skLineSegment(sketch, "E1642", {"start": v(5.19, -2.44) * mm, "end": v(5.02, -2.76) * mm});
            skLineSegment(sketch, "E1643", {"start": v(5.02, -2.76) * mm, "end": v(4.84, -3.07) * mm});
            skLineSegment(sketch, "E1644", {"start": v(4.84, -3.07) * mm, "end": v(4.64, -3.37) * mm});
            skLineSegment(sketch, "E1645", {"start": v(4.64, -3.37) * mm, "end": v(4.42, -3.65) * mm});
            skLineSegment(sketch, "E1646", {"start": v(4.42, -3.65) * mm, "end": v(4.18, -3.92) * mm});
            skLineSegment(sketch, "E1647", {"start": v(4.18, -3.92) * mm, "end": v(3.92, -4.18) * mm});
            skLineSegment(sketch, "E1648", {"start": v(3.92, -4.18) * mm, "end": v(3.65, -4.42) * mm});
            skLineSegment(sketch, "E1649", {"start": v(3.65, -4.42) * mm, "end": v(3.37, -4.64) * mm});
            skLineSegment(sketch, "E1650", {"start": v(3.37, -4.64) * mm, "end": v(3.07, -4.84) * mm});
            skLineSegment(sketch, "E1651", {"start": v(3.07, -4.84) * mm, "end": v(2.76, -5.02) * mm});
            skLineSegment(sketch, "E1652", {"start": v(2.76, -5.02) * mm, "end": v(2.44, -5.19) * mm});
            skLineSegment(sketch, "E1653", {"start": v(2.44, -5.19) * mm, "end": v(2.11, -5.33) * mm});
            skLineSegment(sketch, "E1654", {"start": v(2.11, -5.33) * mm, "end": v(1.98, -5.38) * mm});
            skLineSegment(sketch, "E1655", {"start": v(1.98, -5.38) * mm, "end": v(2.07, -35.34) * mm});
            skLineSegment(sketch, "E1656", {"start": v(2.07, -35.34) * mm, "end": v(2.22, -35.33) * mm});
            skLineSegment(sketch, "E1657", {"start": v(-1.98, -5.38) * mm, "end": v(-2.11, -5.33) * mm});
            skLineSegment(sketch, "E1658", {"start": v(-2.11, -5.33) * mm, "end": v(-2.44, -5.19) * mm});
            skLineSegment(sketch, "E1659", {"start": v(-2.44, -5.19) * mm, "end": v(-2.76, -5.02) * mm});
            skLineSegment(sketch, "E1660", {"start": v(-2.76, -5.02) * mm, "end": v(-3.07, -4.84) * mm});
            skLineSegment(sketch, "E1661", {"start": v(-3.07, -4.84) * mm, "end": v(-3.37, -4.64) * mm});
            skLineSegment(sketch, "E1662", {"start": v(-3.37, -4.64) * mm, "end": v(-3.65, -4.42) * mm});
            skLineSegment(sketch, "E1663", {"start": v(-3.65, -4.42) * mm, "end": v(-3.92, -4.18) * mm});
            skLineSegment(sketch, "E1664", {"start": v(-3.92, -4.18) * mm, "end": v(-4.18, -3.92) * mm});
            skLineSegment(sketch, "E1665", {"start": v(-4.18, -3.92) * mm, "end": v(-4.42, -3.65) * mm});
            skLineSegment(sketch, "E1666", {"start": v(-4.42, -3.65) * mm, "end": v(-4.64, -3.37) * mm});
            skLineSegment(sketch, "E1667", {"start": v(-4.64, -3.37) * mm, "end": v(-4.84, -3.07) * mm});
            skLineSegment(sketch, "E1668", {"start": v(-4.84, -3.07) * mm, "end": v(-5.02, -2.76) * mm});
            skLineSegment(sketch, "E1669", {"start": v(-5.02, -2.76) * mm, "end": v(-5.19, -2.44) * mm});
            skLineSegment(sketch, "E1670", {"start": v(-5.19, -2.44) * mm, "end": v(-5.33, -2.11) * mm});
            skLineSegment(sketch, "E1671", {"start": v(-5.33, -2.11) * mm, "end": v(-5.38, -1.98) * mm});
            skLineSegment(sketch, "E1672", {"start": v(-5.38, -1.98) * mm, "end": v(-35.34, -2.07) * mm});
            skLineSegment(sketch, "E1673", {"start": v(-35.34, -2.07) * mm, "end": v(-35.33, -2.22) * mm});
            skLineSegment(sketch, "E1674", {"start": v(-35.33, -2.22) * mm, "end": v(-35.12, -4.44) * mm});
            skLineSegment(sketch, "E1675", {"start": v(-35.12, -4.44) * mm, "end": v(-34.77, -6.63) * mm});
            skLineSegment(sketch, "E1676", {"start": v(-34.77, -6.63) * mm, "end": v(-34.29, -8.8) * mm});
            skLineSegment(sketch, "E1677", {"start": v(-34.29, -8.8) * mm, "end": v(-33.67, -10.94) * mm});
            skLineSegment(sketch, "E1678", {"start": v(-33.67, -10.94) * mm, "end": v(-32.92, -13.03) * mm});
            skLineSegment(sketch, "E1679", {"start": v(-32.92, -13.03) * mm, "end": v(-32.03, -15.07) * mm});
            skLineSegment(sketch, "E1680", {"start": v(-32.03, -15.07) * mm, "end": v(-31.02, -17.06) * mm});
            skLineSegment(sketch, "E1681", {"start": v(-31.02, -17.06) * mm, "end": v(-29.9, -18.97) * mm});
            skLineSegment(sketch, "E1682", {"start": v(-29.9, -18.97) * mm, "end": v(-28.64, -20.8) * mm});
            skLineSegment(sketch, "E1683", {"start": v(-28.64, -20.8) * mm, "end": v(-27.28, -22.57) * mm});
            skLineSegment(sketch, "E1684", {"start": v(-27.28, -22.57) * mm, "end": v(-25.8, -24.23) * mm});
            skLineSegment(sketch, "E1685", {"start": v(-25.8, -24.23) * mm, "end": v(-24.23, -25.8) * mm});
            skLineSegment(sketch, "E1686", {"start": v(-24.23, -25.8) * mm, "end": v(-22.57, -27.28) * mm});
            skLineSegment(sketch, "E1687", {"start": v(-22.57, -27.28) * mm, "end": v(-20.8, -28.64) * mm});
            skLineSegment(sketch, "E1688", {"start": v(-20.8, -28.64) * mm, "end": v(-18.97, -29.9) * mm});
            skLineSegment(sketch, "E1689", {"start": v(-18.97, -29.9) * mm, "end": v(-17.06, -31.02) * mm});
            skLineSegment(sketch, "E1690", {"start": v(-17.06, -31.02) * mm, "end": v(-15.07, -32.03) * mm});
            skLineSegment(sketch, "E1691", {"start": v(-15.07, -32.03) * mm, "end": v(-13.03, -32.92) * mm});
            skLineSegment(sketch, "E1692", {"start": v(-13.03, -32.92) * mm, "end": v(-10.94, -33.67) * mm});
            skLineSegment(sketch, "E1693", {"start": v(-10.94, -33.67) * mm, "end": v(-8.8, -34.29) * mm});
            skLineSegment(sketch, "E1694", {"start": v(-8.8, -34.29) * mm, "end": v(-6.63, -34.77) * mm});
            skLineSegment(sketch, "E1695", {"start": v(-6.63, -34.77) * mm, "end": v(-4.44, -35.12) * mm});
            skLineSegment(sketch, "E1696", {"start": v(-4.44, -35.12) * mm, "end": v(-2.22, -35.33) * mm});
            skLineSegment(sketch, "E1697", {"start": v(-2.22, -35.33) * mm, "end": v(-2.07, -35.34) * mm});
            skLineSegment(sketch, "E1698", {"start": v(-2.07, -35.34) * mm, "end": v(-1.98, -5.38) * mm});
            skLineSegment(sketch, "E1699", {"start": v(-1.5, 0) * mm, "end": v(1.5, 0) * mm});
            skCircle(sketch, "E1700", {"center": v(0, 0) * mm, "radius": 2.65 * mm});
            skCircle(sketch, "E1701", {"center": v(0, 0) * mm, "radius": 26.5 * mm});
            skCircle(sketch, "E1702", {"center": v(0, 0) * mm, "radius": 19.46 * mm});
            skCircle(sketch, "E1703", {"center": v(0, 0) * mm, "radius": 5.73 * mm, "construction": true});
            skSolve(sketch);
        }
        {
            var Q0;
            Q0=makeQuery(id+"F0.imprint","IMPRINT",FACE,{"disambiguationData":[TD([[makeQuery(id+"F0.imprint","IMPRINT",EDGE,{"derivedFrom":sQuery(id+"F0.wireOp",EDGE,"E0")}),1.0]])]});
            var Q1;
            Q1=makeQuery(id+"F0.imprint","IMPRINT",FACE,{"disambiguationData":[TD([[makeQuery(id+"F0.imprint","IMPRINT",EDGE,{"derivedFrom":sQuery(id+"F0.wireOp",EDGE,"E1531")}),-1.0]])]});
            var Q2;
            {var subQ0=sQuery(id+"F0.wireOp",EDGE,"E1702");var subQ1=sQuery(id+"F0.wireOp",EDGE,"E1545");var subQ2=makeQuery(id+"F0.imprint","INTERSECT",VERTEX,{"derivedFrom":[subQ1,subQ0]});Q2=makeQuery(id+"F0.imprint","IMPRINT",FACE,{"disambiguationData":[TD([[makeQuery(id+"F0.imprint","IMPRINT",EDGE,{"disambiguationData":[TD([[subQ2,-1.0]])],"derivedFrom":subQ1}),1.0]])]});}
            var Q3;
            {var subQ0=sQuery(id+"F0.wireOp",EDGE,"E1702");var subQ1=sQuery(id+"F0.wireOp",EDGE,"E1545");var subQ2=makeQuery(id+"F0.imprint","INTERSECT",VERTEX,{"derivedFrom":[subQ1,subQ0]});Q3=makeQuery(id+"F0.imprint","IMPRINT",FACE,{"disambiguationData":[TD([[makeQuery(id+"F0.imprint","IMPRINT",EDGE,{"disambiguationData":[TD([[subQ2,-1.0]])],"derivedFrom":subQ1}),-1.0]])]});}
            var Q4;
            {var subQ0=sQuery(id+"F0.wireOp",EDGE,"E1701");var subQ1=sQuery(id+"F0.wireOp",EDGE,"E1598");var subQ2=makeQuery(id+"F0.imprint","INTERSECT",VERTEX,{"derivedFrom":[subQ1,subQ0]});Q4=makeQuery(id+"F0.imprint","IMPRINT",FACE,{"disambiguationData":[TD([[makeQuery(id+"F0.imprint","IMPRINT",EDGE,{"disambiguationData":[TD([[subQ2,-1.0]])],"derivedFrom":subQ1}),1.0]])]});}
            var Q5;
            {var subQ0=sQuery(id+"F0.wireOp",EDGE,"E1702");var subQ1=sQuery(id+"F0.wireOp",EDGE,"E1614");var subQ2=makeQuery(id+"F0.imprint","INTERSECT",VERTEX,{"derivedFrom":[subQ1,subQ0]});Q5=makeQuery(id+"F0.imprint","IMPRINT",FACE,{"disambiguationData":[TD([[makeQuery(id+"F0.imprint","IMPRINT",EDGE,{"disambiguationData":[TD([[subQ2,-1.0]])],"derivedFrom":subQ1}),-1.0]])]});}
            var Q6;
            {var subQ0=sQuery(id+"F0.wireOp",EDGE,"E1701");var subQ1=sQuery(id+"F0.wireOp",EDGE,"E1639");var subQ2=makeQuery(id+"F0.imprint","INTERSECT",VERTEX,{"derivedFrom":[subQ1,subQ0]});Q6=makeQuery(id+"F0.imprint","IMPRINT",FACE,{"disambiguationData":[TD([[makeQuery(id+"F0.imprint","IMPRINT",EDGE,{"disambiguationData":[TD([[subQ2,-1.0]])],"derivedFrom":subQ1}),1.0]])]});}
            var Q7;
            {var subQ0=sQuery(id+"F0.wireOp",EDGE,"E1702");var subQ1=sQuery(id+"F0.wireOp",EDGE,"E1655");var subQ2=makeQuery(id+"F0.imprint","INTERSECT",VERTEX,{"derivedFrom":[subQ1,subQ0]});Q7=makeQuery(id+"F0.imprint","IMPRINT",FACE,{"disambiguationData":[TD([[makeQuery(id+"F0.imprint","IMPRINT",EDGE,{"disambiguationData":[TD([[subQ2,-1.0]])],"derivedFrom":subQ1}),-1.0]])]});}
            var Q8;
            {var subQ0=sQuery(id+"F0.wireOp",EDGE,"E1702");var subQ1=sQuery(id+"F0.wireOp",EDGE,"E1672");var subQ2=makeQuery(id+"F0.imprint","INTERSECT",VERTEX,{"derivedFrom":[subQ1,subQ0]});Q8=makeQuery(id+"F0.imprint","IMPRINT",FACE,{"disambiguationData":[TD([[makeQuery(id+"F0.imprint","IMPRINT",EDGE,{"disambiguationData":[TD([[subQ2,-1.0]])],"derivedFrom":subQ1}),1.0]])]});}
            var Q9;
            {var subQ0=sQuery(id+"F0.wireOp",EDGE,"E1701");var subQ1=sQuery(id+"F0.wireOp",EDGE,"E1571");var subQ2=makeQuery(id+"F0.imprint","INTERSECT",VERTEX,{"derivedFrom":[subQ1,subQ0]});Q9=makeQuery(id+"F0.imprint","IMPRINT",FACE,{"disambiguationData":[TD([[makeQuery(id+"F0.imprint","IMPRINT",EDGE,{"disambiguationData":[TD([[subQ2,-1.0]])],"derivedFrom":subQ1}),-1.0]])]});}
            extrude(context, id + "F1", {"entities" : qUnion([Q0, Q1, Q2, Q3, Q4, Q5, Q6, Q7, Q8, Q9]), "depth" : 5 * mm});
        }
    });
